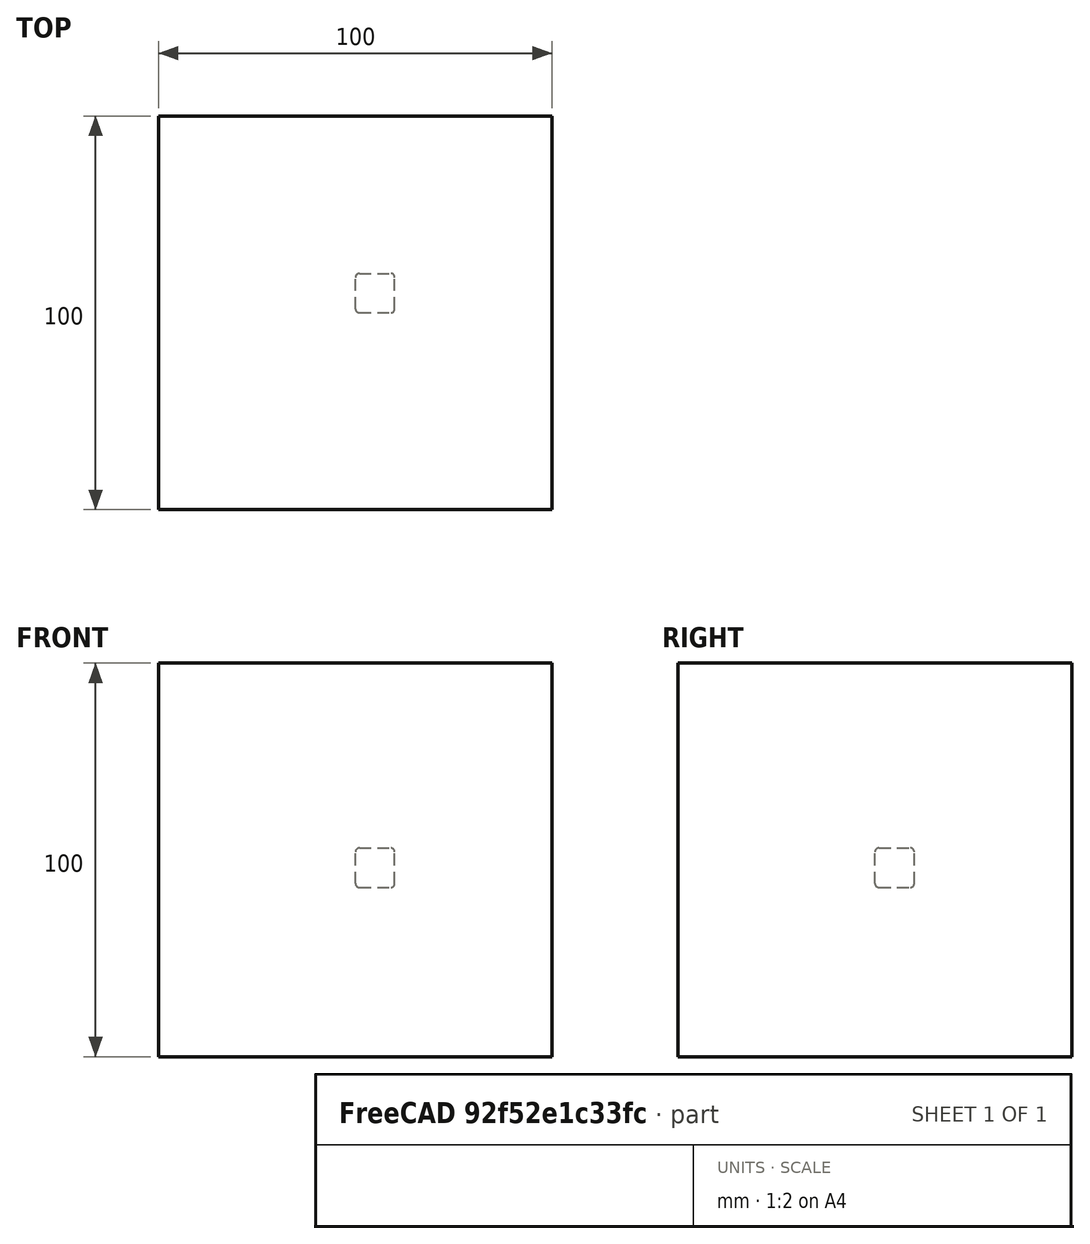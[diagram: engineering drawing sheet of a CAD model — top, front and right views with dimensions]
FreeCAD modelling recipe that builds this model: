
FCSTD DOCUMENT  (FreeCAD 1.0R39109 (Git))
Label: fillet
License: All rights reserved
objects: App::DocumentObjectGroupPython×1251, App::Part×2, Part::FeaturePython×1, Part::Box×1, Part::Fillet×1
note: 3 computed .brp shape members not serialized (recipe doc carries the construction recipe); baked Part::Feature solids carry a one-line shape summary decoded from their .brp

FEATURE [App::DocumentObjectGroupPython] HALFPI  # scripted group (container) (typed FeaturePython)
  name = HALFPI
  value = pi/2.
FEATURE [App::DocumentObjectGroupPython] PI  # scripted group (container) (typed FeaturePython)
  name = PI
  value = 1.*pi
FEATURE [App::DocumentObjectGroupPython] TWOPI  # scripted group (container) (typed FeaturePython)
  name = TWOPI
  value = 2.*pi
FEATURE [App::DocumentObjectGroupPython] Constants  # scripted group (container) (typed FeaturePython)
  Group = -> [HALFPI,PI,TWOPI]
FEATURE [App::DocumentObjectGroupPython] Variables  # scripted group (container) (typed FeaturePython)
FEATURE [App::DocumentObjectGroupPython] Quantities  # scripted group (container) (typed FeaturePython)
FEATURE [App::DocumentObjectGroupPython] Isotopes  # scripted group (container) (typed FeaturePython)
FEATURE [App::DocumentObjectGroupPython] Elements  # scripted group (container) (typed FeaturePython)
FEATURE [App::DocumentObjectGroupPython] Matrix  # scripted group (container) (typed FeaturePython)
FEATURE [App::DocumentObjectGroupPython] Surfaces  # scripted group (container) (typed FeaturePython)
FEATURE [App::DocumentObjectGroupPython] Opticals  # scripted group (container) (typed FeaturePython)
  Group = -> [Matrix,Surfaces]
FEATURE [App::DocumentObjectGroupPython] G4Isotopes  # scripted group (container) (typed FeaturePython)
FEATURE [App::DocumentObjectGroupPython] H_element  # scripted group (container) (typed FeaturePython)
  Z = 1
  atom_value = 1.008
  formula = H
  name = H_element
FEATURE [App::DocumentObjectGroupPython] He_element  # scripted group (container) (typed FeaturePython)
  Z = 2
  atom_value = 4.0026
  formula = He
  name = He_element
FEATURE [App::DocumentObjectGroupPython] Li_element  # scripted group (container) (typed FeaturePython)
  Z = 3
  atom_value = 6.94
  formula = Li
  name = Li_element
FEATURE [App::DocumentObjectGroupPython] Be_element  # scripted group (container) (typed FeaturePython)
  Z = 4
  atom_value = 9.01218
  formula = Be
  name = Be_element
FEATURE [App::DocumentObjectGroupPython] B_element  # scripted group (container) (typed FeaturePython)
  Z = 5
  atom_value = 10.81
  formula = B
  name = B_element
FEATURE [App::DocumentObjectGroupPython] C_element  # scripted group (container) (typed FeaturePython)
  Z = 6
  atom_value = 12.011
  formula = C
  name = C_element
FEATURE [App::DocumentObjectGroupPython] N_element  # scripted group (container) (typed FeaturePython)
  Z = 7
  atom_value = 14.007
  formula = N
  name = N_element
FEATURE [App::DocumentObjectGroupPython] O_element  # scripted group (container) (typed FeaturePython)
  Z = 8
  atom_value = 15.999
  formula = O
  name = O_element
FEATURE [App::DocumentObjectGroupPython] F_element  # scripted group (container) (typed FeaturePython)
  Z = 9
  atom_value = 18.9984
  formula = F
  name = F_element
FEATURE [App::DocumentObjectGroupPython] Ne_element  # scripted group (container) (typed FeaturePython)
  Z = 10
  atom_value = 20.1797
  formula = Ne
  name = Ne_element
FEATURE [App::DocumentObjectGroupPython] Na_element  # scripted group (container) (typed FeaturePython)
  Z = 11
  atom_value = 22.9898
  formula = Na
  name = Na_element
FEATURE [App::DocumentObjectGroupPython] Mg_element  # scripted group (container) (typed FeaturePython)
  Z = 12
  atom_value = 24.305
  formula = Mg
  name = Mg_element
FEATURE [App::DocumentObjectGroupPython] Al_element  # scripted group (container) (typed FeaturePython)
  Z = 13
  atom_value = 26.9815
  formula = Al
  name = Al_element
FEATURE [App::DocumentObjectGroupPython] Si_element  # scripted group (container) (typed FeaturePython)
  Z = 14
  atom_value = 28.085
  formula = Si
  name = Si_element
FEATURE [App::DocumentObjectGroupPython] P_element  # scripted group (container) (typed FeaturePython)
  Z = 15
  atom_value = 30.9738
  formula = P
  name = P_element
FEATURE [App::DocumentObjectGroupPython] S_element  # scripted group (container) (typed FeaturePython)
  Z = 16
  atom_value = 32.06
  formula = S
  name = S_element
FEATURE [App::DocumentObjectGroupPython] Cl_element  # scripted group (container) (typed FeaturePython)
  Z = 17
  atom_value = 35.45
  formula = Cl
  name = Cl_element
FEATURE [App::DocumentObjectGroupPython] Ar_element  # scripted group (container) (typed FeaturePython)
  Z = 18
  atom_value = 39.95
  formula = Ar
  name = Ar_element
FEATURE [App::DocumentObjectGroupPython] K_element  # scripted group (container) (typed FeaturePython)
  Z = 19
  atom_value = 39.0983
  formula = K
  name = K_element
FEATURE [App::DocumentObjectGroupPython] Ca_element  # scripted group (container) (typed FeaturePython)
  Z = 20
  atom_value = 40.078
  formula = Ca
  name = Ca_element
FEATURE [App::DocumentObjectGroupPython] Sc_element  # scripted group (container) (typed FeaturePython)
  Z = 21
  atom_value = 44.9559
  formula = Sc
  name = Sc_element
FEATURE [App::DocumentObjectGroupPython] Ti_element  # scripted group (container) (typed FeaturePython)
  Z = 22
  atom_value = 47.867
  formula = Ti
  name = Ti_element
FEATURE [App::DocumentObjectGroupPython] V_element  # scripted group (container) (typed FeaturePython)
  Z = 23
  atom_value = 50.9415
  formula = V
  name = V_element
FEATURE [App::DocumentObjectGroupPython] Cr_element  # scripted group (container) (typed FeaturePython)
  Z = 24
  atom_value = 51.9961
  formula = Cr
  name = Cr_element
FEATURE [App::DocumentObjectGroupPython] Mn_element  # scripted group (container) (typed FeaturePython)
  Z = 25
  atom_value = 54.938
  formula = Mn
  name = Mn_element
FEATURE [App::DocumentObjectGroupPython] Fe_element  # scripted group (container) (typed FeaturePython)
  Z = 26
  atom_value = 55.845
  formula = Fe
  name = Fe_element
FEATURE [App::DocumentObjectGroupPython] Co_element  # scripted group (container) (typed FeaturePython)
  Z = 27
  atom_value = 58.9332
  formula = Co
  name = Co_element
FEATURE [App::DocumentObjectGroupPython] Ni_element  # scripted group (container) (typed FeaturePython)
  Z = 28
  atom_value = 58.6934
  formula = Ni
  name = Ni_element
FEATURE [App::DocumentObjectGroupPython] Cu_element  # scripted group (container) (typed FeaturePython)
  Z = 29
  atom_value = 63.546
  formula = Cu
  name = Cu_element
FEATURE [App::DocumentObjectGroupPython] Zn_element  # scripted group (container) (typed FeaturePython)
  Z = 30
  atom_value = 65.38
  formula = Zn
  name = Zn_element
FEATURE [App::DocumentObjectGroupPython] Ga_element  # scripted group (container) (typed FeaturePython)
  Z = 31
  atom_value = 69.723
  formula = Ga
  name = Ga_element
FEATURE [App::DocumentObjectGroupPython] Ge_element  # scripted group (container) (typed FeaturePython)
  Z = 32
  atom_value = 72.63
  formula = Ge
  name = Ge_element
FEATURE [App::DocumentObjectGroupPython] As_element  # scripted group (container) (typed FeaturePython)
  Z = 33
  atom_value = 74.9216
  formula = As
  name = As_element
FEATURE [App::DocumentObjectGroupPython] Se_element  # scripted group (container) (typed FeaturePython)
  Z = 34
  atom_value = 78.971
  formula = Se
  name = Se_element
FEATURE [App::DocumentObjectGroupPython] Br_element  # scripted group (container) (typed FeaturePython)
  Z = 35
  atom_value = 79.904
  formula = Br
  name = Br_element
FEATURE [App::DocumentObjectGroupPython] Kr_element  # scripted group (container) (typed FeaturePython)
  Z = 36
  atom_value = 83.798
  formula = Kr
  name = Kr_element
FEATURE [App::DocumentObjectGroupPython] Rb_element  # scripted group (container) (typed FeaturePython)
  Z = 37
  atom_value = 85.4678
  formula = Rb
  name = Rb_element
FEATURE [App::DocumentObjectGroupPython] Sr_element  # scripted group (container) (typed FeaturePython)
  Z = 38
  atom_value = 87.62
  formula = Sr
  name = Sr_element
FEATURE [App::DocumentObjectGroupPython] Y_element  # scripted group (container) (typed FeaturePython)
  Z = 39
  atom_value = 88.9058
  formula = Y
  name = Y_element
FEATURE [App::DocumentObjectGroupPython] Zr_element  # scripted group (container) (typed FeaturePython)
  Z = 40
  atom_value = 91.224
  formula = Zr
  name = Zr_element
FEATURE [App::DocumentObjectGroupPython] Nb_element  # scripted group (container) (typed FeaturePython)
  Z = 41
  atom_value = 92.9064
  formula = Nb
  name = Nb_element
FEATURE [App::DocumentObjectGroupPython] Mo_element  # scripted group (container) (typed FeaturePython)
  Z = 42
  atom_value = 95.95
  formula = Mo
  name = Mo_element
FEATURE [App::DocumentObjectGroupPython] Tc_element  # scripted group (container) (typed FeaturePython)
  Z = 43
  atom_value = 97
  formula = Tc
  name = Tc_element
FEATURE [App::DocumentObjectGroupPython] Ru_element  # scripted group (container) (typed FeaturePython)
  Z = 44
  atom_value = 101.07
  formula = Ru
  name = Ru_element
FEATURE [App::DocumentObjectGroupPython] Rh_element  # scripted group (container) (typed FeaturePython)
  Z = 45
  atom_value = 102.905
  formula = Rh
  name = Rh_element
FEATURE [App::DocumentObjectGroupPython] Pd_element  # scripted group (container) (typed FeaturePython)
  Z = 46
  atom_value = 106.42
  formula = Pd
  name = Pd_element
FEATURE [App::DocumentObjectGroupPython] Ag_element  # scripted group (container) (typed FeaturePython)
  Z = 47
  atom_value = 107.868
  formula = Ag
  name = Ag_element
FEATURE [App::DocumentObjectGroupPython] Cd_element  # scripted group (container) (typed FeaturePython)
  Z = 48
  atom_value = 112.414
  formula = Cd
  name = Cd_element
FEATURE [App::DocumentObjectGroupPython] In_element  # scripted group (container) (typed FeaturePython)
  Z = 49
  atom_value = 114.818
  formula = In
  name = In_element
FEATURE [App::DocumentObjectGroupPython] Sn_element  # scripted group (container) (typed FeaturePython)
  Z = 50
  atom_value = 118.71
  formula = Sn
  name = Sn_element
FEATURE [App::DocumentObjectGroupPython] Sb_element  # scripted group (container) (typed FeaturePython)
  Z = 51
  atom_value = 121.76
  formula = Sb
  name = Sb_element
FEATURE [App::DocumentObjectGroupPython] Te_element  # scripted group (container) (typed FeaturePython)
  Z = 52
  atom_value = 127.6
  formula = Te
  name = Te_element
FEATURE [App::DocumentObjectGroupPython] I_element  # scripted group (container) (typed FeaturePython)
  Z = 53
  atom_value = 126.904
  formula = I
  name = I_element
FEATURE [App::DocumentObjectGroupPython] Xe_element  # scripted group (container) (typed FeaturePython)
  Z = 54
  atom_value = 131.293
  formula = Xe
  name = Xe_element
FEATURE [App::DocumentObjectGroupPython] Cs_element  # scripted group (container) (typed FeaturePython)
  Z = 55
  atom_value = 132.905
  formula = Cs
  name = Cs_element
FEATURE [App::DocumentObjectGroupPython] Ba_element  # scripted group (container) (typed FeaturePython)
  Z = 56
  atom_value = 137.327
  formula = Ba
  name = Ba_element
FEATURE [App::DocumentObjectGroupPython] La_element  # scripted group (container) (typed FeaturePython)
  Z = 57
  atom_value = 138.905
  formula = La
  name = La_element
FEATURE [App::DocumentObjectGroupPython] Ce_element  # scripted group (container) (typed FeaturePython)
  Z = 58
  atom_value = 140.116
  formula = Ce
  name = Ce_element
FEATURE [App::DocumentObjectGroupPython] Pr_element  # scripted group (container) (typed FeaturePython)
  Z = 59
  atom_value = 140.908
  formula = Pr
  name = Pr_element
FEATURE [App::DocumentObjectGroupPython] Nd_element  # scripted group (container) (typed FeaturePython)
  Z = 60
  atom_value = 144.242
  formula = Nd
  name = Nd_element
FEATURE [App::DocumentObjectGroupPython] Pm_element  # scripted group (container) (typed FeaturePython)
  Z = 61
  atom_value = 145
  formula = Pm
  name = Pm_element
FEATURE [App::DocumentObjectGroupPython] Sm_element  # scripted group (container) (typed FeaturePython)
  Z = 62
  atom_value = 150.36
  formula = Sm
  name = Sm_element
FEATURE [App::DocumentObjectGroupPython] Eu_element  # scripted group (container) (typed FeaturePython)
  Z = 63
  atom_value = 151.964
  formula = Eu
  name = Eu_element
FEATURE [App::DocumentObjectGroupPython] Gd_element  # scripted group (container) (typed FeaturePython)
  Z = 64
  atom_value = 157.25
  formula = Gd
  name = Gd_element
FEATURE [App::DocumentObjectGroupPython] Tb_element  # scripted group (container) (typed FeaturePython)
  Z = 65
  atom_value = 158.925
  formula = Tb
  name = Tb_element
FEATURE [App::DocumentObjectGroupPython] Dy_element  # scripted group (container) (typed FeaturePython)
  Z = 66
  atom_value = 162.5
  formula = Dy
  name = Dy_element
FEATURE [App::DocumentObjectGroupPython] Ho_element  # scripted group (container) (typed FeaturePython)
  Z = 67
  atom_value = 164.93
  formula = Ho
  name = Ho_element
FEATURE [App::DocumentObjectGroupPython] Er_element  # scripted group (container) (typed FeaturePython)
  Z = 68
  atom_value = 167.259
  formula = Er
  name = Er_element
FEATURE [App::DocumentObjectGroupPython] Tm_element  # scripted group (container) (typed FeaturePython)
  Z = 69
  atom_value = 168.934
  formula = Tm
  name = Tm_element
FEATURE [App::DocumentObjectGroupPython] Yb_element  # scripted group (container) (typed FeaturePython)
  Z = 70
  atom_value = 173.045
  formula = Yb
  name = Yb_element
FEATURE [App::DocumentObjectGroupPython] Lu_element  # scripted group (container) (typed FeaturePython)
  Z = 71
  atom_value = 174.967
  formula = Lu
  name = Lu_element
FEATURE [App::DocumentObjectGroupPython] Hf_element  # scripted group (container) (typed FeaturePython)
  Z = 72
  atom_value = 178.49
  formula = Hf
  name = Hf_element
FEATURE [App::DocumentObjectGroupPython] Ta_element  # scripted group (container) (typed FeaturePython)
  Z = 73
  atom_value = 180.948
  formula = Ta
  name = Ta_element
FEATURE [App::DocumentObjectGroupPython] W_element  # scripted group (container) (typed FeaturePython)
  Z = 74
  atom_value = 183.84
  formula = W
  name = W_element
FEATURE [App::DocumentObjectGroupPython] Re_element  # scripted group (container) (typed FeaturePython)
  Z = 75
  atom_value = 186.207
  formula = Re
  name = Re_element
FEATURE [App::DocumentObjectGroupPython] Os_element  # scripted group (container) (typed FeaturePython)
  Z = 76
  atom_value = 190.23
  formula = Os
  name = Os_element
FEATURE [App::DocumentObjectGroupPython] Ir_element  # scripted group (container) (typed FeaturePython)
  Z = 77
  atom_value = 192.217
  formula = Ir
  name = Ir_element
FEATURE [App::DocumentObjectGroupPython] Pt_element  # scripted group (container) (typed FeaturePython)
  Z = 78
  atom_value = 195.084
  formula = Pt
  name = Pt_element
FEATURE [App::DocumentObjectGroupPython] Au_element  # scripted group (container) (typed FeaturePython)
  Z = 79
  atom_value = 196.967
  formula = Au
  name = Au_element
FEATURE [App::DocumentObjectGroupPython] Hg_element  # scripted group (container) (typed FeaturePython)
  Z = 80
  atom_value = 200.592
  formula = Hg
  name = Hg_element
FEATURE [App::DocumentObjectGroupPython] Tl_element  # scripted group (container) (typed FeaturePython)
  Z = 81
  atom_value = 204.38
  formula = Tl
  name = Tl_element
FEATURE [App::DocumentObjectGroupPython] Pb_element  # scripted group (container) (typed FeaturePython)
  Z = 82
  atom_value = 207.2
  formula = Pb
  name = Pb_element
FEATURE [App::DocumentObjectGroupPython] Bi_element  # scripted group (container) (typed FeaturePython)
  Z = 83
  atom_value = 208.98
  formula = Bi
  name = Bi_element
FEATURE [App::DocumentObjectGroupPython] Po_element  # scripted group (container) (typed FeaturePython)
  Z = 84
  atom_value = 209
  formula = Po
  name = Po_element
FEATURE [App::DocumentObjectGroupPython] At_element  # scripted group (container) (typed FeaturePython)
  Z = 85
  atom_value = 210
  formula = At
  name = At_element
FEATURE [App::DocumentObjectGroupPython] Rn_element  # scripted group (container) (typed FeaturePython)
  Z = 86
  atom_value = 222
  formula = Rn
  name = Rn_element
FEATURE [App::DocumentObjectGroupPython] Fr_element  # scripted group (container) (typed FeaturePython)
  Z = 87
  atom_value = 223
  formula = Fr
  name = Fr_element
FEATURE [App::DocumentObjectGroupPython] Ra_element  # scripted group (container) (typed FeaturePython)
  Z = 88
  atom_value = 226
  formula = Ra
  name = Ra_element
FEATURE [App::DocumentObjectGroupPython] Ac_element  # scripted group (container) (typed FeaturePython)
  Z = 89
  atom_value = 227
  formula = Ac
  name = Ac_element
FEATURE [App::DocumentObjectGroupPython] Th_element  # scripted group (container) (typed FeaturePython)
  Z = 90
  atom_value = 232.038
  formula = Th
  name = Th_element
FEATURE [App::DocumentObjectGroupPython] Pa_element  # scripted group (container) (typed FeaturePython)
  Z = 91
  atom_value = 231.036
  formula = Pa
  name = Pa_element
FEATURE [App::DocumentObjectGroupPython] U_element  # scripted group (container) (typed FeaturePython)
  Z = 92
  atom_value = 238.029
  formula = U
  name = U_element
FEATURE [App::DocumentObjectGroupPython] Np_element  # scripted group (container) (typed FeaturePython)
  Z = 93
  atom_value = 237
  formula = Np
  name = Np_element
FEATURE [App::DocumentObjectGroupPython] Pu_element  # scripted group (container) (typed FeaturePython)
  Z = 94
  atom_value = 244
  formula = Pu
  name = Pu_element
FEATURE [App::DocumentObjectGroupPython] Am_element  # scripted group (container) (typed FeaturePython)
  Z = 95
  atom_value = 243
  formula = Am
  name = Am_element
FEATURE [App::DocumentObjectGroupPython] Cm_element  # scripted group (container) (typed FeaturePython)
  Z = 96
  atom_value = 247
  formula = Cm
  name = Cm_element
FEATURE [App::DocumentObjectGroupPython] Bk_element  # scripted group (container) (typed FeaturePython)
  Z = 97
  atom_value = 247
  formula = Bk
  name = Bk_element
FEATURE [App::DocumentObjectGroupPython] Cf_element  # scripted group (container) (typed FeaturePython)
  Z = 98
  atom_value = 251
  formula = Cf
  name = Cf_element
FEATURE [App::DocumentObjectGroupPython] G4Elements  # scripted group (container) (typed FeaturePython)
  Group = -> [H_element,He_element,Li_element,Be_element,B_element,C_element,N_element,O_element,F_element,Ne_element,Na_element,Mg_element,Al_element,Si_element,P_element,S_element,Cl_element,Ar_element,K_element,Ca_element,Sc_element,Ti_element,V_element,Cr_element,Mn_element,Fe_element,Co_element,Ni_element,Cu_element,Zn_element,Ga_element,Ge_element,As_element,Se_element,Br_element,Kr_element,Rb_element,+61 more]
FEATURE [App::DocumentObjectGroupPython] H_element001  label="H_element : 0.101"  # scripted group (container) (typed FeaturePython)
  n = 0.101327
FEATURE [App::DocumentObjectGroupPython] C_element001  label="C_element : 0.775"  # scripted group (container) (typed FeaturePython)
  n = 0.7755
FEATURE [App::DocumentObjectGroupPython] N_element001  label="N_element : 0.035"  # scripted group (container) (typed FeaturePython)
  n = 0.035057
FEATURE [App::DocumentObjectGroupPython] O_element001  label="O_element : 0.052"  # scripted group (container) (typed FeaturePython)
  n = 0.0523159
FEATURE [App::DocumentObjectGroupPython] F_element001  label="F_element : 0.017"  # scripted group (container) (typed FeaturePython)
  n = 0.017422
FEATURE [App::DocumentObjectGroupPython] Ca_element001  label="Ca_element : 0.018"  # scripted group (container) (typed FeaturePython)
  n = 0.018378
FEATURE [App::DocumentObjectGroupPython] G4_A_150_TISSUE  label="G4_A-150_TISSUE"  # scripted group (container) (typed FeaturePython)
  Dunit = g/cm3
  Dvalue = 1.127
  Group = -> [H_element001,C_element001,N_element001,O_element001,F_element001,Ca_element001]
  conduct = 2
  density = 1
  expand = 3
  formula = G4_A-150_TISSUE
  name = G4_A-150_TISSUE
  specific = 4
FEATURE [App::DocumentObjectGroupPython] C_element002  label="C_element : 3"  # scripted group (container) (typed FeaturePython)
  n = 3
  ref = C_element
FEATURE [App::DocumentObjectGroupPython] H_element002  label="H_element : 6"  # scripted group (container) (typed FeaturePython)
  n = 6
  ref = H_element
FEATURE [App::DocumentObjectGroupPython] O_element002  label="O_element : 1"  # scripted group (container) (typed FeaturePython)
  n = 1
  ref = O_element
FEATURE [App::DocumentObjectGroupPython] G4_ACETONE  # scripted group (container) (typed FeaturePython)
  Dunit = g/cm3
  Dvalue = 0.7899
  Group = -> [C_element002,H_element002,O_element002]
  conduct = 2
  density = 1
  expand = 3
  formula = G4_ACETONE
  name = G4_ACETONE
  specific = 4
FEATURE [App::DocumentObjectGroupPython] C_element003  label="C_element : 2"  # scripted group (container) (typed FeaturePython)
  n = 2
  ref = C_element
FEATURE [App::DocumentObjectGroupPython] H_element003  label="H_element : 2"  # scripted group (container) (typed FeaturePython)
  n = 2
  ref = H_element
FEATURE [App::DocumentObjectGroupPython] G4_ACETYLENE  # scripted group (container) (typed FeaturePython)
  Dunit = g/cm3
  Dvalue = 0.0010967
  Group = -> [C_element003,H_element003]
  conduct = 2
  density = 1
  expand = 3
  formula = G4_ACETYLENE
  name = G4_ACETYLENE
  specific = 4
FEATURE [App::DocumentObjectGroupPython] C_element004  label="C_element : 5"  # scripted group (container) (typed FeaturePython)
  n = 5
  ref = C_element
FEATURE [App::DocumentObjectGroupPython] H_element004  label="H_element : 5"  # scripted group (container) (typed FeaturePython)
  n = 5
  ref = H_element
FEATURE [App::DocumentObjectGroupPython] N_element002  label="N_element : 5"  # scripted group (container) (typed FeaturePython)
  n = 5
  ref = N_element
FEATURE [App::DocumentObjectGroupPython] G4_ADENINE  # scripted group (container) (typed FeaturePython)
  Dunit = g/cm3
  Dvalue = 1.6
  Group = -> [C_element004,H_element004,N_element002]
  conduct = 2
  density = 1
  expand = 3
  formula = G4_ADENINE
  name = G4_ADENINE
  specific = 4
FEATURE [App::DocumentObjectGroupPython] H_element005  label="H_element : 0.114"  # scripted group (container) (typed FeaturePython)
  n = 0.114
FEATURE [App::DocumentObjectGroupPython] C_element005  label="C_element : 0.598"  # scripted group (container) (typed FeaturePython)
  n = 0.598
FEATURE [App::DocumentObjectGroupPython] N_element003  label="N_element : 0.007"  # scripted group (container) (typed FeaturePython)
  n = 0.007
FEATURE [App::DocumentObjectGroupPython] O_element003  label="O_element : 0.278"  # scripted group (container) (typed FeaturePython)
  n = 0.278
FEATURE [App::DocumentObjectGroupPython] Na_element001  label="Na_element : 0.001"  # scripted group (container) (typed FeaturePython)
  n = 0.001
FEATURE [App::DocumentObjectGroupPython] S_element001  label="S_element : 0.001"  # scripted group (container) (typed FeaturePython)
  n = 0.001
FEATURE [App::DocumentObjectGroupPython] Cl_element001  label="Cl_element : 0.001"  # scripted group (container) (typed FeaturePython)
  n = 0.001
FEATURE [App::DocumentObjectGroupPython] G4_ADIPOSE_TISSUE_ICRP  # scripted group (container) (typed FeaturePython)
  Dunit = g/cm3
  Dvalue = 0.95
  Group = -> [H_element005,C_element005,N_element003,O_element003,Na_element001,S_element001,Cl_element001]
  conduct = 2
  density = 1
  expand = 3
  formula = G4_ADIPOSE_TISSUE_ICRP
  name = G4_ADIPOSE_TISSUE_ICRP
  specific = 4
FEATURE [App::DocumentObjectGroupPython] C_element006  label="C_element : 0.000"  # scripted group (container) (typed FeaturePython)
  n = 0.000124
FEATURE [App::DocumentObjectGroupPython] N_element004  label="N_element : 0.755"  # scripted group (container) (typed FeaturePython)
  n = 0.755268
FEATURE [App::DocumentObjectGroupPython] O_element004  label="O_element : 0.232"  # scripted group (container) (typed FeaturePython)
  n = 0.231781
FEATURE [App::DocumentObjectGroupPython] Ar_element001  label="Ar_element : 0.013"  # scripted group (container) (typed FeaturePython)
  n = 0.012827
FEATURE [App::DocumentObjectGroupPython] G4_AIR  # scripted group (container) (typed FeaturePython)
  Dunit = g/cm3
  Dvalue = 0.00120479
  Group = -> [C_element006,N_element004,O_element004,Ar_element001]
  conduct = 2
  density = 1
  expand = 3
  formula = G4_AIR
  name = G4_AIR
  specific = 4
FEATURE [App::DocumentObjectGroupPython] C_element007  label="C_element : 006"  # scripted group (container) (typed FeaturePython)
  n = 3
  ref = C_element
FEATURE [App::DocumentObjectGroupPython] H_element006  label="H_element : 7"  # scripted group (container) (typed FeaturePython)
  n = 7
  ref = H_element
FEATURE [App::DocumentObjectGroupPython] N_element005  label="N_element : 1"  # scripted group (container) (typed FeaturePython)
  n = 1
  ref = N_element
FEATURE [App::DocumentObjectGroupPython] O_element005  label="O_element : 2"  # scripted group (container) (typed FeaturePython)
  n = 2
  ref = O_element
FEATURE [App::DocumentObjectGroupPython] G4_ALANINE  # scripted group (container) (typed FeaturePython)
  Dunit = g/cm3
  Dvalue = 1.42
  Group = -> [C_element007,H_element006,N_element005,O_element005]
  conduct = 2
  density = 1
  expand = 3
  formula = G4_ALANINE
  name = G4_ALANINE
  specific = 4
FEATURE [App::DocumentObjectGroupPython] Al_element001  label="Al_element : 2"  # scripted group (container) (typed FeaturePython)
  n = 2
  ref = Al_element
FEATURE [App::DocumentObjectGroupPython] O_element006  label="O_element : 3"  # scripted group (container) (typed FeaturePython)
  n = 3
  ref = O_element
FEATURE [App::DocumentObjectGroupPython] G4_ALUMINUM_OXIDE  # scripted group (container) (typed FeaturePython)
  Dunit = g/cm3
  Dvalue = 3.97
  Group = -> [Al_element001,O_element006]
  conduct = 2
  density = 1
  expand = 3
  formula = G4_ALUMINUM_OXIDE
  name = G4_ALUMINUM_OXIDE
  specific = 4
FEATURE [App::DocumentObjectGroupPython] H_element007  label="H_element : 0.106"  # scripted group (container) (typed FeaturePython)
  n = 0.10593
FEATURE [App::DocumentObjectGroupPython] C_element008  label="C_element : 0.789"  # scripted group (container) (typed FeaturePython)
  n = 0.788974
FEATURE [App::DocumentObjectGroupPython] O_element007  label="O_element : 0.105"  # scripted group (container) (typed FeaturePython)
  n = 0.105096
FEATURE [App::DocumentObjectGroupPython] G4_AMBER  # scripted group (container) (typed FeaturePython)
  Dunit = g/cm3
  Dvalue = 1.1
  Group = -> [H_element007,C_element008,O_element007]
  conduct = 2
  density = 1
  expand = 3
  formula = G4_AMBER
  name = G4_AMBER
  specific = 4
FEATURE [App::DocumentObjectGroupPython] N_element006  label="N_element : 006"  # scripted group (container) (typed FeaturePython)
  n = 1
  ref = N_element
FEATURE [App::DocumentObjectGroupPython] H_element008  label="H_element : 3"  # scripted group (container) (typed FeaturePython)
  n = 3
  ref = H_element
FEATURE [App::DocumentObjectGroupPython] G4_AMMONIA  # scripted group (container) (typed FeaturePython)
  Dunit = g/cm3
  Dvalue = 0.000826019
  Group = -> [N_element006,H_element008]
  conduct = 2
  density = 1
  expand = 3
  formula = G4_AMMONIA
  name = G4_AMMONIA
  specific = 4
FEATURE [App::DocumentObjectGroupPython] C_element009  label="C_element : 6"  # scripted group (container) (typed FeaturePython)
  n = 6
  ref = C_element
FEATURE [App::DocumentObjectGroupPython] H_element009  label="H_element : 008"  # scripted group (container) (typed FeaturePython)
  n = 7
  ref = H_element
FEATURE [App::DocumentObjectGroupPython] N_element007  label="N_element : 007"  # scripted group (container) (typed FeaturePython)
  n = 1
  ref = N_element
FEATURE [App::DocumentObjectGroupPython] G4_ANILINE  # scripted group (container) (typed FeaturePython)
  Dunit = g/cm3
  Dvalue = 1.0235
  Group = -> [C_element009,H_element009,N_element007]
  conduct = 2
  density = 1
  expand = 3
  formula = G4_ANILINE
  name = G4_ANILINE
  specific = 4
FEATURE [App::DocumentObjectGroupPython] C_element010  label="C_element : 14"  # scripted group (container) (typed FeaturePython)
  n = 14
  ref = C_element
FEATURE [App::DocumentObjectGroupPython] H_element010  label="H_element : 10"  # scripted group (container) (typed FeaturePython)
  n = 10
  ref = H_element
FEATURE [App::DocumentObjectGroupPython] G4_ANTHRACENE  # scripted group (container) (typed FeaturePython)
  Dunit = g/cm3
  Dvalue = 1.283
  Group = -> [C_element010,H_element010]
  conduct = 2
  density = 1
  expand = 3
  formula = G4_ANTHRACENE
  name = G4_ANTHRACENE
  specific = 4
FEATURE [App::DocumentObjectGroupPython] H_element011  label="H_element : 0.065"  # scripted group (container) (typed FeaturePython)
  n = 0.0654709
FEATURE [App::DocumentObjectGroupPython] C_element011  label="C_element : 0.537"  # scripted group (container) (typed FeaturePython)
  n = 0.536944
FEATURE [App::DocumentObjectGroupPython] N_element008  label="N_element : 0.021"  # scripted group (container) (typed FeaturePython)
  n = 0.0215
FEATURE [App::DocumentObjectGroupPython] O_element008  label="O_element : 0.032"  # scripted group (container) (typed FeaturePython)
  n = 0.032085
FEATURE [App::DocumentObjectGroupPython] F_element002  label="F_element : 0.167"  # scripted group (container) (typed FeaturePython)
  n = 0.167411
FEATURE [App::DocumentObjectGroupPython] Ca_element002  label="Ca_element : 0.177"  # scripted group (container) (typed FeaturePython)
  n = 0.176589
FEATURE [App::DocumentObjectGroupPython] G4_B_100_BONE  label="G4_B-100_BONE"  # scripted group (container) (typed FeaturePython)
  Dunit = g/cm3
  Dvalue = 1.45
  Group = -> [H_element011,C_element011,N_element008,O_element008,F_element002,Ca_element002]
  conduct = 2
  density = 1
  expand = 3
  formula = G4_B-100_BONE
  name = G4_B-100_BONE
  specific = 4
FEATURE [App::DocumentObjectGroupPython] H_element012  label="H_element : 0.057"  # scripted group (container) (typed FeaturePython)
  n = 0.057441
FEATURE [App::DocumentObjectGroupPython] C_element012  label="C_element : 0.790"  # scripted group (container) (typed FeaturePython)
  n = 0.774591
FEATURE [App::DocumentObjectGroupPython] O_element009  label="O_element : 0.168"  # scripted group (container) (typed FeaturePython)
  n = 0.167968
FEATURE [App::DocumentObjectGroupPython] G4_BAKELITE  # scripted group (container) (typed FeaturePython)
  Dunit = g/cm3
  Dvalue = 1.25
  Group = -> [H_element012,C_element012,O_element009]
  conduct = 2
  density = 1
  expand = 3
  formula = G4_BAKELITE
  name = G4_BAKELITE
  specific = 4
FEATURE [App::DocumentObjectGroupPython] Ba_element001  label="Ba_element : 1"  # scripted group (container) (typed FeaturePython)
  n = 1
  ref = Ba_element
FEATURE [App::DocumentObjectGroupPython] F_element003  label="F_element : 2"  # scripted group (container) (typed FeaturePython)
  n = 2
  ref = F_element
FEATURE [App::DocumentObjectGroupPython] G4_BARIUM_FLUORIDE  # scripted group (container) (typed FeaturePython)
  Dunit = g/cm3
  Dvalue = 4.89
  Group = -> [Ba_element001,F_element003]
  conduct = 2
  density = 1
  expand = 3
  formula = G4_BARIUM_FLUORIDE
  name = G4_BARIUM_FLUORIDE
  specific = 4
FEATURE [App::DocumentObjectGroupPython] Ba_element002  label="Ba_element : 002"  # scripted group (container) (typed FeaturePython)
  n = 1
  ref = Ba_element
FEATURE [App::DocumentObjectGroupPython] S_element002  label="S_element : 1"  # scripted group (container) (typed FeaturePython)
  n = 1
  ref = S_element
FEATURE [App::DocumentObjectGroupPython] O_element010  label="O_element : 4"  # scripted group (container) (typed FeaturePython)
  n = 4
  ref = O_element
FEATURE [App::DocumentObjectGroupPython] G4_BARIUM_SULFATE  # scripted group (container) (typed FeaturePython)
  Dunit = g/cm3
  Dvalue = 4.5
  Group = -> [Ba_element002,S_element002,O_element010]
  conduct = 2
  density = 1
  expand = 3
  formula = G4_BARIUM_SULFATE
  name = G4_BARIUM_SULFATE
  specific = 4
FEATURE [App::DocumentObjectGroupPython] C_element013  label="C_element : 007"  # scripted group (container) (typed FeaturePython)
  n = 6
  ref = C_element
FEATURE [App::DocumentObjectGroupPython] H_element013  label="H_element : 009"  # scripted group (container) (typed FeaturePython)
  n = 6
  ref = H_element
FEATURE [App::DocumentObjectGroupPython] G4_BENZENE  # scripted group (container) (typed FeaturePython)
  Dunit = g/cm3
  Dvalue = 0.87865
  Group = -> [C_element013,H_element013]
  conduct = 2
  density = 1
  expand = 3
  formula = G4_BENZENE
  name = G4_BENZENE
  specific = 4
FEATURE [App::DocumentObjectGroupPython] Be_element001  label="Be_element : 1"  # scripted group (container) (typed FeaturePython)
  n = 1
  ref = Be_element
FEATURE [App::DocumentObjectGroupPython] O_element011  label="O_element : 005"  # scripted group (container) (typed FeaturePython)
  n = 1
  ref = O_element
FEATURE [App::DocumentObjectGroupPython] G4_BERYLLIUM_OXIDE  # scripted group (container) (typed FeaturePython)
  Dunit = g/cm3
  Dvalue = 3.01
  Group = -> [Be_element001,O_element011]
  conduct = 2
  density = 1
  expand = 3
  formula = G4_BERYLLIUM_OXIDE
  name = G4_BERYLLIUM_OXIDE
  specific = 4
FEATURE [App::DocumentObjectGroupPython] Bi_element001  label="Bi_element : 4"  # scripted group (container) (typed FeaturePython)
  n = 4
  ref = Bi_element
FEATURE [App::DocumentObjectGroupPython] Ge_element001  label="Ge_element : 3"  # scripted group (container) (typed FeaturePython)
  n = 3
  ref = Ge_element
FEATURE [App::DocumentObjectGroupPython] O_element012  label="O_element : 12"  # scripted group (container) (typed FeaturePython)
  n = 12
  ref = O_element
FEATURE [App::DocumentObjectGroupPython] G4_BGO  # scripted group (container) (typed FeaturePython)
  Dunit = g/cm3
  Dvalue = 7.13
  Group = -> [Bi_element001,Ge_element001,O_element012]
  conduct = 2
  density = 1
  expand = 3
  formula = G4_BGO
  name = G4_BGO
  specific = 4
FEATURE [App::DocumentObjectGroupPython] H_element014  label="H_element : 0.102"  # scripted group (container) (typed FeaturePython)
  n = 0.102
FEATURE [App::DocumentObjectGroupPython] C_element014  label="C_element : 0.110"  # scripted group (container) (typed FeaturePython)
  n = 0.11
FEATURE [App::DocumentObjectGroupPython] N_element009  label="N_element : 0.033"  # scripted group (container) (typed FeaturePython)
  n = 0.033
FEATURE [App::DocumentObjectGroupPython] O_element013  label="O_element : 0.745"  # scripted group (container) (typed FeaturePython)
  n = 0.745
FEATURE [App::DocumentObjectGroupPython] Na_element002  label="Na_element : 0.002"  # scripted group (container) (typed FeaturePython)
  n = 0.001
FEATURE [App::DocumentObjectGroupPython] P_element001  label="P_element : 0.001"  # scripted group (container) (typed FeaturePython)
  n = 0.001
FEATURE [App::DocumentObjectGroupPython] S_element003  label="S_element : 0.002"  # scripted group (container) (typed FeaturePython)
  n = 0.002
FEATURE [App::DocumentObjectGroupPython] Cl_element002  label="Cl_element : 0.003"  # scripted group (container) (typed FeaturePython)
  n = 0.003
FEATURE [App::DocumentObjectGroupPython] K_element001  label="K_element : 0.002"  # scripted group (container) (typed FeaturePython)
  n = 0.002
FEATURE [App::DocumentObjectGroupPython] Fe_element001  label="Fe_element : 0.001"  # scripted group (container) (typed FeaturePython)
  n = 0.001
FEATURE [App::DocumentObjectGroupPython] G4_BLOOD_ICRP  # scripted group (container) (typed FeaturePython)
  Dunit = g/cm3
  Dvalue = 1.06
  Group = -> [H_element014,C_element014,N_element009,O_element013,Na_element002,P_element001,S_element003,Cl_element002,K_element001,Fe_element001]
  conduct = 2
  density = 1
  expand = 3
  formula = G4_BLOOD_ICRP
  name = G4_BLOOD_ICRP
  specific = 4
FEATURE [App::DocumentObjectGroupPython] H_element015  label="H_element : 0.064"  # scripted group (container) (typed FeaturePython)
  n = 0.064
FEATURE [App::DocumentObjectGroupPython] C_element015  label="C_element : 0.278"  # scripted group (container) (typed FeaturePython)
  n = 0.278
FEATURE [App::DocumentObjectGroupPython] N_element010  label="N_element : 0.027"  # scripted group (container) (typed FeaturePython)
  n = 0.027
FEATURE [App::DocumentObjectGroupPython] O_element014  label="O_element : 0.410"  # scripted group (container) (typed FeaturePython)
  n = 0.41
FEATURE [App::DocumentObjectGroupPython] Mg_element001  label="Mg_element : 0.002"  # scripted group (container) (typed FeaturePython)
  n = 0.002
FEATURE [App::DocumentObjectGroupPython] P_element002  label="P_element : 0.070"  # scripted group (container) (typed FeaturePython)
  n = 0.07
FEATURE [App::DocumentObjectGroupPython] S_element004  label="S_element : 0.003"  # scripted group (container) (typed FeaturePython)
  n = 0.002
FEATURE [App::DocumentObjectGroupPython] Ca_element003  label="Ca_element : 0.147"  # scripted group (container) (typed FeaturePython)
  n = 0.147
FEATURE [App::DocumentObjectGroupPython] G4_BONE_COMPACT_ICRU  # scripted group (container) (typed FeaturePython)
  Dunit = g/cm3
  Dvalue = 1.85
  Group = -> [H_element015,C_element015,N_element010,O_element014,Mg_element001,P_element002,S_element004,Ca_element003]
  conduct = 2
  density = 1
  expand = 3
  formula = G4_BONE_COMPACT_ICRU
  name = G4_BONE_COMPACT_ICRU
  specific = 4
FEATURE [App::DocumentObjectGroupPython] H_element016  label="H_element : 0.034"  # scripted group (container) (typed FeaturePython)
  n = 0.034
FEATURE [App::DocumentObjectGroupPython] C_element016  label="C_element : 0.155"  # scripted group (container) (typed FeaturePython)
  n = 0.155
FEATURE [App::DocumentObjectGroupPython] N_element011  label="N_element : 0.042"  # scripted group (container) (typed FeaturePython)
  n = 0.042
FEATURE [App::DocumentObjectGroupPython] O_element015  label="O_element : 0.435"  # scripted group (container) (typed FeaturePython)
  n = 0.435
FEATURE [App::DocumentObjectGroupPython] Na_element003  label="Na_element : 0.003"  # scripted group (container) (typed FeaturePython)
  n = 0.001
FEATURE [App::DocumentObjectGroupPython] Mg_element002  label="Mg_element : 0.003"  # scripted group (container) (typed FeaturePython)
  n = 0.002
FEATURE [App::DocumentObjectGroupPython] P_element003  label="P_element : 0.103"  # scripted group (container) (typed FeaturePython)
  n = 0.103
FEATURE [App::DocumentObjectGroupPython] S_element005  label="S_element : 0.004"  # scripted group (container) (typed FeaturePython)
  n = 0.003
FEATURE [App::DocumentObjectGroupPython] Ca_element004  label="Ca_element : 0.225"  # scripted group (container) (typed FeaturePython)
  n = 0.225
FEATURE [App::DocumentObjectGroupPython] G4_BONE_CORTICAL_ICRP  # scripted group (container) (typed FeaturePython)
  Dunit = g/cm3
  Dvalue = 1.92
  Group = -> [H_element016,C_element016,N_element011,O_element015,Na_element003,Mg_element002,P_element003,S_element005,Ca_element004]
  conduct = 2
  density = 1
  expand = 3
  formula = G4_BONE_CORTICAL_ICRP
  name = G4_BONE_CORTICAL_ICRP
  specific = 4
FEATURE [App::DocumentObjectGroupPython] B_element001  label="B_element : 4"  # scripted group (container) (typed FeaturePython)
  n = 4
  ref = B_element
FEATURE [App::DocumentObjectGroupPython] C_element017  label="C_element : 1"  # scripted group (container) (typed FeaturePython)
  n = 1
  ref = C_element
FEATURE [App::DocumentObjectGroupPython] G4_BORON_CARBIDE  # scripted group (container) (typed FeaturePython)
  Dunit = g/cm3
  Dvalue = 2.52
  Group = -> [B_element001,C_element017]
  conduct = 2
  density = 1
  expand = 3
  formula = G4_BORON_CARBIDE
  name = G4_BORON_CARBIDE
  specific = 4
FEATURE [App::DocumentObjectGroupPython] B_element002  label="B_element : 2"  # scripted group (container) (typed FeaturePython)
  n = 2
  ref = B_element
FEATURE [App::DocumentObjectGroupPython] O_element016  label="O_element : 006"  # scripted group (container) (typed FeaturePython)
  n = 3
  ref = O_element
FEATURE [App::DocumentObjectGroupPython] G4_BORON_OXIDE  # scripted group (container) (typed FeaturePython)
  Dunit = g/cm3
  Dvalue = 1.812
  Group = -> [B_element002,O_element016]
  conduct = 2
  density = 1
  expand = 3
  formula = G4_BORON_OXIDE
  name = G4_BORON_OXIDE
  specific = 4
FEATURE [App::DocumentObjectGroupPython] H_element017  label="H_element : 0.107"  # scripted group (container) (typed FeaturePython)
  n = 0.107
FEATURE [App::DocumentObjectGroupPython] C_element018  label="C_element : 0.145"  # scripted group (container) (typed FeaturePython)
  n = 0.145
FEATURE [App::DocumentObjectGroupPython] N_element012  label="N_element : 0.022"  # scripted group (container) (typed FeaturePython)
  n = 0.022
FEATURE [App::DocumentObjectGroupPython] O_element017  label="O_element : 0.712"  # scripted group (container) (typed FeaturePython)
  n = 0.712
FEATURE [App::DocumentObjectGroupPython] Na_element004  label="Na_element : 0.004"  # scripted group (container) (typed FeaturePython)
  n = 0.002
FEATURE [App::DocumentObjectGroupPython] P_element004  label="P_element : 0.004"  # scripted group (container) (typed FeaturePython)
  n = 0.004
FEATURE [App::DocumentObjectGroupPython] S_element006  label="S_element : 0.005"  # scripted group (container) (typed FeaturePython)
  n = 0.002
FEATURE [App::DocumentObjectGroupPython] Cl_element003  label="Cl_element : 0.004"  # scripted group (container) (typed FeaturePython)
  n = 0.003
FEATURE [App::DocumentObjectGroupPython] K_element002  label="K_element : 0.003"  # scripted group (container) (typed FeaturePython)
  n = 0.003
FEATURE [App::DocumentObjectGroupPython] G4_BRAIN_ICRP  # scripted group (container) (typed FeaturePython)
  Dunit = g/cm3
  Dvalue = 1.04
  Group = -> [H_element017,C_element018,N_element012,O_element017,Na_element004,P_element004,S_element006,Cl_element003,K_element002]
  conduct = 2
  density = 1
  expand = 3
  formula = G4_BRAIN_ICRP
  name = G4_BRAIN_ICRP
  specific = 4
FEATURE [App::DocumentObjectGroupPython] C_element019  label="C_element : 4"  # scripted group (container) (typed FeaturePython)
  n = 4
  ref = C_element
FEATURE [App::DocumentObjectGroupPython] H_element018  label="H_element : 010"  # scripted group (container) (typed FeaturePython)
  n = 10
  ref = H_element
FEATURE [App::DocumentObjectGroupPython] G4_BUTANE  # scripted group (container) (typed FeaturePython)
  Dunit = g/cm3
  Dvalue = 0.00249343
  Group = -> [C_element019,H_element018]
  conduct = 2
  density = 1
  expand = 3
  formula = G4_BUTANE
  name = G4_BUTANE
  specific = 4
FEATURE [App::DocumentObjectGroupPython] C_element020  label="C_element : 008"  # scripted group (container) (typed FeaturePython)
  n = 4
  ref = C_element
FEATURE [App::DocumentObjectGroupPython] H_element019  label="H_element : 011"  # scripted group (container) (typed FeaturePython)
  n = 10
  ref = H_element
FEATURE [App::DocumentObjectGroupPython] O_element018  label="O_element : 007"  # scripted group (container) (typed FeaturePython)
  n = 1
  ref = O_element
FEATURE [App::DocumentObjectGroupPython] G4_N_BUTYL_ALCOHOL  label="G4_N-BUTYL_ALCOHOL"  # scripted group (container) (typed FeaturePython)
  Dunit = g/cm3
  Dvalue = 0.8098
  Group = -> [C_element020,H_element019,O_element018]
  conduct = 2
  density = 1
  expand = 3
  formula = G4_N-BUTYL_ALCOHOL
  name = G4_N-BUTYL_ALCOHOL
  specific = 4
FEATURE [App::DocumentObjectGroupPython] H_element020  label="H_element : 0.025"  # scripted group (container) (typed FeaturePython)
  n = 0.02468
FEATURE [App::DocumentObjectGroupPython] C_element021  label="C_element : 0.502"  # scripted group (container) (typed FeaturePython)
  n = 0.501611
FEATURE [App::DocumentObjectGroupPython] O_element019  label="O_element : 0.005"  # scripted group (container) (typed FeaturePython)
  n = 0.004527
FEATURE [App::DocumentObjectGroupPython] F_element004  label="F_element : 0.465"  # scripted group (container) (typed FeaturePython)
  n = 0.465209
FEATURE [App::DocumentObjectGroupPython] Si_element001  label="Si_element : 0.004"  # scripted group (container) (typed FeaturePython)
  n = 0.003973
FEATURE [App::DocumentObjectGroupPython] G4_C_552  label="G4_C-552"  # scripted group (container) (typed FeaturePython)
  Dunit = g/cm3
  Dvalue = 1.76
  Group = -> [H_element020,C_element021,O_element019,F_element004,Si_element001]
  conduct = 2
  density = 1
  expand = 3
  formula = G4_C-552
  name = G4_C-552
  specific = 4
FEATURE [App::DocumentObjectGroupPython] Cd_element001  label="Cd_element : 1"  # scripted group (container) (typed FeaturePython)
  n = 1
  ref = Cd_element
FEATURE [App::DocumentObjectGroupPython] Te_element001  label="Te_element : 1"  # scripted group (container) (typed FeaturePython)
  n = 1
  ref = Te_element
FEATURE [App::DocumentObjectGroupPython] G4_CADMIUM_TELLURIDE  # scripted group (container) (typed FeaturePython)
  Dunit = g/cm3
  Dvalue = 6.2
  Group = -> [Cd_element001,Te_element001]
  conduct = 2
  density = 1
  expand = 3
  formula = G4_CADMIUM_TELLURIDE
  name = G4_CADMIUM_TELLURIDE
  specific = 4
FEATURE [App::DocumentObjectGroupPython] Cd_element002  label="Cd_element : 002"  # scripted group (container) (typed FeaturePython)
  n = 1
  ref = Cd_element
FEATURE [App::DocumentObjectGroupPython] W_element001  label="W_element : 1"  # scripted group (container) (typed FeaturePython)
  n = 1
  ref = W_element
FEATURE [App::DocumentObjectGroupPython] O_element020  label="O_element : 008"  # scripted group (container) (typed FeaturePython)
  n = 4
  ref = O_element
FEATURE [App::DocumentObjectGroupPython] G4_CADMIUM_TUNGSTATE  # scripted group (container) (typed FeaturePython)
  Dunit = g/cm3
  Dvalue = 7.9
  Group = -> [Cd_element002,W_element001,O_element020]
  conduct = 2
  density = 1
  expand = 3
  formula = G4_CADMIUM_TUNGSTATE
  name = G4_CADMIUM_TUNGSTATE
  specific = 4
FEATURE [App::DocumentObjectGroupPython] Ca_element005  label="Ca_element : 1"  # scripted group (container) (typed FeaturePython)
  n = 1
  ref = Ca_element
FEATURE [App::DocumentObjectGroupPython] C_element022  label="C_element : 009"  # scripted group (container) (typed FeaturePython)
  n = 1
  ref = C_element
FEATURE [App::DocumentObjectGroupPython] O_element021  label="O_element : 009"  # scripted group (container) (typed FeaturePython)
  n = 3
  ref = O_element
FEATURE [App::DocumentObjectGroupPython] G4_CALCIUM_CARBONATE  # scripted group (container) (typed FeaturePython)
  Dunit = g/cm3
  Dvalue = 2.8
  Group = -> [Ca_element005,C_element022,O_element021]
  conduct = 2
  density = 1
  expand = 3
  formula = G4_CALCIUM_CARBONATE
  name = G4_CALCIUM_CARBONATE
  specific = 4
FEATURE [App::DocumentObjectGroupPython] Ca_element006  label="Ca_element : 002"  # scripted group (container) (typed FeaturePython)
  n = 1
  ref = Ca_element
FEATURE [App::DocumentObjectGroupPython] F_element005  label="F_element : 003"  # scripted group (container) (typed FeaturePython)
  n = 2
  ref = F_element
FEATURE [App::DocumentObjectGroupPython] G4_CALCIUM_FLUORIDE  # scripted group (container) (typed FeaturePython)
  Dunit = g/cm3
  Dvalue = 3.18
  Group = -> [Ca_element006,F_element005]
  conduct = 2
  density = 1
  expand = 3
  formula = G4_CALCIUM_FLUORIDE
  name = G4_CALCIUM_FLUORIDE
  specific = 4
FEATURE [App::DocumentObjectGroupPython] Ca_element007  label="Ca_element : 003"  # scripted group (container) (typed FeaturePython)
  n = 1
  ref = Ca_element
FEATURE [App::DocumentObjectGroupPython] O_element022  label="O_element : 010"  # scripted group (container) (typed FeaturePython)
  n = 1
  ref = O_element
FEATURE [App::DocumentObjectGroupPython] G4_CALCIUM_OXIDE  # scripted group (container) (typed FeaturePython)
  Dunit = g/cm3
  Dvalue = 3.3
  Group = -> [Ca_element007,O_element022]
  conduct = 2
  density = 1
  expand = 3
  formula = G4_CALCIUM_OXIDE
  name = G4_CALCIUM_OXIDE
  specific = 4
FEATURE [App::DocumentObjectGroupPython] Ca_element008  label="Ca_element : 004"  # scripted group (container) (typed FeaturePython)
  n = 1
  ref = Ca_element
FEATURE [App::DocumentObjectGroupPython] S_element007  label="S_element : 002"  # scripted group (container) (typed FeaturePython)
  n = 1
  ref = S_element
FEATURE [App::DocumentObjectGroupPython] O_element023  label="O_element : 011"  # scripted group (container) (typed FeaturePython)
  n = 4
  ref = O_element
FEATURE [App::DocumentObjectGroupPython] G4_CALCIUM_SULFATE  # scripted group (container) (typed FeaturePython)
  Dunit = g/cm3
  Dvalue = 2.96
  Group = -> [Ca_element008,S_element007,O_element023]
  conduct = 2
  density = 1
  expand = 3
  formula = G4_CALCIUM_SULFATE
  name = G4_CALCIUM_SULFATE
  specific = 4
FEATURE [App::DocumentObjectGroupPython] Ca_element009  label="Ca_element : 005"  # scripted group (container) (typed FeaturePython)
  n = 1
  ref = Ca_element
FEATURE [App::DocumentObjectGroupPython] W_element002  label="W_element : 002"  # scripted group (container) (typed FeaturePython)
  n = 1
  ref = W_element
FEATURE [App::DocumentObjectGroupPython] O_element024  label="O_element : 012"  # scripted group (container) (typed FeaturePython)
  n = 4
  ref = O_element
FEATURE [App::DocumentObjectGroupPython] G4_CALCIUM_TUNGSTATE  # scripted group (container) (typed FeaturePython)
  Dunit = g/cm3
  Dvalue = 6.062
  Group = -> [Ca_element009,W_element002,O_element024]
  conduct = 2
  density = 1
  expand = 3
  formula = G4_CALCIUM_TUNGSTATE
  name = G4_CALCIUM_TUNGSTATE
  specific = 4
FEATURE [App::DocumentObjectGroupPython] C_element023  label="C_element : 010"  # scripted group (container) (typed FeaturePython)
  n = 1
  ref = C_element
FEATURE [App::DocumentObjectGroupPython] O_element025  label="O_element : 013"  # scripted group (container) (typed FeaturePython)
  n = 2
  ref = O_element
FEATURE [App::DocumentObjectGroupPython] G4_CARBON_DIOXIDE  # scripted group (container) (typed FeaturePython)
  Dunit = g/cm3
  Dvalue = 0.00184212
  Group = -> [C_element023,O_element025]
  conduct = 2
  density = 1
  expand = 3
  formula = G4_CARBON_DIOXIDE
  name = G4_CARBON_DIOXIDE
  specific = 4
FEATURE [App::DocumentObjectGroupPython] C_element024  label="C_element : 011"  # scripted group (container) (typed FeaturePython)
  n = 1
  ref = C_element
FEATURE [App::DocumentObjectGroupPython] Cl_element004  label="Cl_element : 4"  # scripted group (container) (typed FeaturePython)
  n = 4
  ref = Cl_element
FEATURE [App::DocumentObjectGroupPython] G4_CARBON_TETRACHLORIDE  # scripted group (container) (typed FeaturePython)
  Dunit = g/cm3
  Dvalue = 1.594
  Group = -> [C_element024,Cl_element004]
  conduct = 2
  density = 1
  expand = 3
  formula = G4_CARBON_TETRACHLORIDE
  name = G4_CARBON_TETRACHLORIDE
  specific = 4
FEATURE [App::DocumentObjectGroupPython] C_element025  label="C_element : 012"  # scripted group (container) (typed FeaturePython)
  n = 6
  ref = C_element
FEATURE [App::DocumentObjectGroupPython] H_element021  label="H_element : 012"  # scripted group (container) (typed FeaturePython)
  n = 10
  ref = H_element
FEATURE [App::DocumentObjectGroupPython] O_element026  label="O_element : 5"  # scripted group (container) (typed FeaturePython)
  n = 5
  ref = O_element
FEATURE [App::DocumentObjectGroupPython] G4_CELLULOSE_CELLOPHANE  # scripted group (container) (typed FeaturePython)
  Dunit = g/cm3
  Dvalue = 1.42
  Group = -> [C_element025,H_element021,O_element026]
  conduct = 2
  density = 1
  expand = 3
  formula = G4_CELLULOSE_CELLOPHANE
  name = G4_CELLULOSE_CELLOPHANE
  specific = 4
FEATURE [App::DocumentObjectGroupPython] H_element022  label="H_element : 0.067"  # scripted group (container) (typed FeaturePython)
  n = 0.067125
FEATURE [App::DocumentObjectGroupPython] C_element026  label="C_element : 0.545"  # scripted group (container) (typed FeaturePython)
  n = 0.545403
FEATURE [App::DocumentObjectGroupPython] O_element027  label="O_element : 0.387"  # scripted group (container) (typed FeaturePython)
  n = 0.387472
FEATURE [App::DocumentObjectGroupPython] G4_CELLULOSE_BUTYRATE  # scripted group (container) (typed FeaturePython)
  Dunit = g/cm3
  Dvalue = 1.2
  Group = -> [H_element022,C_element026,O_element027]
  conduct = 2
  density = 1
  expand = 3
  formula = G4_CELLULOSE_BUTYRATE
  name = G4_CELLULOSE_BUTYRATE
  specific = 4
FEATURE [App::DocumentObjectGroupPython] H_element023  label="H_element : 0.029"  # scripted group (container) (typed FeaturePython)
  n = 0.029216
FEATURE [App::DocumentObjectGroupPython] C_element027  label="C_element : 0.271"  # scripted group (container) (typed FeaturePython)
  n = 0.271296
FEATURE [App::DocumentObjectGroupPython] N_element013  label="N_element : 0.121"  # scripted group (container) (typed FeaturePython)
  n = 0.121276
FEATURE [App::DocumentObjectGroupPython] O_element028  label="O_element : 0.578"  # scripted group (container) (typed FeaturePython)
  n = 0.578212
FEATURE [App::DocumentObjectGroupPython] G4_CELLULOSE_NITRATE  # scripted group (container) (typed FeaturePython)
  Dunit = g/cm3
  Dvalue = 1.49
  Group = -> [H_element023,C_element027,N_element013,O_element028]
  conduct = 2
  density = 1
  expand = 3
  formula = G4_CELLULOSE_NITRATE
  name = G4_CELLULOSE_NITRATE
  specific = 4
FEATURE [App::DocumentObjectGroupPython] H_element024  label="H_element : 0.108"  # scripted group (container) (typed FeaturePython)
  n = 0.107596
FEATURE [App::DocumentObjectGroupPython] N_element014  label="N_element : 0.001"  # scripted group (container) (typed FeaturePython)
  n = 0.0008
FEATURE [App::DocumentObjectGroupPython] O_element029  label="O_element : 0.875"  # scripted group (container) (typed FeaturePython)
  n = 0.874976
FEATURE [App::DocumentObjectGroupPython] S_element008  label="S_element : 0.015"  # scripted group (container) (typed FeaturePython)
  n = 0.014627
FEATURE [App::DocumentObjectGroupPython] Ce_element001  label="Ce_element : 0.002"  # scripted group (container) (typed FeaturePython)
  n = 0.002001
FEATURE [App::DocumentObjectGroupPython] G4_CERIC_SULFATE  # scripted group (container) (typed FeaturePython)
  Dunit = g/cm3
  Dvalue = 1.03
  Group = -> [H_element024,N_element014,O_element029,S_element008,Ce_element001]
  conduct = 2
  density = 1
  expand = 3
  formula = G4_CERIC_SULFATE
  name = G4_CERIC_SULFATE
  specific = 4
FEATURE [App::DocumentObjectGroupPython] Cs_element001  label="Cs_element : 1"  # scripted group (container) (typed FeaturePython)
  n = 1
  ref = Cs_element
FEATURE [App::DocumentObjectGroupPython] F_element006  label="F_element : 1"  # scripted group (container) (typed FeaturePython)
  n = 1
  ref = F_element
FEATURE [App::DocumentObjectGroupPython] G4_CESIUM_FLUORIDE  # scripted group (container) (typed FeaturePython)
  Dunit = g/cm3
  Dvalue = 4.115
  Group = -> [Cs_element001,F_element006]
  conduct = 2
  density = 1
  expand = 3
  formula = G4_CESIUM_FLUORIDE
  name = G4_CESIUM_FLUORIDE
  specific = 4
FEATURE [App::DocumentObjectGroupPython] Cs_element002  label="Cs_element : 002"  # scripted group (container) (typed FeaturePython)
  n = 1
  ref = Cs_element
FEATURE [App::DocumentObjectGroupPython] I_element001  label="I_element : 1"  # scripted group (container) (typed FeaturePython)
  n = 1
  ref = I_element
FEATURE [App::DocumentObjectGroupPython] G4_CESIUM_IODIDE  # scripted group (container) (typed FeaturePython)
  Dunit = g/cm3
  Dvalue = 4.51
  Group = -> [Cs_element002,I_element001]
  conduct = 2
  density = 1
  expand = 3
  formula = G4_CESIUM_IODIDE
  name = G4_CESIUM_IODIDE
  specific = 4
FEATURE [App::DocumentObjectGroupPython] C_element028  label="C_element : 013"  # scripted group (container) (typed FeaturePython)
  n = 6
  ref = C_element
FEATURE [App::DocumentObjectGroupPython] H_element025  label="H_element : 013"  # scripted group (container) (typed FeaturePython)
  n = 5
  ref = H_element
FEATURE [App::DocumentObjectGroupPython] Cl_element005  label="Cl_element : 1"  # scripted group (container) (typed FeaturePython)
  n = 1
  ref = Cl_element
FEATURE [App::DocumentObjectGroupPython] G4_CHLOROBENZENE  # scripted group (container) (typed FeaturePython)
  Dunit = g/cm3
  Dvalue = 1.1058
  Group = -> [C_element028,H_element025,Cl_element005]
  conduct = 2
  density = 1
  expand = 3
  formula = G4_CHLOROBENZENE
  name = G4_CHLOROBENZENE
  specific = 4
FEATURE [App::DocumentObjectGroupPython] C_element029  label="C_element : 014"  # scripted group (container) (typed FeaturePython)
  n = 1
  ref = C_element
FEATURE [App::DocumentObjectGroupPython] H_element026  label="H_element : 1"  # scripted group (container) (typed FeaturePython)
  n = 1
  ref = H_element
FEATURE [App::DocumentObjectGroupPython] Cl_element006  label="Cl_element : 3"  # scripted group (container) (typed FeaturePython)
  n = 3
  ref = Cl_element
FEATURE [App::DocumentObjectGroupPython] G4_CHLOROFORM  # scripted group (container) (typed FeaturePython)
  Dunit = g/cm3
  Dvalue = 1.4832
  Group = -> [C_element029,H_element026,Cl_element006]
  conduct = 2
  density = 1
  expand = 3
  formula = G4_CHLOROFORM
  name = G4_CHLOROFORM
  specific = 4
FEATURE [App::DocumentObjectGroupPython] H_element027  label="H_element : 0.010"  # scripted group (container) (typed FeaturePython)
  n = 0.01
FEATURE [App::DocumentObjectGroupPython] C_element030  label="C_element : 0.001"  # scripted group (container) (typed FeaturePython)
  n = 0.001
FEATURE [App::DocumentObjectGroupPython] O_element030  label="O_element : 0.529"  # scripted group (container) (typed FeaturePython)
  n = 0.529107
FEATURE [App::DocumentObjectGroupPython] Na_element005  label="Na_element : 0.016"  # scripted group (container) (typed FeaturePython)
  n = 0.016
FEATURE [App::DocumentObjectGroupPython] Mg_element003  label="Mg_element : 0.004"  # scripted group (container) (typed FeaturePython)
  n = 0.002
FEATURE [App::DocumentObjectGroupPython] Al_element002  label="Al_element : 0.034"  # scripted group (container) (typed FeaturePython)
  n = 0.033872
FEATURE [App::DocumentObjectGroupPython] Si_element002  label="Si_element : 0.337"  # scripted group (container) (typed FeaturePython)
  n = 0.337021
FEATURE [App::DocumentObjectGroupPython] K_element003  label="K_element : 0.013"  # scripted group (container) (typed FeaturePython)
  n = 0.013
FEATURE [App::DocumentObjectGroupPython] Ca_element010  label="Ca_element : 0.044"  # scripted group (container) (typed FeaturePython)
  n = 0.044
FEATURE [App::DocumentObjectGroupPython] Fe_element002  label="Fe_element : 0.014"  # scripted group (container) (typed FeaturePython)
  n = 0.014
FEATURE [App::DocumentObjectGroupPython] G4_CONCRETE  # scripted group (container) (typed FeaturePython)
  Dunit = g/cm3
  Dvalue = 2.3
  Group = -> [H_element027,C_element030,O_element030,Na_element005,Mg_element003,Al_element002,Si_element002,K_element003,Ca_element010,Fe_element002]
  conduct = 2
  density = 1
  expand = 3
  formula = G4_CONCRETE
  name = G4_CONCRETE
  specific = 4
FEATURE [App::DocumentObjectGroupPython] C_element031  label="C_element : 015"  # scripted group (container) (typed FeaturePython)
  n = 6
  ref = C_element
FEATURE [App::DocumentObjectGroupPython] H_element028  label="H_element : 12"  # scripted group (container) (typed FeaturePython)
  n = 12
  ref = H_element
FEATURE [App::DocumentObjectGroupPython] G4_CYCLOHEXANE  # scripted group (container) (typed FeaturePython)
  Dunit = g/cm3
  Dvalue = 0.779
  Group = -> [C_element031,H_element028]
  conduct = 2
  density = 1
  expand = 3
  formula = G4_CYCLOHEXANE
  name = G4_CYCLOHEXANE
  specific = 4
FEATURE [App::DocumentObjectGroupPython] C_element032  label="C_element : 016"  # scripted group (container) (typed FeaturePython)
  n = 6
  ref = C_element
FEATURE [App::DocumentObjectGroupPython] H_element029  label="H_element : 4"  # scripted group (container) (typed FeaturePython)
  n = 4
  ref = H_element
FEATURE [App::DocumentObjectGroupPython] Cl_element007  label="Cl_element : 2"  # scripted group (container) (typed FeaturePython)
  n = 2
  ref = Cl_element
FEATURE [App::DocumentObjectGroupPython] G4_1_2_DICHLOROBENZENE  label="G4_1.2-DICHLOROBENZENE"  # scripted group (container) (typed FeaturePython)
  Dunit = g/cm3
  Dvalue = 1.3048
  Group = -> [C_element032,H_element029,Cl_element007]
  conduct = 2
  density = 1
  expand = 3
  formula = G4_1.2-DICHLOROBENZENE
  name = G4_1.2-DICHLOROBENZENE
  specific = 4
FEATURE [App::DocumentObjectGroupPython] C_element033  label="C_element : 017"  # scripted group (container) (typed FeaturePython)
  n = 4
  ref = C_element
FEATURE [App::DocumentObjectGroupPython] H_element030  label="H_element : 8"  # scripted group (container) (typed FeaturePython)
  n = 8
  ref = H_element
FEATURE [App::DocumentObjectGroupPython] O_element031  label="O_element : 014"  # scripted group (container) (typed FeaturePython)
  n = 1
  ref = O_element
FEATURE [App::DocumentObjectGroupPython] Cl_element008  label="Cl_element : 005"  # scripted group (container) (typed FeaturePython)
  n = 2
  ref = Cl_element
FEATURE [App::DocumentObjectGroupPython] G4_DICHLORODIETHYL_ETHER  # scripted group (container) (typed FeaturePython)
  Dunit = g/cm3
  Dvalue = 1.2199
  Group = -> [C_element033,H_element030,O_element031,Cl_element008]
  conduct = 2
  density = 1
  expand = 3
  formula = G4_DICHLORODIETHYL_ETHER
  name = G4_DICHLORODIETHYL_ETHER
  specific = 4
FEATURE [App::DocumentObjectGroupPython] C_element034  label="C_element : 018"  # scripted group (container) (typed FeaturePython)
  n = 2
  ref = C_element
FEATURE [App::DocumentObjectGroupPython] H_element031  label="H_element : 014"  # scripted group (container) (typed FeaturePython)
  n = 4
  ref = H_element
FEATURE [App::DocumentObjectGroupPython] Cl_element009  label="Cl_element : 006"  # scripted group (container) (typed FeaturePython)
  n = 2
  ref = Cl_element
FEATURE [App::DocumentObjectGroupPython] G4_1_2_DICHLOROETHANE  label="G4_1.2-DICHLOROETHANE"  # scripted group (container) (typed FeaturePython)
  Dunit = g/cm3
  Dvalue = 1.2351
  Group = -> [C_element034,H_element031,Cl_element009]
  conduct = 2
  density = 1
  expand = 3
  formula = G4_1.2-DICHLOROETHANE
  name = G4_1.2-DICHLOROETHANE
  specific = 4
FEATURE [App::DocumentObjectGroupPython] C_element035  label="C_element : 019"  # scripted group (container) (typed FeaturePython)
  n = 4
  ref = C_element
FEATURE [App::DocumentObjectGroupPython] H_element032  label="H_element : 015"  # scripted group (container) (typed FeaturePython)
  n = 10
  ref = H_element
FEATURE [App::DocumentObjectGroupPython] O_element032  label="O_element : 015"  # scripted group (container) (typed FeaturePython)
  n = 1
  ref = O_element
FEATURE [App::DocumentObjectGroupPython] G4_DIETHYL_ETHER  # scripted group (container) (typed FeaturePython)
  Dunit = g/cm3
  Dvalue = 0.71378
  Group = -> [C_element035,H_element032,O_element032]
  conduct = 2
  density = 1
  expand = 3
  formula = G4_DIETHYL_ETHER
  name = G4_DIETHYL_ETHER
  specific = 4
FEATURE [App::DocumentObjectGroupPython] C_element036  label="C_element : 020"  # scripted group (container) (typed FeaturePython)
  n = 3
  ref = C_element
FEATURE [App::DocumentObjectGroupPython] H_element033  label="H_element : 016"  # scripted group (container) (typed FeaturePython)
  n = 7
  ref = H_element
FEATURE [App::DocumentObjectGroupPython] N_element015  label="N_element : 008"  # scripted group (container) (typed FeaturePython)
  n = 1
  ref = N_element
FEATURE [App::DocumentObjectGroupPython] O_element033  label="O_element : 016"  # scripted group (container) (typed FeaturePython)
  n = 1
  ref = O_element
FEATURE [App::DocumentObjectGroupPython] G4_N_N_DIMETHYL_FORMAMIDE  label="G4_N.N-DIMETHYL_FORMAMIDE"  # scripted group (container) (typed FeaturePython)
  Dunit = g/cm3
  Dvalue = 0.9487
  Group = -> [C_element036,H_element033,N_element015,O_element033]
  conduct = 2
  density = 1
  expand = 3
  formula = G4_N.N-DIMETHYL_FORMAMIDE
  name = G4_N.N-DIMETHYL_FORMAMIDE
  specific = 4
FEATURE [App::DocumentObjectGroupPython] C_element037  label="C_element : 021"  # scripted group (container) (typed FeaturePython)
  n = 2
  ref = C_element
FEATURE [App::DocumentObjectGroupPython] H_element034  label="H_element : 017"  # scripted group (container) (typed FeaturePython)
  n = 6
  ref = H_element
FEATURE [App::DocumentObjectGroupPython] O_element034  label="O_element : 017"  # scripted group (container) (typed FeaturePython)
  n = 1
  ref = O_element
FEATURE [App::DocumentObjectGroupPython] S_element009  label="S_element : 003"  # scripted group (container) (typed FeaturePython)
  n = 1
  ref = S_element
FEATURE [App::DocumentObjectGroupPython] G4_DIMETHYL_SULFOXIDE  # scripted group (container) (typed FeaturePython)
  Dunit = g/cm3
  Dvalue = 1.1014
  Group = -> [C_element037,H_element034,O_element034,S_element009]
  conduct = 2
  density = 1
  expand = 3
  formula = G4_DIMETHYL_SULFOXIDE
  name = G4_DIMETHYL_SULFOXIDE
  specific = 4
FEATURE [App::DocumentObjectGroupPython] C_element038  label="C_element : 022"  # scripted group (container) (typed FeaturePython)
  n = 2
  ref = C_element
FEATURE [App::DocumentObjectGroupPython] H_element035  label="H_element : 018"  # scripted group (container) (typed FeaturePython)
  n = 6
  ref = H_element
FEATURE [App::DocumentObjectGroupPython] G4_ETHANE  # scripted group (container) (typed FeaturePython)
  Dunit = g/cm3
  Dvalue = 0.00125324
  Group = -> [C_element038,H_element035]
  conduct = 2
  density = 1
  expand = 3
  formula = G4_ETHANE
  name = G4_ETHANE
  specific = 4
FEATURE [App::DocumentObjectGroupPython] C_element039  label="C_element : 023"  # scripted group (container) (typed FeaturePython)
  n = 2
  ref = C_element
FEATURE [App::DocumentObjectGroupPython] H_element036  label="H_element : 019"  # scripted group (container) (typed FeaturePython)
  n = 6
  ref = H_element
FEATURE [App::DocumentObjectGroupPython] O_element035  label="O_element : 018"  # scripted group (container) (typed FeaturePython)
  n = 1
  ref = O_element
FEATURE [App::DocumentObjectGroupPython] G4_ETHYL_ALCOHOL  # scripted group (container) (typed FeaturePython)
  Dunit = g/cm3
  Dvalue = 0.7893
  Group = -> [C_element039,H_element036,O_element035]
  conduct = 2
  density = 1
  expand = 3
  formula = G4_ETHYL_ALCOHOL
  name = G4_ETHYL_ALCOHOL
  specific = 4
FEATURE [App::DocumentObjectGroupPython] H_element037  label="H_element : 0.090"  # scripted group (container) (typed FeaturePython)
  n = 0.090027
FEATURE [App::DocumentObjectGroupPython] C_element040  label="C_element : 0.585"  # scripted group (container) (typed FeaturePython)
  n = 0.585182
FEATURE [App::DocumentObjectGroupPython] O_element036  label="O_element : 0.325"  # scripted group (container) (typed FeaturePython)
  n = 0.324791
FEATURE [App::DocumentObjectGroupPython] G4_ETHYL_CELLULOSE  # scripted group (container) (typed FeaturePython)
  Dunit = g/cm3
  Dvalue = 1.13
  Group = -> [H_element037,C_element040,O_element036]
  conduct = 2
  density = 1
  expand = 3
  formula = G4_ETHYL_CELLULOSE
  name = G4_ETHYL_CELLULOSE
  specific = 4
FEATURE [App::DocumentObjectGroupPython] C_element041  label="C_element : 024"  # scripted group (container) (typed FeaturePython)
  n = 2
  ref = C_element
FEATURE [App::DocumentObjectGroupPython] H_element038  label="H_element : 020"  # scripted group (container) (typed FeaturePython)
  n = 4
  ref = H_element
FEATURE [App::DocumentObjectGroupPython] G4_ETHYLENE  # scripted group (container) (typed FeaturePython)
  Dunit = g/cm3
  Dvalue = 0.00117497
  Group = -> [C_element041,H_element038]
  conduct = 2
  density = 1
  expand = 3
  formula = G4_ETHYLENE
  name = G4_ETHYLENE
  specific = 4
FEATURE [App::DocumentObjectGroupPython] H_element039  label="H_element : 0.096"  # scripted group (container) (typed FeaturePython)
  n = 0.096
FEATURE [App::DocumentObjectGroupPython] C_element042  label="C_element : 0.195"  # scripted group (container) (typed FeaturePython)
  n = 0.195
FEATURE [App::DocumentObjectGroupPython] N_element016  label="N_element : 0.057"  # scripted group (container) (typed FeaturePython)
  n = 0.057
FEATURE [App::DocumentObjectGroupPython] O_element037  label="O_element : 0.646"  # scripted group (container) (typed FeaturePython)
  n = 0.646
FEATURE [App::DocumentObjectGroupPython] Na_element006  label="Na_element : 0.017"  # scripted group (container) (typed FeaturePython)
  n = 0.001
FEATURE [App::DocumentObjectGroupPython] P_element005  label="P_element : 0.104"  # scripted group (container) (typed FeaturePython)
  n = 0.001
FEATURE [App::DocumentObjectGroupPython] S_element010  label="S_element : 0.016"  # scripted group (container) (typed FeaturePython)
  n = 0.003
FEATURE [App::DocumentObjectGroupPython] Cl_element010  label="Cl_element : 0.005"  # scripted group (container) (typed FeaturePython)
  n = 0.001
FEATURE [App::DocumentObjectGroupPython] G4_EYE_LENS_ICRP  # scripted group (container) (typed FeaturePython)
  Dunit = g/cm3
  Dvalue = 1.07
  Group = -> [H_element039,C_element042,N_element016,O_element037,Na_element006,P_element005,S_element010,Cl_element010]
  conduct = 2
  density = 1
  expand = 3
  formula = G4_EYE_LENS_ICRP
  name = G4_EYE_LENS_ICRP
  specific = 4
FEATURE [App::DocumentObjectGroupPython] Fe_element003  label="Fe_element : 2"  # scripted group (container) (typed FeaturePython)
  n = 2
  ref = Fe_element
FEATURE [App::DocumentObjectGroupPython] O_element038  label="O_element : 019"  # scripted group (container) (typed FeaturePython)
  n = 3
  ref = O_element
FEATURE [App::DocumentObjectGroupPython] G4_FERRIC_OXIDE  # scripted group (container) (typed FeaturePython)
  Dunit = g/cm3
  Dvalue = 5.2
  Group = -> [Fe_element003,O_element038]
  conduct = 2
  density = 1
  expand = 3
  formula = G4_FERRIC_OXIDE
  name = G4_FERRIC_OXIDE
  specific = 4
FEATURE [App::DocumentObjectGroupPython] Fe_element004  label="Fe_element : 1"  # scripted group (container) (typed FeaturePython)
  n = 1
  ref = Fe_element
FEATURE [App::DocumentObjectGroupPython] B_element003  label="B_element : 1"  # scripted group (container) (typed FeaturePython)
  n = 1
  ref = B_element
FEATURE [App::DocumentObjectGroupPython] G4_FERROBORIDE  # scripted group (container) (typed FeaturePython)
  Dunit = g/cm3
  Dvalue = 7.15
  Group = -> [Fe_element004,B_element003]
  conduct = 2
  density = 1
  expand = 3
  formula = G4_FERROBORIDE
  name = G4_FERROBORIDE
  specific = 4
FEATURE [App::DocumentObjectGroupPython] Fe_element005  label="Fe_element : 003"  # scripted group (container) (typed FeaturePython)
  n = 1
  ref = Fe_element
FEATURE [App::DocumentObjectGroupPython] O_element039  label="O_element : 020"  # scripted group (container) (typed FeaturePython)
  n = 1
  ref = O_element
FEATURE [App::DocumentObjectGroupPython] G4_FERROUS_OXIDE  # scripted group (container) (typed FeaturePython)
  Dunit = g/cm3
  Dvalue = 5.7
  Group = -> [Fe_element005,O_element039]
  conduct = 2
  density = 1
  expand = 3
  formula = G4_FERROUS_OXIDE
  name = G4_FERROUS_OXIDE
  specific = 4
FEATURE [App::DocumentObjectGroupPython] H_element040  label="H_element : 0.115"  # scripted group (container) (typed FeaturePython)
  n = 0.108259
FEATURE [App::DocumentObjectGroupPython] N_element017  label="N_element : 0.000"  # scripted group (container) (typed FeaturePython)
  n = 2.7e-05
FEATURE [App::DocumentObjectGroupPython] O_element040  label="O_element : 0.879"  # scripted group (container) (typed FeaturePython)
  n = 0.878636
FEATURE [App::DocumentObjectGroupPython] Na_element007  label="Na_element : 0.000"  # scripted group (container) (typed FeaturePython)
  n = 2.2e-05
FEATURE [App::DocumentObjectGroupPython] S_element011  label="S_element : 0.013"  # scripted group (container) (typed FeaturePython)
  n = 0.012968
FEATURE [App::DocumentObjectGroupPython] Cl_element011  label="Cl_element : 0.000"  # scripted group (container) (typed FeaturePython)
  n = 3.4e-05
FEATURE [App::DocumentObjectGroupPython] Fe_element006  label="Fe_element : 0.000"  # scripted group (container) (typed FeaturePython)
  n = 5.4e-05
FEATURE [App::DocumentObjectGroupPython] G4_FERROUS_SULFATE  # scripted group (container) (typed FeaturePython)
  Dunit = g/cm3
  Dvalue = 1.024
  Group = -> [H_element040,N_element017,O_element040,Na_element007,S_element011,Cl_element011,Fe_element006]
  conduct = 2
  density = 1
  expand = 3
  formula = G4_FERROUS_SULFATE
  name = G4_FERROUS_SULFATE
  specific = 4
FEATURE [App::DocumentObjectGroupPython] C_element043  label="C_element : 0.099"  # scripted group (container) (typed FeaturePython)
  n = 0.099335
FEATURE [App::DocumentObjectGroupPython] F_element007  label="F_element : 0.314"  # scripted group (container) (typed FeaturePython)
  n = 0.314247
FEATURE [App::DocumentObjectGroupPython] Cl_element012  label="Cl_element : 0.586"  # scripted group (container) (typed FeaturePython)
  n = 0.586418
FEATURE [App::DocumentObjectGroupPython] G4_FREON_12  label="G4_FREON-12"  # scripted group (container) (typed FeaturePython)
  Dunit = g/cm3
  Dvalue = 1.12
  Group = -> [C_element043,F_element007,Cl_element012]
  conduct = 2
  density = 1
  expand = 3
  formula = G4_FREON-12
  name = G4_FREON-12
  specific = 4
FEATURE [App::DocumentObjectGroupPython] C_element044  label="C_element : 0.057"  # scripted group (container) (typed FeaturePython)
  n = 0.057245
FEATURE [App::DocumentObjectGroupPython] F_element008  label="F_element : 0.181"  # scripted group (container) (typed FeaturePython)
  n = 0.181096
FEATURE [App::DocumentObjectGroupPython] Br_element001  label="Br_element : 0.762"  # scripted group (container) (typed FeaturePython)
  n = 0.761659
FEATURE [App::DocumentObjectGroupPython] G4_FREON_12B2  label="G4_FREON-12B2"  # scripted group (container) (typed FeaturePython)
  Dunit = g/cm3
  Dvalue = 1.8
  Group = -> [C_element044,F_element008,Br_element001]
  conduct = 2
  density = 1
  expand = 3
  formula = G4_FREON-12B2
  name = G4_FREON-12B2
  specific = 4
FEATURE [App::DocumentObjectGroupPython] C_element045  label="C_element : 0.115"  # scripted group (container) (typed FeaturePython)
  n = 0.114983
FEATURE [App::DocumentObjectGroupPython] F_element009  label="F_element : 0.546"  # scripted group (container) (typed FeaturePython)
  n = 0.545621
FEATURE [App::DocumentObjectGroupPython] Cl_element013  label="Cl_element : 0.339"  # scripted group (container) (typed FeaturePython)
  n = 0.339396
FEATURE [App::DocumentObjectGroupPython] G4_FREON_13  label="G4_FREON-13"  # scripted group (container) (typed FeaturePython)
  Dunit = g/cm3
  Dvalue = 0.95
  Group = -> [C_element045,F_element009,Cl_element013]
  conduct = 2
  density = 1
  expand = 3
  formula = G4_FREON-13
  name = G4_FREON-13
  specific = 4
FEATURE [App::DocumentObjectGroupPython] C_element046  label="C_element : 025"  # scripted group (container) (typed FeaturePython)
  n = 1
  ref = C_element
FEATURE [App::DocumentObjectGroupPython] F_element010  label="F_element : 3"  # scripted group (container) (typed FeaturePython)
  n = 3
  ref = F_element
FEATURE [App::DocumentObjectGroupPython] Br_element002  label="Br_element : 1"  # scripted group (container) (typed FeaturePython)
  n = 1
  ref = Br_element
FEATURE [App::DocumentObjectGroupPython] G4_FREON_13B1  label="G4_FREON-13B1"  # scripted group (container) (typed FeaturePython)
  Dunit = g/cm3
  Dvalue = 1.5
  Group = -> [C_element046,F_element010,Br_element002]
  conduct = 2
  density = 1
  expand = 3
  formula = G4_FREON-13B1
  name = G4_FREON-13B1
  specific = 4
FEATURE [App::DocumentObjectGroupPython] C_element047  label="C_element : 0.061"  # scripted group (container) (typed FeaturePython)
  n = 0.061309
FEATURE [App::DocumentObjectGroupPython] F_element011  label="F_element : 0.291"  # scripted group (container) (typed FeaturePython)
  n = 0.290924
FEATURE [App::DocumentObjectGroupPython] I_element002  label="I_element : 0.648"  # scripted group (container) (typed FeaturePython)
  n = 0.647767
FEATURE [App::DocumentObjectGroupPython] G4_FREON_13I1  label="G4_FREON-13I1"  # scripted group (container) (typed FeaturePython)
  Dunit = g/cm3
  Dvalue = 1.8
  Group = -> [C_element047,F_element011,I_element002]
  conduct = 2
  density = 1
  expand = 3
  formula = G4_FREON-13I1
  name = G4_FREON-13I1
  specific = 4
FEATURE [App::DocumentObjectGroupPython] Gd_element001  label="Gd_element : 2"  # scripted group (container) (typed FeaturePython)
  n = 2
  ref = Gd_element
FEATURE [App::DocumentObjectGroupPython] O_element041  label="O_element : 021"  # scripted group (container) (typed FeaturePython)
  n = 2
  ref = O_element
FEATURE [App::DocumentObjectGroupPython] S_element012  label="S_element : 004"  # scripted group (container) (typed FeaturePython)
  n = 1
  ref = S_element
FEATURE [App::DocumentObjectGroupPython] G4_GADOLINIUM_OXYSULFIDE  # scripted group (container) (typed FeaturePython)
  Dunit = g/cm3
  Dvalue = 7.44
  Group = -> [Gd_element001,O_element041,S_element012]
  conduct = 2
  density = 1
  expand = 3
  formula = G4_GADOLINIUM_OXYSULFIDE
  name = G4_GADOLINIUM_OXYSULFIDE
  specific = 4
FEATURE [App::DocumentObjectGroupPython] Ga_element001  label="Ga_element : 1"  # scripted group (container) (typed FeaturePython)
  n = 1
  ref = Ga_element
FEATURE [App::DocumentObjectGroupPython] As_element001  label="As_element : 1"  # scripted group (container) (typed FeaturePython)
  n = 1
  ref = As_element
FEATURE [App::DocumentObjectGroupPython] G4_GALLIUM_ARSENIDE  # scripted group (container) (typed FeaturePython)
  Dunit = g/cm3
  Dvalue = 5.31
  Group = -> [Ga_element001,As_element001]
  conduct = 2
  density = 1
  expand = 3
  formula = G4_GALLIUM_ARSENIDE
  name = G4_GALLIUM_ARSENIDE
  specific = 4
FEATURE [App::DocumentObjectGroupPython] H_element041  label="H_element : 0.081"  # scripted group (container) (typed FeaturePython)
  n = 0.08118
FEATURE [App::DocumentObjectGroupPython] C_element048  label="C_element : 0.416"  # scripted group (container) (typed FeaturePython)
  n = 0.41606
FEATURE [App::DocumentObjectGroupPython] N_element018  label="N_element : 0.111"  # scripted group (container) (typed FeaturePython)
  n = 0.11124
FEATURE [App::DocumentObjectGroupPython] O_element042  label="O_element : 0.381"  # scripted group (container) (typed FeaturePython)
  n = 0.38064
FEATURE [App::DocumentObjectGroupPython] S_element013  label="S_element : 0.011"  # scripted group (container) (typed FeaturePython)
  n = 0.01088
FEATURE [App::DocumentObjectGroupPython] G4_GEL_PHOTO_EMULSION  # scripted group (container) (typed FeaturePython)
  Dunit = g/cm3
  Dvalue = 1.2914
  Group = -> [H_element041,C_element048,N_element018,O_element042,S_element013]
  conduct = 2
  density = 1
  expand = 3
  formula = G4_GEL_PHOTO_EMULSION
  name = G4_GEL_PHOTO_EMULSION
  specific = 4
FEATURE [App::DocumentObjectGroupPython] B_element004  label="B_element : 0.040"  # scripted group (container) (typed FeaturePython)
  n = 0.0400639
FEATURE [App::DocumentObjectGroupPython] O_element043  label="O_element : 0.540"  # scripted group (container) (typed FeaturePython)
  n = 0.539561
FEATURE [App::DocumentObjectGroupPython] Na_element008  label="Na_element : 0.028"  # scripted group (container) (typed FeaturePython)
  n = 0.0281909
FEATURE [App::DocumentObjectGroupPython] Al_element003  label="Al_element : 0.012"  # scripted group (container) (typed FeaturePython)
  n = 0.011644
FEATURE [App::DocumentObjectGroupPython] Si_element003  label="Si_element : 0.377"  # scripted group (container) (typed FeaturePython)
  n = 0.377219
FEATURE [App::DocumentObjectGroupPython] K_element004  label="K_element : 0.014"  # scripted group (container) (typed FeaturePython)
  n = 0.00332099
FEATURE [App::DocumentObjectGroupPython] G4_Pyrex_Glass  # scripted group (container) (typed FeaturePython)
  Dunit = g/cm3
  Dvalue = 2.23
  Group = -> [B_element004,O_element043,Na_element008,Al_element003,Si_element003,K_element004]
  conduct = 2
  density = 1
  expand = 3
  formula = G4_Pyrex_Glass
  name = G4_Pyrex_Glass
  specific = 4
FEATURE [App::DocumentObjectGroupPython] O_element044  label="O_element : 0.156"  # scripted group (container) (typed FeaturePython)
  n = 0.156453
FEATURE [App::DocumentObjectGroupPython] Si_element004  label="Si_element : 0.081"  # scripted group (container) (typed FeaturePython)
  n = 0.080866
FEATURE [App::DocumentObjectGroupPython] Ti_element001  label="Ti_element : 0.008"  # scripted group (container) (typed FeaturePython)
  n = 0.008092
FEATURE [App::DocumentObjectGroupPython] As_element002  label="As_element : 0.003"  # scripted group (container) (typed FeaturePython)
  n = 0.002651
FEATURE [App::DocumentObjectGroupPython] Pb_element001  label="Pb_element : 0.752"  # scripted group (container) (typed FeaturePython)
  n = 0.751938
FEATURE [App::DocumentObjectGroupPython] G4_GLASS_LEAD  # scripted group (container) (typed FeaturePython)
  Dunit = g/cm3
  Dvalue = 6.22
  Group = -> [O_element044,Si_element004,Ti_element001,As_element002,Pb_element001]
  conduct = 2
  density = 1
  expand = 3
  formula = G4_GLASS_LEAD
  name = G4_GLASS_LEAD
  specific = 4
FEATURE [App::DocumentObjectGroupPython] O_element045  label="O_element : 0.460"  # scripted group (container) (typed FeaturePython)
  n = 0.4598
FEATURE [App::DocumentObjectGroupPython] Na_element009  label="Na_element : 0.096"  # scripted group (container) (typed FeaturePython)
  n = 0.0964411
FEATURE [App::DocumentObjectGroupPython] Si_element005  label="Si_element : 0.378"  # scripted group (container) (typed FeaturePython)
  n = 0.336553
FEATURE [App::DocumentObjectGroupPython] Ca_element011  label="Ca_element : 0.107"  # scripted group (container) (typed FeaturePython)
  n = 0.107205
FEATURE [App::DocumentObjectGroupPython] G4_GLASS_PLATE  # scripted group (container) (typed FeaturePython)
  Dunit = g/cm3
  Dvalue = 2.4
  Group = -> [O_element045,Na_element009,Si_element005,Ca_element011]
  conduct = 2
  density = 1
  expand = 3
  formula = G4_GLASS_PLATE
  name = G4_GLASS_PLATE
  specific = 4
FEATURE [App::DocumentObjectGroupPython] C_element049  label="C_element : 026"  # scripted group (container) (typed FeaturePython)
  n = 5
  ref = C_element
FEATURE [App::DocumentObjectGroupPython] H_element042  label="H_element : 021"  # scripted group (container) (typed FeaturePython)
  n = 10
  ref = H_element
FEATURE [App::DocumentObjectGroupPython] N_element019  label="N_element : 2"  # scripted group (container) (typed FeaturePython)
  n = 2
  ref = N_element
FEATURE [App::DocumentObjectGroupPython] O_element046  label="O_element : 022"  # scripted group (container) (typed FeaturePython)
  n = 3
  ref = O_element
FEATURE [App::DocumentObjectGroupPython] G4_GLUTAMINE  # scripted group (container) (typed FeaturePython)
  Dunit = g/cm3
  Dvalue = 1.46
  Group = -> [C_element049,H_element042,N_element019,O_element046]
  conduct = 2
  density = 1
  expand = 3
  formula = G4_GLUTAMINE
  name = G4_GLUTAMINE
  specific = 4
FEATURE [App::DocumentObjectGroupPython] C_element050  label="C_element : 027"  # scripted group (container) (typed FeaturePython)
  n = 3
  ref = C_element
FEATURE [App::DocumentObjectGroupPython] H_element043  label="H_element : 022"  # scripted group (container) (typed FeaturePython)
  n = 8
  ref = H_element
FEATURE [App::DocumentObjectGroupPython] O_element047  label="O_element : 023"  # scripted group (container) (typed FeaturePython)
  n = 3
  ref = O_element
FEATURE [App::DocumentObjectGroupPython] G4_GLYCEROL  # scripted group (container) (typed FeaturePython)
  Dunit = g/cm3
  Dvalue = 1.2613
  Group = -> [C_element050,H_element043,O_element047]
  conduct = 2
  density = 1
  expand = 3
  formula = G4_GLYCEROL
  name = G4_GLYCEROL
  specific = 4
FEATURE [App::DocumentObjectGroupPython] C_element051  label="C_element : 028"  # scripted group (container) (typed FeaturePython)
  n = 5
  ref = C_element
FEATURE [App::DocumentObjectGroupPython] H_element044  label="H_element : 023"  # scripted group (container) (typed FeaturePython)
  n = 5
  ref = H_element
FEATURE [App::DocumentObjectGroupPython] N_element020  label="N_element : 009"  # scripted group (container) (typed FeaturePython)
  n = 5
  ref = N_element
FEATURE [App::DocumentObjectGroupPython] O_element048  label="O_element : 024"  # scripted group (container) (typed FeaturePython)
  n = 1
  ref = O_element
FEATURE [App::DocumentObjectGroupPython] G4_GUANINE  # scripted group (container) (typed FeaturePython)
  Dunit = g/cm3
  Dvalue = 2.2
  Group = -> [C_element051,H_element044,N_element020,O_element048]
  conduct = 2
  density = 1
  expand = 3
  formula = G4_GUANINE
  name = G4_GUANINE
  specific = 4
FEATURE [App::DocumentObjectGroupPython] Ca_element012  label="Ca_element : 006"  # scripted group (container) (typed FeaturePython)
  n = 1
  ref = Ca_element
FEATURE [App::DocumentObjectGroupPython] S_element014  label="S_element : 005"  # scripted group (container) (typed FeaturePython)
  n = 1
  ref = S_element
FEATURE [App::DocumentObjectGroupPython] O_element049  label="O_element : 6"  # scripted group (container) (typed FeaturePython)
  n = 6
  ref = O_element
FEATURE [App::DocumentObjectGroupPython] H_element045  label="H_element : 024"  # scripted group (container) (typed FeaturePython)
  n = 4
  ref = H_element
FEATURE [App::DocumentObjectGroupPython] G4_GYPSUM  # scripted group (container) (typed FeaturePython)
  Dunit = g/cm3
  Dvalue = 2.32
  Group = -> [Ca_element012,S_element014,O_element049,H_element045]
  conduct = 2
  density = 1
  expand = 3
  formula = G4_GYPSUM
  name = G4_GYPSUM
  specific = 4
FEATURE [App::DocumentObjectGroupPython] C_element052  label="C_element : 7"  # scripted group (container) (typed FeaturePython)
  n = 7
  ref = C_element
FEATURE [App::DocumentObjectGroupPython] H_element046  label="H_element : 16"  # scripted group (container) (typed FeaturePython)
  n = 16
  ref = H_element
FEATURE [App::DocumentObjectGroupPython] G4_N_HEPTANE  label="G4_N-HEPTANE"  # scripted group (container) (typed FeaturePython)
  Dunit = g/cm3
  Dvalue = 0.68376
  Group = -> [C_element052,H_element046]
  conduct = 2
  density = 1
  expand = 3
  formula = G4_N-HEPTANE
  name = G4_N-HEPTANE
  specific = 4
FEATURE [App::DocumentObjectGroupPython] C_element053  label="C_element : 029"  # scripted group (container) (typed FeaturePython)
  n = 6
  ref = C_element
FEATURE [App::DocumentObjectGroupPython] H_element047  label="H_element : 14"  # scripted group (container) (typed FeaturePython)
  n = 14
  ref = H_element
FEATURE [App::DocumentObjectGroupPython] G4_N_HEXANE  label="G4_N-HEXANE"  # scripted group (container) (typed FeaturePython)
  Dunit = g/cm3
  Dvalue = 0.6603
  Group = -> [C_element053,H_element047]
  conduct = 2
  density = 1
  expand = 3
  formula = G4_N-HEXANE
  name = G4_N-HEXANE
  specific = 4
FEATURE [App::DocumentObjectGroupPython] C_element054  label="C_element : 22"  # scripted group (container) (typed FeaturePython)
  n = 22
  ref = C_element
FEATURE [App::DocumentObjectGroupPython] H_element048  label="H_element : 025"  # scripted group (container) (typed FeaturePython)
  n = 10
  ref = H_element
FEATURE [App::DocumentObjectGroupPython] N_element021  label="N_element : 010"  # scripted group (container) (typed FeaturePython)
  n = 2
  ref = N_element
FEATURE [App::DocumentObjectGroupPython] O_element050  label="O_element : 025"  # scripted group (container) (typed FeaturePython)
  n = 5
  ref = O_element
FEATURE [App::DocumentObjectGroupPython] G4_KAPTON  # scripted group (container) (typed FeaturePython)
  Dunit = g/cm3
  Dvalue = 1.42
  Group = -> [C_element054,H_element048,N_element021,O_element050]
  conduct = 2
  density = 1
  expand = 3
  formula = G4_KAPTON
  name = G4_KAPTON
  specific = 4
FEATURE [App::DocumentObjectGroupPython] La_element001  label="La_element : 1"  # scripted group (container) (typed FeaturePython)
  n = 1
  ref = La_element
FEATURE [App::DocumentObjectGroupPython] Br_element003  label="Br_element : 002"  # scripted group (container) (typed FeaturePython)
  n = 1
  ref = Br_element
FEATURE [App::DocumentObjectGroupPython] O_element051  label="O_element : 026"  # scripted group (container) (typed FeaturePython)
  n = 1
  ref = O_element
FEATURE [App::DocumentObjectGroupPython] G4_LANTHANUM_OXYBROMIDE  # scripted group (container) (typed FeaturePython)
  Dunit = g/cm3
  Dvalue = 6.28
  Group = -> [La_element001,Br_element003,O_element051]
  conduct = 2
  density = 1
  expand = 3
  formula = G4_LANTHANUM_OXYBROMIDE
  name = G4_LANTHANUM_OXYBROMIDE
  specific = 4
FEATURE [App::DocumentObjectGroupPython] La_element002  label="La_element : 2"  # scripted group (container) (typed FeaturePython)
  n = 2
  ref = La_element
FEATURE [App::DocumentObjectGroupPython] O_element052  label="O_element : 027"  # scripted group (container) (typed FeaturePython)
  n = 2
  ref = O_element
FEATURE [App::DocumentObjectGroupPython] S_element015  label="S_element : 006"  # scripted group (container) (typed FeaturePython)
  n = 1
  ref = S_element
FEATURE [App::DocumentObjectGroupPython] G4_LANTHANUM_OXYSULFIDE  # scripted group (container) (typed FeaturePython)
  Dunit = g/cm3
  Dvalue = 5.86
  Group = -> [La_element002,O_element052,S_element015]
  conduct = 2
  density = 1
  expand = 3
  formula = G4_LANTHANUM_OXYSULFIDE
  name = G4_LANTHANUM_OXYSULFIDE
  specific = 4
FEATURE [App::DocumentObjectGroupPython] O_element053  label="O_element : 0.072"  # scripted group (container) (typed FeaturePython)
  n = 0.071682
FEATURE [App::DocumentObjectGroupPython] Pb_element002  label="Pb_element : 0.928"  # scripted group (container) (typed FeaturePython)
  n = 0.928318
FEATURE [App::DocumentObjectGroupPython] G4_LEAD_OXIDE  # scripted group (container) (typed FeaturePython)
  Dunit = g/cm3
  Dvalue = 9.53
  Group = -> [O_element053,Pb_element002]
  conduct = 2
  density = 1
  expand = 3
  formula = G4_LEAD_OXIDE
  name = G4_LEAD_OXIDE
  specific = 4
FEATURE [App::DocumentObjectGroupPython] Li_element001  label="Li_element : 1"  # scripted group (container) (typed FeaturePython)
  n = 1
  ref = Li_element
FEATURE [App::DocumentObjectGroupPython] N_element022  label="N_element : 011"  # scripted group (container) (typed FeaturePython)
  n = 1
  ref = N_element
FEATURE [App::DocumentObjectGroupPython] H_element049  label="H_element : 026"  # scripted group (container) (typed FeaturePython)
  n = 2
  ref = H_element
FEATURE [App::DocumentObjectGroupPython] G4_LITHIUM_AMIDE  # scripted group (container) (typed FeaturePython)
  Dunit = g/cm3
  Dvalue = 1.178
  Group = -> [Li_element001,N_element022,H_element049]
  conduct = 2
  density = 1
  expand = 3
  formula = G4_LITHIUM_AMIDE
  name = G4_LITHIUM_AMIDE
  specific = 4
FEATURE [App::DocumentObjectGroupPython] Li_element002  label="Li_element : 2"  # scripted group (container) (typed FeaturePython)
  n = 2
  ref = Li_element
FEATURE [App::DocumentObjectGroupPython] C_element055  label="C_element : 030"  # scripted group (container) (typed FeaturePython)
  n = 1
  ref = C_element
FEATURE [App::DocumentObjectGroupPython] O_element054  label="O_element : 028"  # scripted group (container) (typed FeaturePython)
  n = 3
  ref = O_element
FEATURE [App::DocumentObjectGroupPython] G4_LITHIUM_CARBONATE  # scripted group (container) (typed FeaturePython)
  Dunit = g/cm3
  Dvalue = 2.11
  Group = -> [Li_element002,C_element055,O_element054]
  conduct = 2
  density = 1
  expand = 3
  formula = G4_LITHIUM_CARBONATE
  name = G4_LITHIUM_CARBONATE
  specific = 4
FEATURE [App::DocumentObjectGroupPython] Li_element003  label="Li_element : 003"  # scripted group (container) (typed FeaturePython)
  n = 1
  ref = Li_element
FEATURE [App::DocumentObjectGroupPython] F_element012  label="F_element : 004"  # scripted group (container) (typed FeaturePython)
  n = 1
  ref = F_element
FEATURE [App::DocumentObjectGroupPython] G4_LITHIUM_FLUORIDE  # scripted group (container) (typed FeaturePython)
  Dunit = g/cm3
  Dvalue = 2.635
  Group = -> [Li_element003,F_element012]
  conduct = 2
  density = 1
  expand = 3
  formula = G4_LITHIUM_FLUORIDE
  name = G4_LITHIUM_FLUORIDE
  specific = 4
FEATURE [App::DocumentObjectGroupPython] Li_element004  label="Li_element : 004"  # scripted group (container) (typed FeaturePython)
  n = 1
  ref = Li_element
FEATURE [App::DocumentObjectGroupPython] H_element050  label="H_element : 027"  # scripted group (container) (typed FeaturePython)
  n = 1
  ref = H_element
FEATURE [App::DocumentObjectGroupPython] G4_LITHIUM_HYDRIDE  # scripted group (container) (typed FeaturePython)
  Dunit = g/cm3
  Dvalue = 0.82
  Group = -> [Li_element004,H_element050]
  conduct = 2
  density = 1
  expand = 3
  formula = G4_LITHIUM_HYDRIDE
  name = G4_LITHIUM_HYDRIDE
  specific = 4
FEATURE [App::DocumentObjectGroupPython] Li_element005  label="Li_element : 005"  # scripted group (container) (typed FeaturePython)
  n = 1
  ref = Li_element
FEATURE [App::DocumentObjectGroupPython] I_element003  label="I_element : 002"  # scripted group (container) (typed FeaturePython)
  n = 1
  ref = I_element
FEATURE [App::DocumentObjectGroupPython] G4_LITHIUM_IODIDE  # scripted group (container) (typed FeaturePython)
  Dunit = g/cm3
  Dvalue = 3.494
  Group = -> [Li_element005,I_element003]
  conduct = 2
  density = 1
  expand = 3
  formula = G4_LITHIUM_IODIDE
  name = G4_LITHIUM_IODIDE
  specific = 4
FEATURE [App::DocumentObjectGroupPython] Li_element006  label="Li_element : 006"  # scripted group (container) (typed FeaturePython)
  n = 2
  ref = Li_element
FEATURE [App::DocumentObjectGroupPython] O_element055  label="O_element : 029"  # scripted group (container) (typed FeaturePython)
  n = 1
  ref = O_element
FEATURE [App::DocumentObjectGroupPython] G4_LITHIUM_OXIDE  # scripted group (container) (typed FeaturePython)
  Dunit = g/cm3
  Dvalue = 2.013
  Group = -> [Li_element006,O_element055]
  conduct = 2
  density = 1
  expand = 3
  formula = G4_LITHIUM_OXIDE
  name = G4_LITHIUM_OXIDE
  specific = 4
FEATURE [App::DocumentObjectGroupPython] Li_element007  label="Li_element : 007"  # scripted group (container) (typed FeaturePython)
  n = 2
  ref = Li_element
FEATURE [App::DocumentObjectGroupPython] B_element005  label="B_element : 005"  # scripted group (container) (typed FeaturePython)
  n = 4
  ref = B_element
FEATURE [App::DocumentObjectGroupPython] O_element056  label="O_element : 7"  # scripted group (container) (typed FeaturePython)
  n = 7
  ref = O_element
FEATURE [App::DocumentObjectGroupPython] G4_LITHIUM_TETRABORATE  # scripted group (container) (typed FeaturePython)
  Dunit = g/cm3
  Dvalue = 2.44
  Group = -> [Li_element007,B_element005,O_element056]
  conduct = 2
  density = 1
  expand = 3
  formula = G4_LITHIUM_TETRABORATE
  name = G4_LITHIUM_TETRABORATE
  specific = 4
FEATURE [App::DocumentObjectGroupPython] H_element051  label="H_element : 0.105"  # scripted group (container) (typed FeaturePython)
  n = 0.105
FEATURE [App::DocumentObjectGroupPython] C_element056  label="C_element : 0.083"  # scripted group (container) (typed FeaturePython)
  n = 0.083
FEATURE [App::DocumentObjectGroupPython] N_element023  label="N_element : 0.023"  # scripted group (container) (typed FeaturePython)
  n = 0.023
FEATURE [App::DocumentObjectGroupPython] O_element057  label="O_element : 0.779"  # scripted group (container) (typed FeaturePython)
  n = 0.779
FEATURE [App::DocumentObjectGroupPython] Na_element010  label="Na_element : 0.097"  # scripted group (container) (typed FeaturePython)
  n = 0.002
FEATURE [App::DocumentObjectGroupPython] P_element006  label="P_element : 0.105"  # scripted group (container) (typed FeaturePython)
  n = 0.001
FEATURE [App::DocumentObjectGroupPython] S_element016  label="S_element : 0.017"  # scripted group (container) (typed FeaturePython)
  n = 0.002
FEATURE [App::DocumentObjectGroupPython] Cl_element014  label="Cl_element : 0.587"  # scripted group (container) (typed FeaturePython)
  n = 0.003
FEATURE [App::DocumentObjectGroupPython] K_element005  label="K_element : 0.015"  # scripted group (container) (typed FeaturePython)
  n = 0.002
FEATURE [App::DocumentObjectGroupPython] G4_LUNG_ICRP  # scripted group (container) (typed FeaturePython)
  Dunit = g/cm3
  Dvalue = 1.04
  Group = -> [H_element051,C_element056,N_element023,O_element057,Na_element010,P_element006,S_element016,Cl_element014,K_element005]
  conduct = 2
  density = 1
  expand = 3
  formula = G4_LUNG_ICRP
  name = G4_LUNG_ICRP
  specific = 4
FEATURE [App::DocumentObjectGroupPython] H_element052  label="H_element : 0.116"  # scripted group (container) (typed FeaturePython)
  n = 0.114318
FEATURE [App::DocumentObjectGroupPython] C_element057  label="C_element : 0.656"  # scripted group (container) (typed FeaturePython)
  n = 0.655824
FEATURE [App::DocumentObjectGroupPython] O_element058  label="O_element : 0.092"  # scripted group (container) (typed FeaturePython)
  n = 0.0921831
FEATURE [App::DocumentObjectGroupPython] Mg_element004  label="Mg_element : 0.135"  # scripted group (container) (typed FeaturePython)
  n = 0.134792
FEATURE [App::DocumentObjectGroupPython] Ca_element013  label="Ca_element : 0.003"  # scripted group (container) (typed FeaturePython)
  n = 0.002883
FEATURE [App::DocumentObjectGroupPython] G4_M3_WAX  # scripted group (container) (typed FeaturePython)
  Dunit = g/cm3
  Dvalue = 1.05
  Group = -> [H_element052,C_element057,O_element058,Mg_element004,Ca_element013]
  conduct = 2
  density = 1
  expand = 3
  formula = G4_M3_WAX
  name = G4_M3_WAX
  specific = 4
FEATURE [App::DocumentObjectGroupPython] Mg_element005  label="Mg_element : 1"  # scripted group (container) (typed FeaturePython)
  n = 1
  ref = Mg_element
FEATURE [App::DocumentObjectGroupPython] C_element058  label="C_element : 031"  # scripted group (container) (typed FeaturePython)
  n = 1
  ref = C_element
FEATURE [App::DocumentObjectGroupPython] O_element059  label="O_element : 030"  # scripted group (container) (typed FeaturePython)
  n = 3
  ref = O_element
FEATURE [App::DocumentObjectGroupPython] G4_MAGNESIUM_CARBONATE  # scripted group (container) (typed FeaturePython)
  Dunit = g/cm3
  Dvalue = 2.958
  Group = -> [Mg_element005,C_element058,O_element059]
  conduct = 2
  density = 1
  expand = 3
  formula = G4_MAGNESIUM_CARBONATE
  name = G4_MAGNESIUM_CARBONATE
  specific = 4
FEATURE [App::DocumentObjectGroupPython] Mg_element006  label="Mg_element : 002"  # scripted group (container) (typed FeaturePython)
  n = 1
  ref = Mg_element
FEATURE [App::DocumentObjectGroupPython] F_element013  label="F_element : 005"  # scripted group (container) (typed FeaturePython)
  n = 2
  ref = F_element
FEATURE [App::DocumentObjectGroupPython] G4_MAGNESIUM_FLUORIDE  # scripted group (container) (typed FeaturePython)
  Dunit = g/cm3
  Dvalue = 3
  Group = -> [Mg_element006,F_element013]
  conduct = 2
  density = 1
  expand = 3
  formula = G4_MAGNESIUM_FLUORIDE
  name = G4_MAGNESIUM_FLUORIDE
  specific = 4
FEATURE [App::DocumentObjectGroupPython] Mg_element007  label="Mg_element : 003"  # scripted group (container) (typed FeaturePython)
  n = 1
  ref = Mg_element
FEATURE [App::DocumentObjectGroupPython] O_element060  label="O_element : 031"  # scripted group (container) (typed FeaturePython)
  n = 1
  ref = O_element
FEATURE [App::DocumentObjectGroupPython] G4_MAGNESIUM_OXIDE  # scripted group (container) (typed FeaturePython)
  Dunit = g/cm3
  Dvalue = 3.58
  Group = -> [Mg_element007,O_element060]
  conduct = 2
  density = 1
  expand = 3
  formula = G4_MAGNESIUM_OXIDE
  name = G4_MAGNESIUM_OXIDE
  specific = 4
FEATURE [App::DocumentObjectGroupPython] Mg_element008  label="Mg_element : 004"  # scripted group (container) (typed FeaturePython)
  n = 1
  ref = Mg_element
FEATURE [App::DocumentObjectGroupPython] B_element006  label="B_element : 006"  # scripted group (container) (typed FeaturePython)
  n = 4
  ref = B_element
FEATURE [App::DocumentObjectGroupPython] O_element061  label="O_element : 032"  # scripted group (container) (typed FeaturePython)
  n = 7
  ref = O_element
FEATURE [App::DocumentObjectGroupPython] G4_MAGNESIUM_TETRABORATE  # scripted group (container) (typed FeaturePython)
  Dunit = g/cm3
  Dvalue = 2.53
  Group = -> [Mg_element008,B_element006,O_element061]
  conduct = 2
  density = 1
  expand = 3
  formula = G4_MAGNESIUM_TETRABORATE
  name = G4_MAGNESIUM_TETRABORATE
  specific = 4
FEATURE [App::DocumentObjectGroupPython] Hg_element001  label="Hg_element : 1"  # scripted group (container) (typed FeaturePython)
  n = 1
  ref = Hg_element
FEATURE [App::DocumentObjectGroupPython] I_element004  label="I_element : 2"  # scripted group (container) (typed FeaturePython)
  n = 2
  ref = I_element
FEATURE [App::DocumentObjectGroupPython] G4_MERCURIC_IODIDE  # scripted group (container) (typed FeaturePython)
  Dunit = g/cm3
  Dvalue = 6.36
  Group = -> [Hg_element001,I_element004]
  conduct = 2
  density = 1
  expand = 3
  formula = G4_MERCURIC_IODIDE
  name = G4_MERCURIC_IODIDE
  specific = 4
FEATURE [App::DocumentObjectGroupPython] C_element059  label="C_element : 032"  # scripted group (container) (typed FeaturePython)
  n = 1
  ref = C_element
FEATURE [App::DocumentObjectGroupPython] H_element053  label="H_element : 028"  # scripted group (container) (typed FeaturePython)
  n = 4
  ref = H_element
FEATURE [App::DocumentObjectGroupPython] G4_METHANE  # scripted group (container) (typed FeaturePython)
  Dunit = g/cm3
  Dvalue = 0.000667151
  Group = -> [C_element059,H_element053]
  conduct = 2
  density = 1
  expand = 3
  formula = G4_METHANE
  name = G4_METHANE
  specific = 4
FEATURE [App::DocumentObjectGroupPython] C_element060  label="C_element : 033"  # scripted group (container) (typed FeaturePython)
  n = 1
  ref = C_element
FEATURE [App::DocumentObjectGroupPython] H_element054  label="H_element : 029"  # scripted group (container) (typed FeaturePython)
  n = 4
  ref = H_element
FEATURE [App::DocumentObjectGroupPython] O_element062  label="O_element : 033"  # scripted group (container) (typed FeaturePython)
  n = 1
  ref = O_element
FEATURE [App::DocumentObjectGroupPython] G4_METHANOL  # scripted group (container) (typed FeaturePython)
  Dunit = g/cm3
  Dvalue = 0.7914
  Group = -> [C_element060,H_element054,O_element062]
  conduct = 2
  density = 1
  expand = 3
  formula = G4_METHANOL
  name = G4_METHANOL
  specific = 4
FEATURE [App::DocumentObjectGroupPython] H_element055  label="H_element : 0.134"  # scripted group (container) (typed FeaturePython)
  n = 0.13404
FEATURE [App::DocumentObjectGroupPython] C_element061  label="C_element : 0.778"  # scripted group (container) (typed FeaturePython)
  n = 0.77796
FEATURE [App::DocumentObjectGroupPython] O_element063  label="O_element : 0.035"  # scripted group (container) (typed FeaturePython)
  n = 0.03502
FEATURE [App::DocumentObjectGroupPython] Mg_element009  label="Mg_element : 0.039"  # scripted group (container) (typed FeaturePython)
  n = 0.038594
FEATURE [App::DocumentObjectGroupPython] Ti_element002  label="Ti_element : 0.014"  # scripted group (container) (typed FeaturePython)
  n = 0.014386
FEATURE [App::DocumentObjectGroupPython] G4_MIX_D_WAX  # scripted group (container) (typed FeaturePython)
  Dunit = g/cm3
  Dvalue = 0.99
  Group = -> [H_element055,C_element061,O_element063,Mg_element009,Ti_element002]
  conduct = 2
  density = 1
  expand = 3
  formula = G4_MIX_D_WAX
  name = G4_MIX_D_WAX
  specific = 4
FEATURE [App::DocumentObjectGroupPython] H_element056  label="H_element : 0.135"  # scripted group (container) (typed FeaturePython)
  n = 0.081192
FEATURE [App::DocumentObjectGroupPython] C_element062  label="C_element : 0.583"  # scripted group (container) (typed FeaturePython)
  n = 0.583442
FEATURE [App::DocumentObjectGroupPython] N_element024  label="N_element : 0.018"  # scripted group (container) (typed FeaturePython)
  n = 0.017798
FEATURE [App::DocumentObjectGroupPython] O_element064  label="O_element : 0.186"  # scripted group (container) (typed FeaturePython)
  n = 0.186381
FEATURE [App::DocumentObjectGroupPython] Mg_element010  label="Mg_element : 0.130"  # scripted group (container) (typed FeaturePython)
  n = 0.130287
FEATURE [App::DocumentObjectGroupPython] Cl_element015  label="Cl_element : 0.588"  # scripted group (container) (typed FeaturePython)
  n = 0.0009
FEATURE [App::DocumentObjectGroupPython] G4_MS20_TISSUE  # scripted group (container) (typed FeaturePython)
  Dunit = g/cm3
  Dvalue = 1
  Group = -> [H_element056,C_element062,N_element024,O_element064,Mg_element010,Cl_element015]
  conduct = 2
  density = 1
  expand = 3
  formula = G4_MS20_TISSUE
  name = G4_MS20_TISSUE
  specific = 4
FEATURE [App::DocumentObjectGroupPython] H_element057  label="H_element : 0.136"  # scripted group (container) (typed FeaturePython)
  n = 0.102
FEATURE [App::DocumentObjectGroupPython] C_element063  label="C_element : 0.143"  # scripted group (container) (typed FeaturePython)
  n = 0.143
FEATURE [App::DocumentObjectGroupPython] N_element025  label="N_element : 0.034"  # scripted group (container) (typed FeaturePython)
  n = 0.034
FEATURE [App::DocumentObjectGroupPython] O_element065  label="O_element : 0.710"  # scripted group (container) (typed FeaturePython)
  n = 0.71
FEATURE [App::DocumentObjectGroupPython] Na_element011  label="Na_element : 0.098"  # scripted group (container) (typed FeaturePython)
  n = 0.001
FEATURE [App::DocumentObjectGroupPython] P_element007  label="P_element : 0.002"  # scripted group (container) (typed FeaturePython)
  n = 0.002
FEATURE [App::DocumentObjectGroupPython] S_element017  label="S_element : 0.018"  # scripted group (container) (typed FeaturePython)
  n = 0.003
FEATURE [App::DocumentObjectGroupPython] Cl_element016  label="Cl_element : 0.589"  # scripted group (container) (typed FeaturePython)
  n = 0.001
FEATURE [App::DocumentObjectGroupPython] K_element006  label="K_element : 0.004"  # scripted group (container) (typed FeaturePython)
  n = 0.004
FEATURE [App::DocumentObjectGroupPython] G4_MUSCLE_SKELETAL_ICRP  # scripted group (container) (typed FeaturePython)
  Dunit = g/cm3
  Dvalue = 1.05
  Group = -> [H_element057,C_element063,N_element025,O_element065,Na_element011,P_element007,S_element017,Cl_element016,K_element006]
  conduct = 2
  density = 1
  expand = 3
  formula = G4_MUSCLE_SKELETAL_ICRP
  name = G4_MUSCLE_SKELETAL_ICRP
  specific = 4
FEATURE [App::DocumentObjectGroupPython] H_element058  label="H_element : 0.137"  # scripted group (container) (typed FeaturePython)
  n = 0.102102
FEATURE [App::DocumentObjectGroupPython] C_element064  label="C_element : 0.123"  # scripted group (container) (typed FeaturePython)
  n = 0.123123
FEATURE [App::DocumentObjectGroupPython] N_element026  label="N_element : 0.756"  # scripted group (container) (typed FeaturePython)
  n = 0.035035
FEATURE [App::DocumentObjectGroupPython] O_element066  label="O_element : 0.730"  # scripted group (container) (typed FeaturePython)
  n = 0.72973
FEATURE [App::DocumentObjectGroupPython] Na_element012  label="Na_element : 0.099"  # scripted group (container) (typed FeaturePython)
  n = 0.001001
FEATURE [App::DocumentObjectGroupPython] P_element008  label="P_element : 0.106"  # scripted group (container) (typed FeaturePython)
  n = 0.002002
FEATURE [App::DocumentObjectGroupPython] S_element018  label="S_element : 0.019"  # scripted group (container) (typed FeaturePython)
  n = 0.004004
FEATURE [App::DocumentObjectGroupPython] K_element007  label="K_element : 0.016"  # scripted group (container) (typed FeaturePython)
  n = 0.003003
FEATURE [App::DocumentObjectGroupPython] G4_MUSCLE_STRIATED_ICRU  # scripted group (container) (typed FeaturePython)
  Dunit = g/cm3
  Dvalue = 1.04
  Group = -> [H_element058,C_element064,N_element026,O_element066,Na_element012,P_element008,S_element018,K_element007]
  conduct = 2
  density = 1
  expand = 3
  formula = G4_MUSCLE_STRIATED_ICRU
  name = G4_MUSCLE_STRIATED_ICRU
  specific = 4
FEATURE [App::DocumentObjectGroupPython] H_element059  label="H_element : 0.098"  # scripted group (container) (typed FeaturePython)
  n = 0.0982341
FEATURE [App::DocumentObjectGroupPython] C_element065  label="C_element : 0.156"  # scripted group (container) (typed FeaturePython)
  n = 0.156214
FEATURE [App::DocumentObjectGroupPython] N_element027  label="N_element : 0.757"  # scripted group (container) (typed FeaturePython)
  n = 0.035451
FEATURE [App::DocumentObjectGroupPython] O_element067  label="O_element : 0.880"  # scripted group (container) (typed FeaturePython)
  n = 0.710101
FEATURE [App::DocumentObjectGroupPython] G4_MUSCLE_WITH_SUCROSE  # scripted group (container) (typed FeaturePython)
  Dunit = g/cm3
  Dvalue = 1.11
  Group = -> [H_element059,C_element065,N_element027,O_element067]
  conduct = 2
  density = 1
  expand = 3
  formula = G4_MUSCLE_WITH_SUCROSE
  name = G4_MUSCLE_WITH_SUCROSE
  specific = 4
FEATURE [App::DocumentObjectGroupPython] H_element060  label="H_element : 0.138"  # scripted group (container) (typed FeaturePython)
  n = 0.101969
FEATURE [App::DocumentObjectGroupPython] C_element066  label="C_element : 0.120"  # scripted group (container) (typed FeaturePython)
  n = 0.120058
FEATURE [App::DocumentObjectGroupPython] N_element028  label="N_element : 0.758"  # scripted group (container) (typed FeaturePython)
  n = 0.035451
FEATURE [App::DocumentObjectGroupPython] O_element068  label="O_element : 0.743"  # scripted group (container) (typed FeaturePython)
  n = 0.742522
FEATURE [App::DocumentObjectGroupPython] G4_MUSCLE_WITHOUT_SUCROSE  # scripted group (container) (typed FeaturePython)
  Dunit = g/cm3
  Dvalue = 1.07
  Group = -> [H_element060,C_element066,N_element028,O_element068]
  conduct = 2
  density = 1
  expand = 3
  formula = G4_MUSCLE_WITHOUT_SUCROSE
  name = G4_MUSCLE_WITHOUT_SUCROSE
  specific = 4
FEATURE [App::DocumentObjectGroupPython] C_element067  label="C_element : 10"  # scripted group (container) (typed FeaturePython)
  n = 10
  ref = C_element
FEATURE [App::DocumentObjectGroupPython] H_element061  label="H_element : 030"  # scripted group (container) (typed FeaturePython)
  n = 8
  ref = H_element
FEATURE [App::DocumentObjectGroupPython] G4_NAPHTHALENE  # scripted group (container) (typed FeaturePython)
  Dunit = g/cm3
  Dvalue = 1.145
  Group = -> [C_element067,H_element061]
  conduct = 2
  density = 1
  expand = 3
  formula = G4_NAPHTHALENE
  name = G4_NAPHTHALENE
  specific = 4
FEATURE [App::DocumentObjectGroupPython] C_element068  label="C_element : 034"  # scripted group (container) (typed FeaturePython)
  n = 6
  ref = C_element
FEATURE [App::DocumentObjectGroupPython] H_element062  label="H_element : 031"  # scripted group (container) (typed FeaturePython)
  n = 5
  ref = H_element
FEATURE [App::DocumentObjectGroupPython] N_element029  label="N_element : 012"  # scripted group (container) (typed FeaturePython)
  n = 1
  ref = N_element
FEATURE [App::DocumentObjectGroupPython] O_element069  label="O_element : 034"  # scripted group (container) (typed FeaturePython)
  n = 2
  ref = O_element
FEATURE [App::DocumentObjectGroupPython] G4_NITROBENZENE  # scripted group (container) (typed FeaturePython)
  Dunit = g/cm3
  Dvalue = 1.19867
  Group = -> [C_element068,H_element062,N_element029,O_element069]
  conduct = 2
  density = 1
  expand = 3
  formula = G4_NITROBENZENE
  name = G4_NITROBENZENE
  specific = 4
FEATURE [App::DocumentObjectGroupPython] N_element030  label="N_element : 013"  # scripted group (container) (typed FeaturePython)
  n = 2
  ref = N_element
FEATURE [App::DocumentObjectGroupPython] O_element070  label="O_element : 035"  # scripted group (container) (typed FeaturePython)
  n = 1
  ref = O_element
FEATURE [App::DocumentObjectGroupPython] G4_NITROUS_OXIDE  # scripted group (container) (typed FeaturePython)
  Dunit = g/cm3
  Dvalue = 0.00183094
  Group = -> [N_element030,O_element070]
  conduct = 2
  density = 1
  expand = 3
  formula = G4_NITROUS_OXIDE
  name = G4_NITROUS_OXIDE
  specific = 4
FEATURE [App::DocumentObjectGroupPython] H_element063  label="H_element : 0.104"  # scripted group (container) (typed FeaturePython)
  n = 0.103509
FEATURE [App::DocumentObjectGroupPython] C_element069  label="C_element : 0.648"  # scripted group (container) (typed FeaturePython)
  n = 0.648416
FEATURE [App::DocumentObjectGroupPython] N_element031  label="N_element : 0.100"  # scripted group (container) (typed FeaturePython)
  n = 0.0995361
FEATURE [App::DocumentObjectGroupPython] O_element071  label="O_element : 0.149"  # scripted group (container) (typed FeaturePython)
  n = 0.148539
FEATURE [App::DocumentObjectGroupPython] G4_NYLON_8062  label="G4_NYLON-8062"  # scripted group (container) (typed FeaturePython)
  Dunit = g/cm3
  Dvalue = 1.08
  Group = -> [H_element063,C_element069,N_element031,O_element071]
  conduct = 2
  density = 1
  expand = 3
  formula = G4_NYLON-8062
  name = G4_NYLON-8062
  specific = 4
FEATURE [App::DocumentObjectGroupPython] C_element070  label="C_element : 035"  # scripted group (container) (typed FeaturePython)
  n = 6
  ref = C_element
FEATURE [App::DocumentObjectGroupPython] H_element064  label="H_element : 11"  # scripted group (container) (typed FeaturePython)
  n = 11
  ref = H_element
FEATURE [App::DocumentObjectGroupPython] N_element032  label="N_element : 014"  # scripted group (container) (typed FeaturePython)
  n = 1
  ref = N_element
FEATURE [App::DocumentObjectGroupPython] O_element072  label="O_element : 036"  # scripted group (container) (typed FeaturePython)
  n = 1
  ref = O_element
FEATURE [App::DocumentObjectGroupPython] G4_NYLON_6_6  label="G4_NYLON-6-6"  # scripted group (container) (typed FeaturePython)
  Dunit = g/cm3
  Dvalue = 1.14
  Group = -> [C_element070,H_element064,N_element032,O_element072]
  conduct = 2
  density = 1
  expand = 3
  formula = G4_NYLON-6-6
  name = G4_NYLON-6-6
  specific = 4
FEATURE [App::DocumentObjectGroupPython] H_element065  label="H_element : 0.139"  # scripted group (container) (typed FeaturePython)
  n = 0.107062
FEATURE [App::DocumentObjectGroupPython] C_element071  label="C_element : 0.680"  # scripted group (container) (typed FeaturePython)
  n = 0.680449
FEATURE [App::DocumentObjectGroupPython] N_element033  label="N_element : 0.099"  # scripted group (container) (typed FeaturePython)
  n = 0.099189
FEATURE [App::DocumentObjectGroupPython] O_element073  label="O_element : 0.113"  # scripted group (container) (typed FeaturePython)
  n = 0.1133
FEATURE [App::DocumentObjectGroupPython] G4_NYLON_6_10  label="G4_NYLON-6-10"  # scripted group (container) (typed FeaturePython)
  Dunit = g/cm3
  Dvalue = 1.14
  Group = -> [H_element065,C_element071,N_element033,O_element073]
  conduct = 2
  density = 1
  expand = 3
  formula = G4_NYLON-6-10
  name = G4_NYLON-6-10
  specific = 4
FEATURE [App::DocumentObjectGroupPython] H_element066  label="H_element : 0.140"  # scripted group (container) (typed FeaturePython)
  n = 0.115476
FEATURE [App::DocumentObjectGroupPython] C_element072  label="C_element : 0.721"  # scripted group (container) (typed FeaturePython)
  n = 0.720818
FEATURE [App::DocumentObjectGroupPython] N_element034  label="N_element : 0.076"  # scripted group (container) (typed FeaturePython)
  n = 0.0764169
FEATURE [App::DocumentObjectGroupPython] O_element074  label="O_element : 0.087"  # scripted group (container) (typed FeaturePython)
  n = 0.0872889
FEATURE [App::DocumentObjectGroupPython] G4_NYLON_11_RILSAN  label="G4_NYLON-11_RILSAN"  # scripted group (container) (typed FeaturePython)
  Dunit = g/cm3
  Dvalue = 1.425
  Group = -> [H_element066,C_element072,N_element034,O_element074]
  conduct = 2
  density = 1
  expand = 3
  formula = G4_NYLON-11_RILSAN
  name = G4_NYLON-11_RILSAN
  specific = 4
FEATURE [App::DocumentObjectGroupPython] C_element073  label="C_element : 8"  # scripted group (container) (typed FeaturePython)
  n = 8
  ref = C_element
FEATURE [App::DocumentObjectGroupPython] H_element067  label="H_element : 18"  # scripted group (container) (typed FeaturePython)
  n = 18
  ref = H_element
FEATURE [App::DocumentObjectGroupPython] G4_OCTANE  # scripted group (container) (typed FeaturePython)
  Dunit = g/cm3
  Dvalue = 0.7026
  Group = -> [C_element073,H_element067]
  conduct = 2
  density = 1
  expand = 3
  formula = G4_OCTANE
  name = G4_OCTANE
  specific = 4
FEATURE [App::DocumentObjectGroupPython] C_element074  label="C_element : 25"  # scripted group (container) (typed FeaturePython)
  n = 25
  ref = C_element
FEATURE [App::DocumentObjectGroupPython] H_element068  label="H_element : 52"  # scripted group (container) (typed FeaturePython)
  n = 52
  ref = H_element
FEATURE [App::DocumentObjectGroupPython] G4_PARAFFIN  # scripted group (container) (typed FeaturePython)
  Dunit = g/cm3
  Dvalue = 0.93
  Group = -> [C_element074,H_element068]
  conduct = 2
  density = 1
  expand = 3
  formula = G4_PARAFFIN
  name = G4_PARAFFIN
  specific = 4
FEATURE [App::DocumentObjectGroupPython] C_element075  label="C_element : 036"  # scripted group (container) (typed FeaturePython)
  n = 5
  ref = C_element
FEATURE [App::DocumentObjectGroupPython] H_element069  label="H_element : 032"  # scripted group (container) (typed FeaturePython)
  n = 12
  ref = H_element
FEATURE [App::DocumentObjectGroupPython] G4_N_PENTANE  label="G4_N-PENTANE"  # scripted group (container) (typed FeaturePython)
  Dunit = g/cm3
  Dvalue = 0.6262
  Group = -> [C_element075,H_element069]
  conduct = 2
  density = 1
  expand = 3
  formula = G4_N-PENTANE
  name = G4_N-PENTANE
  specific = 4
FEATURE [App::DocumentObjectGroupPython] H_element070  label="H_element : 0.014"  # scripted group (container) (typed FeaturePython)
  n = 0.0141
FEATURE [App::DocumentObjectGroupPython] C_element076  label="C_element : 0.072"  # scripted group (container) (typed FeaturePython)
  n = 0.072261
FEATURE [App::DocumentObjectGroupPython] N_element035  label="N_element : 0.019"  # scripted group (container) (typed FeaturePython)
  n = 0.01932
FEATURE [App::DocumentObjectGroupPython] O_element075  label="O_element : 0.066"  # scripted group (container) (typed FeaturePython)
  n = 0.066101
FEATURE [App::DocumentObjectGroupPython] S_element019  label="S_element : 0.020"  # scripted group (container) (typed FeaturePython)
  n = 0.00189
FEATURE [App::DocumentObjectGroupPython] Br_element004  label="Br_element : 0.349"  # scripted group (container) (typed FeaturePython)
  n = 0.349103
FEATURE [App::DocumentObjectGroupPython] Ag_element001  label="Ag_element : 0.474"  # scripted group (container) (typed FeaturePython)
  n = 0.474105
FEATURE [App::DocumentObjectGroupPython] I_element005  label="I_element : 0.003"  # scripted group (container) (typed FeaturePython)
  n = 0.00312
FEATURE [App::DocumentObjectGroupPython] G4_PHOTO_EMULSION  # scripted group (container) (typed FeaturePython)
  Dunit = g/cm3
  Dvalue = 3.815
  Group = -> [H_element070,C_element076,N_element035,O_element075,S_element019,Br_element004,Ag_element001,I_element005]
  conduct = 2
  density = 1
  expand = 3
  formula = G4_PHOTO_EMULSION
  name = G4_PHOTO_EMULSION
  specific = 4
FEATURE [App::DocumentObjectGroupPython] C_element077  label="C_element : 9"  # scripted group (container) (typed FeaturePython)
  n = 9
  ref = C_element
FEATURE [App::DocumentObjectGroupPython] H_element071  label="H_element : 033"  # scripted group (container) (typed FeaturePython)
  n = 10
  ref = H_element
FEATURE [App::DocumentObjectGroupPython] G4_PLASTIC_SC_VINYLTOLUENE  # scripted group (container) (typed FeaturePython)
  Dunit = g/cm3
  Dvalue = 1.032
  Group = -> [C_element077,H_element071]
  conduct = 2
  density = 1
  expand = 3
  formula = G4_PLASTIC_SC_VINYLTOLUENE
  name = G4_PLASTIC_SC_VINYLTOLUENE
  specific = 4
FEATURE [App::DocumentObjectGroupPython] Pu_element001  label="Pu_element : 1"  # scripted group (container) (typed FeaturePython)
  n = 1
  ref = Pu_element
FEATURE [App::DocumentObjectGroupPython] O_element076  label="O_element : 037"  # scripted group (container) (typed FeaturePython)
  n = 2
  ref = O_element
FEATURE [App::DocumentObjectGroupPython] G4_PLUTONIUM_DIOXIDE  # scripted group (container) (typed FeaturePython)
  Dunit = g/cm3
  Dvalue = 11.46
  Group = -> [Pu_element001,O_element076]
  conduct = 2
  density = 1
  expand = 3
  formula = G4_PLUTONIUM_DIOXIDE
  name = G4_PLUTONIUM_DIOXIDE
  specific = 4
FEATURE [App::DocumentObjectGroupPython] C_element078  label="C_element : 037"  # scripted group (container) (typed FeaturePython)
  n = 3
  ref = C_element
FEATURE [App::DocumentObjectGroupPython] H_element072  label="H_element : 034"  # scripted group (container) (typed FeaturePython)
  n = 3
  ref = H_element
FEATURE [App::DocumentObjectGroupPython] N_element036  label="N_element : 015"  # scripted group (container) (typed FeaturePython)
  n = 1
  ref = N_element
FEATURE [App::DocumentObjectGroupPython] G4_POLYACRYLONITRILE  # scripted group (container) (typed FeaturePython)
  Dunit = g/cm3
  Dvalue = 1.17
  Group = -> [C_element078,H_element072,N_element036]
  conduct = 2
  density = 1
  expand = 3
  formula = G4_POLYACRYLONITRILE
  name = G4_POLYACRYLONITRILE
  specific = 4
FEATURE [App::DocumentObjectGroupPython] C_element079  label="C_element : 16"  # scripted group (container) (typed FeaturePython)
  n = 16
  ref = C_element
FEATURE [App::DocumentObjectGroupPython] H_element073  label="H_element : 035"  # scripted group (container) (typed FeaturePython)
  n = 14
  ref = H_element
FEATURE [App::DocumentObjectGroupPython] O_element077  label="O_element : 038"  # scripted group (container) (typed FeaturePython)
  n = 3
  ref = O_element
FEATURE [App::DocumentObjectGroupPython] G4_POLYCARBONATE  # scripted group (container) (typed FeaturePython)
  Dunit = g/cm3
  Dvalue = 1.2
  Group = -> [C_element079,H_element073,O_element077]
  conduct = 2
  density = 1
  expand = 3
  formula = G4_POLYCARBONATE
  name = G4_POLYCARBONATE
  specific = 4
FEATURE [App::DocumentObjectGroupPython] C_element080  label="C_element : 038"  # scripted group (container) (typed FeaturePython)
  n = 8
  ref = C_element
FEATURE [App::DocumentObjectGroupPython] H_element074  label="H_element : 036"  # scripted group (container) (typed FeaturePython)
  n = 7
  ref = H_element
FEATURE [App::DocumentObjectGroupPython] Cl_element017  label="Cl_element : 007"  # scripted group (container) (typed FeaturePython)
  n = 1
  ref = Cl_element
FEATURE [App::DocumentObjectGroupPython] G4_POLYCHLOROSTYRENE  # scripted group (container) (typed FeaturePython)
  Dunit = g/cm3
  Dvalue = 1.3
  Group = -> [C_element080,H_element074,Cl_element017]
  conduct = 2
  density = 1
  expand = 3
  formula = G4_POLYCHLOROSTYRENE
  name = G4_POLYCHLOROSTYRENE
  specific = 4
FEATURE [App::DocumentObjectGroupPython] C_element081  label="C_element : 039"  # scripted group (container) (typed FeaturePython)
  n = 1
  ref = C_element
FEATURE [App::DocumentObjectGroupPython] H_element075  label="H_element : 037"  # scripted group (container) (typed FeaturePython)
  n = 2
  ref = H_element
FEATURE [App::DocumentObjectGroupPython] G4_POLYETHYLENE  # scripted group (container) (typed FeaturePython)
  Dunit = g/cm3
  Dvalue = 0.94
  Group = -> [C_element081,H_element075]
  conduct = 2
  density = 1
  expand = 3
  formula = G4_POLYETHYLENE
  name = G4_POLYETHYLENE
  specific = 4
FEATURE [App::DocumentObjectGroupPython] C_element082  label="C_element : 040"  # scripted group (container) (typed FeaturePython)
  n = 10
  ref = C_element
FEATURE [App::DocumentObjectGroupPython] H_element076  label="H_element : 038"  # scripted group (container) (typed FeaturePython)
  n = 8
  ref = H_element
FEATURE [App::DocumentObjectGroupPython] O_element078  label="O_element : 039"  # scripted group (container) (typed FeaturePython)
  n = 4
  ref = O_element
FEATURE [App::DocumentObjectGroupPython] G4_MYLAR  # scripted group (container) (typed FeaturePython)
  Dunit = g/cm3
  Dvalue = 1.4
  Group = -> [C_element082,H_element076,O_element078]
  conduct = 2
  density = 1
  expand = 3
  formula = G4_MYLAR
  name = G4_MYLAR
  specific = 4
FEATURE [App::DocumentObjectGroupPython] C_element083  label="C_element : 041"  # scripted group (container) (typed FeaturePython)
  n = 5
  ref = C_element
FEATURE [App::DocumentObjectGroupPython] H_element077  label="H_element : 039"  # scripted group (container) (typed FeaturePython)
  n = 8
  ref = H_element
FEATURE [App::DocumentObjectGroupPython] O_element079  label="O_element : 040"  # scripted group (container) (typed FeaturePython)
  n = 2
  ref = O_element
FEATURE [App::DocumentObjectGroupPython] G4_PLEXIGLASS  # scripted group (container) (typed FeaturePython)
  Dunit = g/cm3
  Dvalue = 1.19
  Group = -> [C_element083,H_element077,O_element079]
  conduct = 2
  density = 1
  expand = 3
  formula = G4_PLEXIGLASS
  name = G4_PLEXIGLASS
  specific = 4
FEATURE [App::DocumentObjectGroupPython] C_element084  label="C_element : 042"  # scripted group (container) (typed FeaturePython)
  n = 1
  ref = C_element
FEATURE [App::DocumentObjectGroupPython] H_element078  label="H_element : 040"  # scripted group (container) (typed FeaturePython)
  n = 2
  ref = H_element
FEATURE [App::DocumentObjectGroupPython] O_element080  label="O_element : 041"  # scripted group (container) (typed FeaturePython)
  n = 1
  ref = O_element
FEATURE [App::DocumentObjectGroupPython] G4_POLYOXYMETHYLENE  # scripted group (container) (typed FeaturePython)
  Dunit = g/cm3
  Dvalue = 1.425
  Group = -> [C_element084,H_element078,O_element080]
  conduct = 2
  density = 1
  expand = 3
  formula = G4_POLYOXYMETHYLENE
  name = G4_POLYOXYMETHYLENE
  specific = 4
FEATURE [App::DocumentObjectGroupPython] C_element085  label="C_element : 043"  # scripted group (container) (typed FeaturePython)
  n = 2
  ref = C_element
FEATURE [App::DocumentObjectGroupPython] H_element079  label="H_element : 041"  # scripted group (container) (typed FeaturePython)
  n = 4
  ref = H_element
FEATURE [App::DocumentObjectGroupPython] G4_POLYPROPYLENE  # scripted group (container) (typed FeaturePython)
  Dunit = g/cm3
  Dvalue = 0.9
  Group = -> [C_element085,H_element079]
  conduct = 2
  density = 1
  expand = 3
  formula = G4_POLYPROPYLENE
  name = G4_POLYPROPYLENE
  specific = 4
FEATURE [App::DocumentObjectGroupPython] C_element086  label="C_element : 044"  # scripted group (container) (typed FeaturePython)
  n = 8
  ref = C_element
FEATURE [App::DocumentObjectGroupPython] H_element080  label="H_element : 042"  # scripted group (container) (typed FeaturePython)
  n = 8
  ref = H_element
FEATURE [App::DocumentObjectGroupPython] G4_POLYSTYRENE  # scripted group (container) (typed FeaturePython)
  Dunit = g/cm3
  Dvalue = 1.06
  Group = -> [C_element086,H_element080]
  conduct = 2
  density = 1
  expand = 3
  formula = G4_POLYSTYRENE
  name = G4_POLYSTYRENE
  specific = 4
FEATURE [App::DocumentObjectGroupPython] C_element087  label="C_element : 045"  # scripted group (container) (typed FeaturePython)
  n = 2
  ref = C_element
FEATURE [App::DocumentObjectGroupPython] F_element014  label="F_element : 4"  # scripted group (container) (typed FeaturePython)
  n = 4
  ref = F_element
FEATURE [App::DocumentObjectGroupPython] G4_TEFLON  # scripted group (container) (typed FeaturePython)
  Dunit = g/cm3
  Dvalue = 2.2
  Group = -> [C_element087,F_element014]
  conduct = 2
  density = 1
  expand = 3
  formula = G4_TEFLON
  name = G4_TEFLON
  specific = 4
FEATURE [App::DocumentObjectGroupPython] C_element088  label="C_element : 046"  # scripted group (container) (typed FeaturePython)
  n = 2
  ref = C_element
FEATURE [App::DocumentObjectGroupPython] F_element015  label="F_element : 006"  # scripted group (container) (typed FeaturePython)
  n = 3
  ref = F_element
FEATURE [App::DocumentObjectGroupPython] Cl_element018  label="Cl_element : 008"  # scripted group (container) (typed FeaturePython)
  n = 1
  ref = Cl_element
FEATURE [App::DocumentObjectGroupPython] G4_POLYTRIFLUOROCHLOROETHYLENE  # scripted group (container) (typed FeaturePython)
  Dunit = g/cm3
  Dvalue = 2.1
  Group = -> [C_element088,F_element015,Cl_element018]
  conduct = 2
  density = 1
  expand = 3
  formula = G4_POLYTRIFLUOROCHLOROETHYLENE
  name = G4_POLYTRIFLUOROCHLOROETHYLENE
  specific = 4
FEATURE [App::DocumentObjectGroupPython] C_element089  label="C_element : 047"  # scripted group (container) (typed FeaturePython)
  n = 4
  ref = C_element
FEATURE [App::DocumentObjectGroupPython] H_element081  label="H_element : 043"  # scripted group (container) (typed FeaturePython)
  n = 6
  ref = H_element
FEATURE [App::DocumentObjectGroupPython] O_element081  label="O_element : 042"  # scripted group (container) (typed FeaturePython)
  n = 2
  ref = O_element
FEATURE [App::DocumentObjectGroupPython] G4_POLYVINYL_ACETATE  # scripted group (container) (typed FeaturePython)
  Dunit = g/cm3
  Dvalue = 1.19
  Group = -> [C_element089,H_element081,O_element081]
  conduct = 2
  density = 1
  expand = 3
  formula = G4_POLYVINYL_ACETATE
  name = G4_POLYVINYL_ACETATE
  specific = 4
FEATURE [App::DocumentObjectGroupPython] C_element090  label="C_element : 048"  # scripted group (container) (typed FeaturePython)
  n = 2
  ref = C_element
FEATURE [App::DocumentObjectGroupPython] H_element082  label="H_element : 044"  # scripted group (container) (typed FeaturePython)
  n = 4
  ref = H_element
FEATURE [App::DocumentObjectGroupPython] O_element082  label="O_element : 043"  # scripted group (container) (typed FeaturePython)
  n = 1
  ref = O_element
FEATURE [App::DocumentObjectGroupPython] G4_POLYVINYL_ALCOHOL  # scripted group (container) (typed FeaturePython)
  Dunit = g/cm3
  Dvalue = 1.3
  Group = -> [C_element090,H_element082,O_element082]
  conduct = 2
  density = 1
  expand = 3
  formula = G4_POLYVINYL_ALCOHOL
  name = G4_POLYVINYL_ALCOHOL
  specific = 4
FEATURE [App::DocumentObjectGroupPython] C_element091  label="C_element : 049"  # scripted group (container) (typed FeaturePython)
  n = 8
  ref = C_element
FEATURE [App::DocumentObjectGroupPython] H_element083  label="H_element : 045"  # scripted group (container) (typed FeaturePython)
  n = 14
  ref = H_element
FEATURE [App::DocumentObjectGroupPython] O_element083  label="O_element : 044"  # scripted group (container) (typed FeaturePython)
  n = 2
  ref = O_element
FEATURE [App::DocumentObjectGroupPython] G4_POLYVINYL_BUTYRAL  # scripted group (container) (typed FeaturePython)
  Dunit = g/cm3
  Dvalue = 1.12
  Group = -> [C_element091,H_element083,O_element083]
  conduct = 2
  density = 1
  expand = 3
  formula = G4_POLYVINYL_BUTYRAL
  name = G4_POLYVINYL_BUTYRAL
  specific = 4
FEATURE [App::DocumentObjectGroupPython] C_element092  label="C_element : 050"  # scripted group (container) (typed FeaturePython)
  n = 2
  ref = C_element
FEATURE [App::DocumentObjectGroupPython] H_element084  label="H_element : 046"  # scripted group (container) (typed FeaturePython)
  n = 3
  ref = H_element
FEATURE [App::DocumentObjectGroupPython] Cl_element019  label="Cl_element : 009"  # scripted group (container) (typed FeaturePython)
  n = 1
  ref = Cl_element
FEATURE [App::DocumentObjectGroupPython] G4_POLYVINYL_CHLORIDE  # scripted group (container) (typed FeaturePython)
  Dunit = g/cm3
  Dvalue = 1.3
  Group = -> [C_element092,H_element084,Cl_element019]
  conduct = 2
  density = 1
  expand = 3
  formula = G4_POLYVINYL_CHLORIDE
  name = G4_POLYVINYL_CHLORIDE
  specific = 4
FEATURE [App::DocumentObjectGroupPython] C_element093  label="C_element : 051"  # scripted group (container) (typed FeaturePython)
  n = 2
  ref = C_element
FEATURE [App::DocumentObjectGroupPython] H_element085  label="H_element : 047"  # scripted group (container) (typed FeaturePython)
  n = 2
  ref = H_element
FEATURE [App::DocumentObjectGroupPython] Cl_element020  label="Cl_element : 010"  # scripted group (container) (typed FeaturePython)
  n = 2
  ref = Cl_element
FEATURE [App::DocumentObjectGroupPython] G4_POLYVINYLIDENE_CHLORIDE  # scripted group (container) (typed FeaturePython)
  Dunit = g/cm3
  Dvalue = 1.7
  Group = -> [C_element093,H_element085,Cl_element020]
  conduct = 2
  density = 1
  expand = 3
  formula = G4_POLYVINYLIDENE_CHLORIDE
  name = G4_POLYVINYLIDENE_CHLORIDE
  specific = 4
FEATURE [App::DocumentObjectGroupPython] C_element094  label="C_element : 052"  # scripted group (container) (typed FeaturePython)
  n = 2
  ref = C_element
FEATURE [App::DocumentObjectGroupPython] H_element086  label="H_element : 048"  # scripted group (container) (typed FeaturePython)
  n = 2
  ref = H_element
FEATURE [App::DocumentObjectGroupPython] F_element016  label="F_element : 007"  # scripted group (container) (typed FeaturePython)
  n = 2
  ref = F_element
FEATURE [App::DocumentObjectGroupPython] G4_POLYVINYLIDENE_FLUORIDE  # scripted group (container) (typed FeaturePython)
  Dunit = g/cm3
  Dvalue = 1.76
  Group = -> [C_element094,H_element086,F_element016]
  conduct = 2
  density = 1
  expand = 3
  formula = G4_POLYVINYLIDENE_FLUORIDE
  name = G4_POLYVINYLIDENE_FLUORIDE
  specific = 4
FEATURE [App::DocumentObjectGroupPython] C_element095  label="C_element : 053"  # scripted group (container) (typed FeaturePython)
  n = 6
  ref = C_element
FEATURE [App::DocumentObjectGroupPython] H_element087  label="H_element : 9"  # scripted group (container) (typed FeaturePython)
  n = 9
  ref = H_element
FEATURE [App::DocumentObjectGroupPython] N_element037  label="N_element : 016"  # scripted group (container) (typed FeaturePython)
  n = 1
  ref = N_element
FEATURE [App::DocumentObjectGroupPython] O_element084  label="O_element : 045"  # scripted group (container) (typed FeaturePython)
  n = 1
  ref = O_element
FEATURE [App::DocumentObjectGroupPython] G4_POLYVINYL_PYRROLIDONE  # scripted group (container) (typed FeaturePython)
  Dunit = g/cm3
  Dvalue = 1.25
  Group = -> [C_element095,H_element087,N_element037,O_element084]
  conduct = 2
  density = 1
  expand = 3
  formula = G4_POLYVINYL_PYRROLIDONE
  name = G4_POLYVINYL_PYRROLIDONE
  specific = 4
FEATURE [App::DocumentObjectGroupPython] K_element008  label="K_element : 1"  # scripted group (container) (typed FeaturePython)
  n = 1
  ref = K_element
FEATURE [App::DocumentObjectGroupPython] I_element006  label="I_element : 003"  # scripted group (container) (typed FeaturePython)
  n = 1
  ref = I_element
FEATURE [App::DocumentObjectGroupPython] G4_POTASSIUM_IODIDE  # scripted group (container) (typed FeaturePython)
  Dunit = g/cm3
  Dvalue = 3.13
  Group = -> [K_element008,I_element006]
  conduct = 2
  density = 1
  expand = 3
  formula = G4_POTASSIUM_IODIDE
  name = G4_POTASSIUM_IODIDE
  specific = 4
FEATURE [App::DocumentObjectGroupPython] K_element009  label="K_element : 2"  # scripted group (container) (typed FeaturePython)
  n = 2
  ref = K_element
FEATURE [App::DocumentObjectGroupPython] O_element085  label="O_element : 046"  # scripted group (container) (typed FeaturePython)
  n = 1
  ref = O_element
FEATURE [App::DocumentObjectGroupPython] G4_POTASSIUM_OXIDE  # scripted group (container) (typed FeaturePython)
  Dunit = g/cm3
  Dvalue = 2.32
  Group = -> [K_element009,O_element085]
  conduct = 2
  density = 1
  expand = 3
  formula = G4_POTASSIUM_OXIDE
  name = G4_POTASSIUM_OXIDE
  specific = 4
FEATURE [App::DocumentObjectGroupPython] C_element096  label="C_element : 054"  # scripted group (container) (typed FeaturePython)
  n = 3
  ref = C_element
FEATURE [App::DocumentObjectGroupPython] H_element088  label="H_element : 049"  # scripted group (container) (typed FeaturePython)
  n = 8
  ref = H_element
FEATURE [App::DocumentObjectGroupPython] G4_PROPANE  # scripted group (container) (typed FeaturePython)
  Dunit = g/cm3
  Dvalue = 0.00187939
  Group = -> [C_element096,H_element088]
  conduct = 2
  density = 1
  expand = 3
  formula = G4_PROPANE
  name = G4_PROPANE
  specific = 4
FEATURE [App::DocumentObjectGroupPython] C_element097  label="C_element : 055"  # scripted group (container) (typed FeaturePython)
  n = 3
  ref = C_element
FEATURE [App::DocumentObjectGroupPython] H_element089  label="H_element : 050"  # scripted group (container) (typed FeaturePython)
  n = 8
  ref = H_element
FEATURE [App::DocumentObjectGroupPython] G4_lPROPANE  # scripted group (container) (typed FeaturePython)
  Dunit = g/cm3
  Dvalue = 0.43
  Group = -> [C_element097,H_element089]
  conduct = 2
  density = 1
  expand = 3
  formula = G4_lPROPANE
  name = G4_lPROPANE
  specific = 4
FEATURE [App::DocumentObjectGroupPython] C_element098  label="C_element : 056"  # scripted group (container) (typed FeaturePython)
  n = 3
  ref = C_element
FEATURE [App::DocumentObjectGroupPython] H_element090  label="H_element : 051"  # scripted group (container) (typed FeaturePython)
  n = 8
  ref = H_element
FEATURE [App::DocumentObjectGroupPython] O_element086  label="O_element : 047"  # scripted group (container) (typed FeaturePython)
  n = 1
  ref = O_element
FEATURE [App::DocumentObjectGroupPython] G4_N_PROPYL_ALCOHOL  label="G4_N-PROPYL_ALCOHOL"  # scripted group (container) (typed FeaturePython)
  Dunit = g/cm3
  Dvalue = 0.8035
  Group = -> [C_element098,H_element090,O_element086]
  conduct = 2
  density = 1
  expand = 3
  formula = G4_N-PROPYL_ALCOHOL
  name = G4_N-PROPYL_ALCOHOL
  specific = 4
FEATURE [App::DocumentObjectGroupPython] C_element099  label="C_element : 057"  # scripted group (container) (typed FeaturePython)
  n = 5
  ref = C_element
FEATURE [App::DocumentObjectGroupPython] H_element091  label="H_element : 052"  # scripted group (container) (typed FeaturePython)
  n = 5
  ref = H_element
FEATURE [App::DocumentObjectGroupPython] N_element038  label="N_element : 017"  # scripted group (container) (typed FeaturePython)
  n = 1
  ref = N_element
FEATURE [App::DocumentObjectGroupPython] G4_PYRIDINE  # scripted group (container) (typed FeaturePython)
  Dunit = g/cm3
  Dvalue = 0.9819
  Group = -> [C_element099,H_element091,N_element038]
  conduct = 2
  density = 1
  expand = 3
  formula = G4_PYRIDINE
  name = G4_PYRIDINE
  specific = 4
FEATURE [App::DocumentObjectGroupPython] H_element092  label="H_element : 0.144"  # scripted group (container) (typed FeaturePython)
  n = 0.143711
FEATURE [App::DocumentObjectGroupPython] C_element100  label="C_element : 0.856"  # scripted group (container) (typed FeaturePython)
  n = 0.856289
FEATURE [App::DocumentObjectGroupPython] G4_RUBBER_BUTYL  # scripted group (container) (typed FeaturePython)
  Dunit = g/cm3
  Dvalue = 0.92
  Group = -> [H_element092,C_element100]
  conduct = 2
  density = 1
  expand = 3
  formula = G4_RUBBER_BUTYL
  name = G4_RUBBER_BUTYL
  specific = 4
FEATURE [App::DocumentObjectGroupPython] H_element093  label="H_element : 0.118"  # scripted group (container) (typed FeaturePython)
  n = 0.118371
FEATURE [App::DocumentObjectGroupPython] C_element101  label="C_element : 0.882"  # scripted group (container) (typed FeaturePython)
  n = 0.881629
FEATURE [App::DocumentObjectGroupPython] G4_RUBBER_NATURAL  # scripted group (container) (typed FeaturePython)
  Dunit = g/cm3
  Dvalue = 0.92
  Group = -> [H_element093,C_element101]
  conduct = 2
  density = 1
  expand = 3
  formula = G4_RUBBER_NATURAL
  name = G4_RUBBER_NATURAL
  specific = 4
FEATURE [App::DocumentObjectGroupPython] H_element094  label="H_element : 0.145"  # scripted group (container) (typed FeaturePython)
  n = 0.05692
FEATURE [App::DocumentObjectGroupPython] C_element102  label="C_element : 0.543"  # scripted group (container) (typed FeaturePython)
  n = 0.542646
FEATURE [App::DocumentObjectGroupPython] Cl_element021  label="Cl_element : 0.400"  # scripted group (container) (typed FeaturePython)
  n = 0.400434
FEATURE [App::DocumentObjectGroupPython] G4_RUBBER_NEOPRENE  # scripted group (container) (typed FeaturePython)
  Dunit = g/cm3
  Dvalue = 1.23
  Group = -> [H_element094,C_element102,Cl_element021]
  conduct = 2
  density = 1
  expand = 3
  formula = G4_RUBBER_NEOPRENE
  name = G4_RUBBER_NEOPRENE
  specific = 4
FEATURE [App::DocumentObjectGroupPython] Si_element006  label="Si_element : 1"  # scripted group (container) (typed FeaturePython)
  n = 1
  ref = Si_element
FEATURE [App::DocumentObjectGroupPython] O_element087  label="O_element : 048"  # scripted group (container) (typed FeaturePython)
  n = 2
  ref = O_element
FEATURE [App::DocumentObjectGroupPython] G4_SILICON_DIOXIDE  # scripted group (container) (typed FeaturePython)
  Dunit = g/cm3
  Dvalue = 2.32
  Group = -> [Si_element006,O_element087]
  conduct = 2
  density = 1
  expand = 3
  formula = G4_SILICON_DIOXIDE
  name = G4_SILICON_DIOXIDE
  specific = 4
FEATURE [App::DocumentObjectGroupPython] Ag_element002  label="Ag_element : 1"  # scripted group (container) (typed FeaturePython)
  n = 1
  ref = Ag_element
FEATURE [App::DocumentObjectGroupPython] Br_element005  label="Br_element : 003"  # scripted group (container) (typed FeaturePython)
  n = 1
  ref = Br_element
FEATURE [App::DocumentObjectGroupPython] G4_SILVER_BROMIDE  # scripted group (container) (typed FeaturePython)
  Dunit = g/cm3
  Dvalue = 6.473
  Group = -> [Ag_element002,Br_element005]
  conduct = 2
  density = 1
  expand = 3
  formula = G4_SILVER_BROMIDE
  name = G4_SILVER_BROMIDE
  specific = 4
FEATURE [App::DocumentObjectGroupPython] Ag_element003  label="Ag_element : 002"  # scripted group (container) (typed FeaturePython)
  n = 1
  ref = Ag_element
FEATURE [App::DocumentObjectGroupPython] Cl_element022  label="Cl_element : 011"  # scripted group (container) (typed FeaturePython)
  n = 1
  ref = Cl_element
FEATURE [App::DocumentObjectGroupPython] G4_SILVER_CHLORIDE  # scripted group (container) (typed FeaturePython)
  Dunit = g/cm3
  Dvalue = 5.56
  Group = -> [Ag_element003,Cl_element022]
  conduct = 2
  density = 1
  expand = 3
  formula = G4_SILVER_CHLORIDE
  name = G4_SILVER_CHLORIDE
  specific = 4
FEATURE [App::DocumentObjectGroupPython] Br_element006  label="Br_element : 0.423"  # scripted group (container) (typed FeaturePython)
  n = 0.422895
FEATURE [App::DocumentObjectGroupPython] Ag_element004  label="Ag_element : 0.574"  # scripted group (container) (typed FeaturePython)
  n = 0.573748
FEATURE [App::DocumentObjectGroupPython] I_element007  label="I_element : 0.649"  # scripted group (container) (typed FeaturePython)
  n = 0.003357
FEATURE [App::DocumentObjectGroupPython] G4_SILVER_HALIDES  # scripted group (container) (typed FeaturePython)
  Dunit = g/cm3
  Dvalue = 6.47
  Group = -> [Br_element006,Ag_element004,I_element007]
  conduct = 2
  density = 1
  expand = 3
  formula = G4_SILVER_HALIDES
  name = G4_SILVER_HALIDES
  specific = 4
FEATURE [App::DocumentObjectGroupPython] Ag_element005  label="Ag_element : 003"  # scripted group (container) (typed FeaturePython)
  n = 1
  ref = Ag_element
FEATURE [App::DocumentObjectGroupPython] I_element008  label="I_element : 004"  # scripted group (container) (typed FeaturePython)
  n = 1
  ref = I_element
FEATURE [App::DocumentObjectGroupPython] G4_SILVER_IODIDE  # scripted group (container) (typed FeaturePython)
  Dunit = g/cm3
  Dvalue = 6.01
  Group = -> [Ag_element005,I_element008]
  conduct = 2
  density = 1
  expand = 3
  formula = G4_SILVER_IODIDE
  name = G4_SILVER_IODIDE
  specific = 4
FEATURE [App::DocumentObjectGroupPython] H_element095  label="H_element : 0.100"  # scripted group (container) (typed FeaturePython)
  n = 0.1
FEATURE [App::DocumentObjectGroupPython] C_element103  label="C_element : 0.204"  # scripted group (container) (typed FeaturePython)
  n = 0.204
FEATURE [App::DocumentObjectGroupPython] N_element039  label="N_element : 0.759"  # scripted group (container) (typed FeaturePython)
  n = 0.042
FEATURE [App::DocumentObjectGroupPython] O_element088  label="O_element : 0.645"  # scripted group (container) (typed FeaturePython)
  n = 0.645
FEATURE [App::DocumentObjectGroupPython] Na_element013  label="Na_element : 0.100"  # scripted group (container) (typed FeaturePython)
  n = 0.002
FEATURE [App::DocumentObjectGroupPython] P_element009  label="P_element : 0.107"  # scripted group (container) (typed FeaturePython)
  n = 0.001
FEATURE [App::DocumentObjectGroupPython] S_element020  label="S_element : 0.021"  # scripted group (container) (typed FeaturePython)
  n = 0.002
FEATURE [App::DocumentObjectGroupPython] Cl_element023  label="Cl_element : 0.590"  # scripted group (container) (typed FeaturePython)
  n = 0.003
FEATURE [App::DocumentObjectGroupPython] K_element010  label="K_element : 0.001"  # scripted group (container) (typed FeaturePython)
  n = 0.001
FEATURE [App::DocumentObjectGroupPython] G4_SKIN_ICRP  # scripted group (container) (typed FeaturePython)
  Dunit = g/cm3
  Dvalue = 1.09
  Group = -> [H_element095,C_element103,N_element039,O_element088,Na_element013,P_element009,S_element020,Cl_element023,K_element010]
  conduct = 2
  density = 1
  expand = 3
  formula = G4_SKIN_ICRP
  name = G4_SKIN_ICRP
  specific = 4
FEATURE [App::DocumentObjectGroupPython] Na_element014  label="Na_element : 2"  # scripted group (container) (typed FeaturePython)
  n = 2
  ref = Na_element
FEATURE [App::DocumentObjectGroupPython] C_element104  label="C_element : 058"  # scripted group (container) (typed FeaturePython)
  n = 1
  ref = C_element
FEATURE [App::DocumentObjectGroupPython] O_element089  label="O_element : 049"  # scripted group (container) (typed FeaturePython)
  n = 3
  ref = O_element
FEATURE [App::DocumentObjectGroupPython] G4_SODIUM_CARBONATE  # scripted group (container) (typed FeaturePython)
  Dunit = g/cm3
  Dvalue = 2.532
  Group = -> [Na_element014,C_element104,O_element089]
  conduct = 2
  density = 1
  expand = 3
  formula = G4_SODIUM_CARBONATE
  name = G4_SODIUM_CARBONATE
  specific = 4
FEATURE [App::DocumentObjectGroupPython] Na_element015  label="Na_element : 1"  # scripted group (container) (typed FeaturePython)
  n = 1
  ref = Na_element
FEATURE [App::DocumentObjectGroupPython] I_element009  label="I_element : 005"  # scripted group (container) (typed FeaturePython)
  n = 1
  ref = I_element
FEATURE [App::DocumentObjectGroupPython] G4_SODIUM_IODIDE  # scripted group (container) (typed FeaturePython)
  Dunit = g/cm3
  Dvalue = 3.667
  Group = -> [Na_element015,I_element009]
  conduct = 2
  density = 1
  expand = 3
  formula = G4_SODIUM_IODIDE
  name = G4_SODIUM_IODIDE
  specific = 4
FEATURE [App::DocumentObjectGroupPython] Na_element016  label="Na_element : 003"  # scripted group (container) (typed FeaturePython)
  n = 2
  ref = Na_element
FEATURE [App::DocumentObjectGroupPython] O_element090  label="O_element : 050"  # scripted group (container) (typed FeaturePython)
  n = 1
  ref = O_element
FEATURE [App::DocumentObjectGroupPython] G4_SODIUM_MONOXIDE  # scripted group (container) (typed FeaturePython)
  Dunit = g/cm3
  Dvalue = 2.27
  Group = -> [Na_element016,O_element090]
  conduct = 2
  density = 1
  expand = 3
  formula = G4_SODIUM_MONOXIDE
  name = G4_SODIUM_MONOXIDE
  specific = 4
FEATURE [App::DocumentObjectGroupPython] Na_element017  label="Na_element : 004"  # scripted group (container) (typed FeaturePython)
  n = 1
  ref = Na_element
FEATURE [App::DocumentObjectGroupPython] N_element040  label="N_element : 018"  # scripted group (container) (typed FeaturePython)
  n = 1
  ref = N_element
FEATURE [App::DocumentObjectGroupPython] O_element091  label="O_element : 051"  # scripted group (container) (typed FeaturePython)
  n = 3
  ref = O_element
FEATURE [App::DocumentObjectGroupPython] G4_SODIUM_NITRATE  # scripted group (container) (typed FeaturePython)
  Dunit = g/cm3
  Dvalue = 2.261
  Group = -> [Na_element017,N_element040,O_element091]
  conduct = 2
  density = 1
  expand = 3
  formula = G4_SODIUM_NITRATE
  name = G4_SODIUM_NITRATE
  specific = 4
FEATURE [App::DocumentObjectGroupPython] C_element105  label="C_element : 059"  # scripted group (container) (typed FeaturePython)
  n = 14
  ref = C_element
FEATURE [App::DocumentObjectGroupPython] H_element096  label="H_element : 053"  # scripted group (container) (typed FeaturePython)
  n = 12
  ref = H_element
FEATURE [App::DocumentObjectGroupPython] G4_STILBENE  # scripted group (container) (typed FeaturePython)
  Dunit = g/cm3
  Dvalue = 0.9707
  Group = -> [C_element105,H_element096]
  conduct = 2
  density = 1
  expand = 3
  formula = G4_STILBENE
  name = G4_STILBENE
  specific = 4
FEATURE [App::DocumentObjectGroupPython] C_element106  label="C_element : 12"  # scripted group (container) (typed FeaturePython)
  n = 12
  ref = C_element
FEATURE [App::DocumentObjectGroupPython] H_element097  label="H_element : 22"  # scripted group (container) (typed FeaturePython)
  n = 22
  ref = H_element
FEATURE [App::DocumentObjectGroupPython] O_element092  label="O_element : 11"  # scripted group (container) (typed FeaturePython)
  n = 11
  ref = O_element
FEATURE [App::DocumentObjectGroupPython] G4_SUCROSE  # scripted group (container) (typed FeaturePython)
  Dunit = g/cm3
  Dvalue = 1.5805
  Group = -> [C_element106,H_element097,O_element092]
  conduct = 2
  density = 1
  expand = 3
  formula = G4_SUCROSE
  name = G4_SUCROSE
  specific = 4
FEATURE [App::DocumentObjectGroupPython] C_element107  label="C_element : 18"  # scripted group (container) (typed FeaturePython)
  n = 18
  ref = C_element
FEATURE [App::DocumentObjectGroupPython] H_element098  label="H_element : 054"  # scripted group (container) (typed FeaturePython)
  n = 14
  ref = H_element
FEATURE [App::DocumentObjectGroupPython] G4_TERPHENYL  # scripted group (container) (typed FeaturePython)
  Dunit = g/cm3
  Dvalue = 1.24
  Group = -> [C_element107,H_element098]
  conduct = 2
  density = 1
  expand = 3
  formula = G4_TERPHENYL
  name = G4_TERPHENYL
  specific = 4
FEATURE [App::DocumentObjectGroupPython] H_element099  label="H_element : 0.146"  # scripted group (container) (typed FeaturePython)
  n = 0.106
FEATURE [App::DocumentObjectGroupPython] C_element108  label="C_element : 0.883"  # scripted group (container) (typed FeaturePython)
  n = 0.099
FEATURE [App::DocumentObjectGroupPython] N_element041  label="N_element : 0.020"  # scripted group (container) (typed FeaturePython)
  n = 0.02
FEATURE [App::DocumentObjectGroupPython] O_element093  label="O_element : 0.766"  # scripted group (container) (typed FeaturePython)
  n = 0.766
FEATURE [App::DocumentObjectGroupPython] Na_element018  label="Na_element : 0.101"  # scripted group (container) (typed FeaturePython)
  n = 0.002
FEATURE [App::DocumentObjectGroupPython] P_element010  label="P_element : 0.108"  # scripted group (container) (typed FeaturePython)
  n = 0.001
FEATURE [App::DocumentObjectGroupPython] S_element021  label="S_element : 0.022"  # scripted group (container) (typed FeaturePython)
  n = 0.002
FEATURE [App::DocumentObjectGroupPython] Cl_element024  label="Cl_element : 0.002"  # scripted group (container) (typed FeaturePython)
  n = 0.002
FEATURE [App::DocumentObjectGroupPython] K_element011  label="K_element : 0.017"  # scripted group (container) (typed FeaturePython)
  n = 0.002
FEATURE [App::DocumentObjectGroupPython] G4_TESTIS_ICRP  # scripted group (container) (typed FeaturePython)
  Dunit = g/cm3
  Dvalue = 1.04
  Group = -> [H_element099,C_element108,N_element041,O_element093,Na_element018,P_element010,S_element021,Cl_element024,K_element011]
  conduct = 2
  density = 1
  expand = 3
  formula = G4_TESTIS_ICRP
  name = G4_TESTIS_ICRP
  specific = 4
FEATURE [App::DocumentObjectGroupPython] C_element109  label="C_element : 060"  # scripted group (container) (typed FeaturePython)
  n = 2
  ref = C_element
FEATURE [App::DocumentObjectGroupPython] Cl_element025  label="Cl_element : 012"  # scripted group (container) (typed FeaturePython)
  n = 4
  ref = Cl_element
FEATURE [App::DocumentObjectGroupPython] G4_TETRACHLOROETHYLENE  # scripted group (container) (typed FeaturePython)
  Dunit = g/cm3
  Dvalue = 1.625
  Group = -> [C_element109,Cl_element025]
  conduct = 2
  density = 1
  expand = 3
  formula = G4_TETRACHLOROETHYLENE
  name = G4_TETRACHLOROETHYLENE
  specific = 4
FEATURE [App::DocumentObjectGroupPython] Tl_element001  label="Tl_element : 1"  # scripted group (container) (typed FeaturePython)
  n = 1
  ref = Tl_element
FEATURE [App::DocumentObjectGroupPython] Cl_element026  label="Cl_element : 013"  # scripted group (container) (typed FeaturePython)
  n = 1
  ref = Cl_element
FEATURE [App::DocumentObjectGroupPython] G4_THALLIUM_CHLORIDE  # scripted group (container) (typed FeaturePython)
  Dunit = g/cm3
  Dvalue = 7.004
  Group = -> [Tl_element001,Cl_element026]
  conduct = 2
  density = 1
  expand = 3
  formula = G4_THALLIUM_CHLORIDE
  name = G4_THALLIUM_CHLORIDE
  specific = 4
FEATURE [App::DocumentObjectGroupPython] H_element100  label="H_element : 0.147"  # scripted group (container) (typed FeaturePython)
  n = 0.105
FEATURE [App::DocumentObjectGroupPython] C_element110  label="C_element : 0.256"  # scripted group (container) (typed FeaturePython)
  n = 0.256
FEATURE [App::DocumentObjectGroupPython] N_element042  label="N_element : 0.760"  # scripted group (container) (typed FeaturePython)
  n = 0.027
FEATURE [App::DocumentObjectGroupPython] O_element094  label="O_element : 0.602"  # scripted group (container) (typed FeaturePython)
  n = 0.602
FEATURE [App::DocumentObjectGroupPython] Na_element019  label="Na_element : 0.102"  # scripted group (container) (typed FeaturePython)
  n = 0.001
FEATURE [App::DocumentObjectGroupPython] P_element011  label="P_element : 0.109"  # scripted group (container) (typed FeaturePython)
  n = 0.002
FEATURE [App::DocumentObjectGroupPython] S_element022  label="S_element : 0.023"  # scripted group (container) (typed FeaturePython)
  n = 0.003
FEATURE [App::DocumentObjectGroupPython] Cl_element027  label="Cl_element : 0.591"  # scripted group (container) (typed FeaturePython)
  n = 0.002
FEATURE [App::DocumentObjectGroupPython] K_element012  label="K_element : 0.018"  # scripted group (container) (typed FeaturePython)
  n = 0.002
FEATURE [App::DocumentObjectGroupPython] G4_TISSUE_SOFT_ICRP  # scripted group (container) (typed FeaturePython)
  Dunit = g/cm3
  Dvalue = 1.03
  Group = -> [H_element100,C_element110,N_element042,O_element094,Na_element019,P_element011,S_element022,Cl_element027,K_element012]
  conduct = 2
  density = 1
  expand = 3
  formula = G4_TISSUE_SOFT_ICRP
  name = G4_TISSUE_SOFT_ICRP
  specific = 4
FEATURE [App::DocumentObjectGroupPython] H_element101  label="H_element : 0.148"  # scripted group (container) (typed FeaturePython)
  n = 0.101
FEATURE [App::DocumentObjectGroupPython] C_element111  label="C_element : 0.111"  # scripted group (container) (typed FeaturePython)
  n = 0.111
FEATURE [App::DocumentObjectGroupPython] N_element043  label="N_element : 0.026"  # scripted group (container) (typed FeaturePython)
  n = 0.026
FEATURE [App::DocumentObjectGroupPython] O_element095  label="O_element : 0.762"  # scripted group (container) (typed FeaturePython)
  n = 0.762
FEATURE [App::DocumentObjectGroupPython] G4_TISSUE_SOFT_ICRU_4  label="G4_TISSUE_SOFT_ICRU-4"  # scripted group (container) (typed FeaturePython)
  Dunit = g/cm3
  Dvalue = 1
  Group = -> [H_element101,C_element111,N_element043,O_element095]
  conduct = 2
  density = 1
  expand = 3
  formula = G4_TISSUE_SOFT_ICRU-4
  name = G4_TISSUE_SOFT_ICRU-4
  specific = 4
FEATURE [App::DocumentObjectGroupPython] H_element102  label="H_element : 0.149"  # scripted group (container) (typed FeaturePython)
  n = 0.101869
FEATURE [App::DocumentObjectGroupPython] C_element112  label="C_element : 0.456"  # scripted group (container) (typed FeaturePython)
  n = 0.456179
FEATURE [App::DocumentObjectGroupPython] N_element044  label="N_element : 0.761"  # scripted group (container) (typed FeaturePython)
  n = 0.035172
FEATURE [App::DocumentObjectGroupPython] O_element096  label="O_element : 0.407"  # scripted group (container) (typed FeaturePython)
  n = 0.40678
FEATURE [App::DocumentObjectGroupPython] G4_TISSUE_METHANE  label="G4_TISSUE-METHANE"  # scripted group (container) (typed FeaturePython)
  Dunit = g/cm3
  Dvalue = 0.00106409
  Group = -> [H_element102,C_element112,N_element044,O_element096]
  conduct = 2
  density = 1
  expand = 3
  formula = G4_TISSUE-METHANE
  name = G4_TISSUE-METHANE
  specific = 4
FEATURE [App::DocumentObjectGroupPython] H_element103  label="H_element : 0.103"  # scripted group (container) (typed FeaturePython)
  n = 0.102672
FEATURE [App::DocumentObjectGroupPython] C_element113  label="C_element : 0.569"  # scripted group (container) (typed FeaturePython)
  n = 0.56894
FEATURE [App::DocumentObjectGroupPython] N_element045  label="N_element : 0.762"  # scripted group (container) (typed FeaturePython)
  n = 0.035022
FEATURE [App::DocumentObjectGroupPython] O_element097  label="O_element : 0.293"  # scripted group (container) (typed FeaturePython)
  n = 0.293366
FEATURE [App::DocumentObjectGroupPython] G4_TISSUE_PROPANE  label="G4_TISSUE-PROPANE"  # scripted group (container) (typed FeaturePython)
  Dunit = g/cm3
  Dvalue = 0.00182628
  Group = -> [H_element103,C_element113,N_element045,O_element097]
  conduct = 2
  density = 1
  expand = 3
  formula = G4_TISSUE-PROPANE
  name = G4_TISSUE-PROPANE
  specific = 4
FEATURE [App::DocumentObjectGroupPython] Ti_element003  label="Ti_element : 1"  # scripted group (container) (typed FeaturePython)
  n = 1
  ref = Ti_element
FEATURE [App::DocumentObjectGroupPython] O_element098  label="O_element : 052"  # scripted group (container) (typed FeaturePython)
  n = 2
  ref = O_element
FEATURE [App::DocumentObjectGroupPython] G4_TITANIUM_DIOXIDE  # scripted group (container) (typed FeaturePython)
  Dunit = g/cm3
  Dvalue = 4.26
  Group = -> [Ti_element003,O_element098]
  conduct = 2
  density = 1
  expand = 3
  formula = G4_TITANIUM_DIOXIDE
  name = G4_TITANIUM_DIOXIDE
  specific = 4
FEATURE [App::DocumentObjectGroupPython] C_element114  label="C_element : 061"  # scripted group (container) (typed FeaturePython)
  n = 7
  ref = C_element
FEATURE [App::DocumentObjectGroupPython] H_element104  label="H_element : 055"  # scripted group (container) (typed FeaturePython)
  n = 8
  ref = H_element
FEATURE [App::DocumentObjectGroupPython] G4_TOLUENE  # scripted group (container) (typed FeaturePython)
  Dunit = g/cm3
  Dvalue = 0.8669
  Group = -> [C_element114,H_element104]
  conduct = 2
  density = 1
  expand = 3
  formula = G4_TOLUENE
  name = G4_TOLUENE
  specific = 4
FEATURE [App::DocumentObjectGroupPython] C_element115  label="C_element : 062"  # scripted group (container) (typed FeaturePython)
  n = 2
  ref = C_element
FEATURE [App::DocumentObjectGroupPython] H_element105  label="H_element : 056"  # scripted group (container) (typed FeaturePython)
  n = 1
  ref = H_element
FEATURE [App::DocumentObjectGroupPython] Cl_element028  label="Cl_element : 014"  # scripted group (container) (typed FeaturePython)
  n = 3
  ref = Cl_element
FEATURE [App::DocumentObjectGroupPython] G4_TRICHLOROETHYLENE  # scripted group (container) (typed FeaturePython)
  Dunit = g/cm3
  Dvalue = 1.46
  Group = -> [C_element115,H_element105,Cl_element028]
  conduct = 2
  density = 1
  expand = 3
  formula = G4_TRICHLOROETHYLENE
  name = G4_TRICHLOROETHYLENE
  specific = 4
FEATURE [App::DocumentObjectGroupPython] C_element116  label="C_element : 063"  # scripted group (container) (typed FeaturePython)
  n = 6
  ref = C_element
FEATURE [App::DocumentObjectGroupPython] H_element106  label="H_element : 15"  # scripted group (container) (typed FeaturePython)
  n = 15
  ref = H_element
FEATURE [App::DocumentObjectGroupPython] O_element099  label="O_element : 053"  # scripted group (container) (typed FeaturePython)
  n = 4
  ref = O_element
FEATURE [App::DocumentObjectGroupPython] P_element012  label="P_element : 1"  # scripted group (container) (typed FeaturePython)
  n = 1
  ref = P_element
FEATURE [App::DocumentObjectGroupPython] G4_TRIETHYL_PHOSPHATE  # scripted group (container) (typed FeaturePython)
  Dunit = g/cm3
  Dvalue = 1.07
  Group = -> [C_element116,H_element106,O_element099,P_element012]
  conduct = 2
  density = 1
  expand = 3
  formula = G4_TRIETHYL_PHOSPHATE
  name = G4_TRIETHYL_PHOSPHATE
  specific = 4
FEATURE [App::DocumentObjectGroupPython] W_element003  label="W_element : 003"  # scripted group (container) (typed FeaturePython)
  n = 1
  ref = W_element
FEATURE [App::DocumentObjectGroupPython] F_element017  label="F_element : 6"  # scripted group (container) (typed FeaturePython)
  n = 6
  ref = F_element
FEATURE [App::DocumentObjectGroupPython] G4_TUNGSTEN_HEXAFLUORIDE  # scripted group (container) (typed FeaturePython)
  Dunit = g/cm3
  Dvalue = 2.4
  Group = -> [W_element003,F_element017]
  conduct = 2
  density = 1
  expand = 3
  formula = G4_TUNGSTEN_HEXAFLUORIDE
  name = G4_TUNGSTEN_HEXAFLUORIDE
  specific = 4
FEATURE [App::DocumentObjectGroupPython] U_element001  label="U_element : 1"  # scripted group (container) (typed FeaturePython)
  n = 1
  ref = U_element
FEATURE [App::DocumentObjectGroupPython] C_element117  label="C_element : 064"  # scripted group (container) (typed FeaturePython)
  n = 2
  ref = C_element
FEATURE [App::DocumentObjectGroupPython] G4_URANIUM_DICARBIDE  # scripted group (container) (typed FeaturePython)
  Dunit = g/cm3
  Dvalue = 11.28
  Group = -> [U_element001,C_element117]
  conduct = 2
  density = 1
  expand = 3
  formula = G4_URANIUM_DICARBIDE
  name = G4_URANIUM_DICARBIDE
  specific = 4
FEATURE [App::DocumentObjectGroupPython] U_element002  label="U_element : 002"  # scripted group (container) (typed FeaturePython)
  n = 1
  ref = U_element
FEATURE [App::DocumentObjectGroupPython] C_element118  label="C_element : 065"  # scripted group (container) (typed FeaturePython)
  n = 1
  ref = C_element
FEATURE [App::DocumentObjectGroupPython] G4_URANIUM_MONOCARBIDE  # scripted group (container) (typed FeaturePython)
  Dunit = g/cm3
  Dvalue = 13.63
  Group = -> [U_element002,C_element118]
  conduct = 2
  density = 1
  expand = 3
  formula = G4_URANIUM_MONOCARBIDE
  name = G4_URANIUM_MONOCARBIDE
  specific = 4
FEATURE [App::DocumentObjectGroupPython] U_element003  label="U_element : 003"  # scripted group (container) (typed FeaturePython)
  n = 1
  ref = U_element
FEATURE [App::DocumentObjectGroupPython] O_element100  label="O_element : 054"  # scripted group (container) (typed FeaturePython)
  n = 2
  ref = O_element
FEATURE [App::DocumentObjectGroupPython] G4_URANIUM_OXIDE  # scripted group (container) (typed FeaturePython)
  Dunit = g/cm3
  Dvalue = 10.96
  Group = -> [U_element003,O_element100]
  conduct = 2
  density = 1
  expand = 3
  formula = G4_URANIUM_OXIDE
  name = G4_URANIUM_OXIDE
  specific = 4
FEATURE [App::DocumentObjectGroupPython] C_element119  label="C_element : 066"  # scripted group (container) (typed FeaturePython)
  n = 1
  ref = C_element
FEATURE [App::DocumentObjectGroupPython] H_element107  label="H_element : 057"  # scripted group (container) (typed FeaturePython)
  n = 4
  ref = H_element
FEATURE [App::DocumentObjectGroupPython] N_element046  label="N_element : 019"  # scripted group (container) (typed FeaturePython)
  n = 2
  ref = N_element
FEATURE [App::DocumentObjectGroupPython] O_element101  label="O_element : 055"  # scripted group (container) (typed FeaturePython)
  n = 1
  ref = O_element
FEATURE [App::DocumentObjectGroupPython] G4_UREA  # scripted group (container) (typed FeaturePython)
  Dunit = g/cm3
  Dvalue = 1.323
  Group = -> [C_element119,H_element107,N_element046,O_element101]
  conduct = 2
  density = 1
  expand = 3
  formula = G4_UREA
  name = G4_UREA
  specific = 4
FEATURE [App::DocumentObjectGroupPython] C_element120  label="C_element : 067"  # scripted group (container) (typed FeaturePython)
  n = 5
  ref = C_element
FEATURE [App::DocumentObjectGroupPython] H_element108  label="H_element : 058"  # scripted group (container) (typed FeaturePython)
  n = 11
  ref = H_element
FEATURE [App::DocumentObjectGroupPython] N_element047  label="N_element : 020"  # scripted group (container) (typed FeaturePython)
  n = 1
  ref = N_element
FEATURE [App::DocumentObjectGroupPython] O_element102  label="O_element : 056"  # scripted group (container) (typed FeaturePython)
  n = 2
  ref = O_element
FEATURE [App::DocumentObjectGroupPython] G4_VALINE  # scripted group (container) (typed FeaturePython)
  Dunit = g/cm3
  Dvalue = 1.23
  Group = -> [C_element120,H_element108,N_element047,O_element102]
  conduct = 2
  density = 1
  expand = 3
  formula = G4_VALINE
  name = G4_VALINE
  specific = 4
FEATURE [App::DocumentObjectGroupPython] H_element109  label="H_element : 0.009"  # scripted group (container) (typed FeaturePython)
  n = 0.009417
FEATURE [App::DocumentObjectGroupPython] C_element121  label="C_element : 0.281"  # scripted group (container) (typed FeaturePython)
  n = 0.280555
FEATURE [App::DocumentObjectGroupPython] F_element018  label="F_element : 0.710"  # scripted group (container) (typed FeaturePython)
  n = 0.710028
FEATURE [App::DocumentObjectGroupPython] G4_VITON  # scripted group (container) (typed FeaturePython)
  Dunit = g/cm3
  Dvalue = 1.8
  Group = -> [H_element109,C_element121,F_element018]
  conduct = 2
  density = 1
  expand = 3
  formula = G4_VITON
  name = G4_VITON
  specific = 4
FEATURE [App::DocumentObjectGroupPython] H_element110  label="H_element : 059"  # scripted group (container) (typed FeaturePython)
  n = 2
  ref = H_element
FEATURE [App::DocumentObjectGroupPython] O_element103  label="O_element : 057"  # scripted group (container) (typed FeaturePython)
  n = 1
  ref = O_element
FEATURE [App::DocumentObjectGroupPython] G4_WATER  # scripted group (container) (typed FeaturePython)
  Dunit = g/cm3
  Dvalue = 1
  Group = -> [H_element110,O_element103]
  conduct = 2
  density = 1
  expand = 3
  formula = G4_WATER
  name = G4_WATER
  specific = 4
FEATURE [App::DocumentObjectGroupPython] H_element111  label="H_element : 060"  # scripted group (container) (typed FeaturePython)
  n = 2
  ref = H_element
FEATURE [App::DocumentObjectGroupPython] O_element104  label="O_element : 058"  # scripted group (container) (typed FeaturePython)
  n = 1
  ref = O_element
FEATURE [App::DocumentObjectGroupPython] G4_WATER_VAPOR  # scripted group (container) (typed FeaturePython)
  Dunit = g/cm3
  Dvalue = 0.000756182
  Group = -> [H_element111,O_element104]
  conduct = 2
  density = 1
  expand = 3
  formula = G4_WATER_VAPOR
  name = G4_WATER_VAPOR
  specific = 4
FEATURE [App::DocumentObjectGroupPython] C_element122  label="C_element : 068"  # scripted group (container) (typed FeaturePython)
  n = 8
  ref = C_element
FEATURE [App::DocumentObjectGroupPython] H_element112  label="H_element : 061"  # scripted group (container) (typed FeaturePython)
  n = 10
  ref = H_element
FEATURE [App::DocumentObjectGroupPython] G4_XYLENE  # scripted group (container) (typed FeaturePython)
  Dunit = g/cm3
  Dvalue = 0.87
  Group = -> [C_element122,H_element112]
  conduct = 2
  density = 1
  expand = 3
  formula = G4_XYLENE
  name = G4_XYLENE
  specific = 4
FEATURE [App::DocumentObjectGroupPython] C_element123  label="C_element : 069"  # scripted group (container) (typed FeaturePython)
  n = 1
  ref = C_element
FEATURE [App::DocumentObjectGroupPython] G4_GRAPHITE  # scripted group (container) (typed FeaturePython)
  Dunit = g/cm3
  Dvalue = 2.21
  Group = -> [C_element123]
  conduct = 2
  density = 1
  expand = 3
  formula = G4_GRAPHITE
  name = G4_GRAPHITE
  specific = 4
FEATURE [App::DocumentObjectGroupPython] NIST  # scripted group (container) (typed FeaturePython)
  Group = -> [G4_A_150_TISSUE,G4_ACETONE,G4_ACETYLENE,G4_ADENINE,G4_ADIPOSE_TISSUE_ICRP,G4_AIR,G4_ALANINE,G4_ALUMINUM_OXIDE,G4_AMBER,G4_AMMONIA,G4_ANILINE,G4_ANTHRACENE,G4_B_100_BONE,G4_BAKELITE,G4_BARIUM_FLUORIDE,G4_BARIUM_SULFATE,G4_BENZENE,G4_BERYLLIUM_OXIDE,G4_BGO,G4_BLOOD_ICRP,G4_BONE_COMPACT_ICRU,G4_BONE_CORTICAL_ICRP,G4_BORON_CARBIDE,G4_BORON_OXIDE,G4_BRAIN_ICRP,G4_BUTANE,G4_N_BUTYL_ALCOHOL,G4_C_552,+152 more]
FEATURE [App::DocumentObjectGroupPython] H_element113  label="H_element : 062"  # scripted group (container) (typed FeaturePython)
  n = 1
  ref = H_element
FEATURE [App::DocumentObjectGroupPython] G4_H  # scripted group (container) (typed FeaturePython)
  Dunit = g/cm3
  Dvalue = 8.3748e-05
  Group = -> [H_element113]
  conduct = 2
  density = 1
  expand = 3
  formula = H
  name = G4_H
  specific = 4
FEATURE [App::DocumentObjectGroupPython] He_element001  label="He_element : 1"  # scripted group (container) (typed FeaturePython)
  n = 1
  ref = He_element
FEATURE [App::DocumentObjectGroupPython] G4_He  # scripted group (container) (typed FeaturePython)
  Dunit = g/cm3
  Dvalue = 0.000166322
  Group = -> [He_element001]
  conduct = 2
  density = 1
  expand = 3
  formula = He
  name = G4_He
  specific = 4
FEATURE [App::DocumentObjectGroupPython] Li_element008  label="Li_element : 008"  # scripted group (container) (typed FeaturePython)
  n = 1
  ref = Li_element
FEATURE [App::DocumentObjectGroupPython] G4_Li  # scripted group (container) (typed FeaturePython)
  Dunit = g/cm3
  Dvalue = 0.534
  Group = -> [Li_element008]
  conduct = 2
  density = 1
  expand = 3
  formula = Li
  name = G4_Li
  specific = 4
FEATURE [App::DocumentObjectGroupPython] Be_element002  label="Be_element : 002"  # scripted group (container) (typed FeaturePython)
  n = 1
  ref = Be_element
FEATURE [App::DocumentObjectGroupPython] G4_Be  # scripted group (container) (typed FeaturePython)
  Dunit = g/cm3
  Dvalue = 1.848
  Group = -> [Be_element002]
  conduct = 2
  density = 1
  expand = 3
  formula = Be
  name = G4_Be
  specific = 4
FEATURE [App::DocumentObjectGroupPython] B_element007  label="B_element : 007"  # scripted group (container) (typed FeaturePython)
  n = 1
  ref = B_element
FEATURE [App::DocumentObjectGroupPython] G4_B  # scripted group (container) (typed FeaturePython)
  Dunit = g/cm3
  Dvalue = 2.37
  Group = -> [B_element007]
  conduct = 2
  density = 1
  expand = 3
  formula = B
  name = G4_B
  specific = 4
FEATURE [App::DocumentObjectGroupPython] C_element124  label="C_element : 070"  # scripted group (container) (typed FeaturePython)
  n = 1
  ref = C_element
FEATURE [App::DocumentObjectGroupPython] G4_C  # scripted group (container) (typed FeaturePython)
  Dunit = g/cm3
  Dvalue = 2
  Group = -> [C_element124]
  conduct = 2
  density = 1
  expand = 3
  formula = C
  name = G4_C
  specific = 4
FEATURE [App::DocumentObjectGroupPython] N_element048  label="N_element : 021"  # scripted group (container) (typed FeaturePython)
  n = 1
  ref = N_element
FEATURE [App::DocumentObjectGroupPython] G4_N  # scripted group (container) (typed FeaturePython)
  Dunit = g/cm3
  Dvalue = 0.0011652
  Group = -> [N_element048]
  conduct = 2
  density = 1
  expand = 3
  formula = N
  name = G4_N
  specific = 4
FEATURE [App::DocumentObjectGroupPython] O_element105  label="O_element : 059"  # scripted group (container) (typed FeaturePython)
  n = 1
  ref = O_element
FEATURE [App::DocumentObjectGroupPython] G4_O  # scripted group (container) (typed FeaturePython)
  Dunit = g/cm3
  Dvalue = 0.00133151
  Group = -> [O_element105]
  conduct = 2
  density = 1
  expand = 3
  formula = O
  name = G4_O
  specific = 4
FEATURE [App::DocumentObjectGroupPython] F_element019  label="F_element : 008"  # scripted group (container) (typed FeaturePython)
  n = 1
  ref = F_element
FEATURE [App::DocumentObjectGroupPython] G4_F  # scripted group (container) (typed FeaturePython)
  Dunit = g/cm3
  Dvalue = 0.00158029
  Group = -> [F_element019]
  conduct = 2
  density = 1
  expand = 3
  formula = F
  name = G4_F
  specific = 4
FEATURE [App::DocumentObjectGroupPython] Ne_element001  label="Ne_element : 1"  # scripted group (container) (typed FeaturePython)
  n = 1
  ref = Ne_element
FEATURE [App::DocumentObjectGroupPython] G4_Ne  # scripted group (container) (typed FeaturePython)
  Dunit = g/cm3
  Dvalue = 0.000838505
  Group = -> [Ne_element001]
  conduct = 2
  density = 1
  expand = 3
  formula = Ne
  name = G4_Ne
  specific = 4
FEATURE [App::DocumentObjectGroupPython] Na_element020  label="Na_element : 005"  # scripted group (container) (typed FeaturePython)
  n = 1
  ref = Na_element
FEATURE [App::DocumentObjectGroupPython] G4_Na  # scripted group (container) (typed FeaturePython)
  Dunit = g/cm3
  Dvalue = 0.971
  Group = -> [Na_element020]
  conduct = 2
  density = 1
  expand = 3
  formula = Na
  name = G4_Na
  specific = 4
FEATURE [App::DocumentObjectGroupPython] Mg_element011  label="Mg_element : 005"  # scripted group (container) (typed FeaturePython)
  n = 1
  ref = Mg_element
FEATURE [App::DocumentObjectGroupPython] G4_Mg  # scripted group (container) (typed FeaturePython)
  Dunit = g/cm3
  Dvalue = 1.74
  Group = -> [Mg_element011]
  conduct = 2
  density = 1
  expand = 3
  formula = Mg
  name = G4_Mg
  specific = 4
FEATURE [App::DocumentObjectGroupPython] Al_element004  label="Al_element : 1"  # scripted group (container) (typed FeaturePython)
  n = 1
  ref = Al_element
FEATURE [App::DocumentObjectGroupPython] G4_Al  # scripted group (container) (typed FeaturePython)
  Dunit = g/cm3
  Dvalue = 2.699
  Group = -> [Al_element004]
  conduct = 2
  density = 1
  expand = 3
  formula = Al
  name = G4_Al
  specific = 4
FEATURE [App::DocumentObjectGroupPython] Si_element007  label="Si_element : 002"  # scripted group (container) (typed FeaturePython)
  n = 1
  ref = Si_element
FEATURE [App::DocumentObjectGroupPython] G4_Si  # scripted group (container) (typed FeaturePython)
  Dunit = g/cm3
  Dvalue = 2.33
  Group = -> [Si_element007]
  conduct = 2
  density = 1
  expand = 3
  formula = Si
  name = G4_Si
  specific = 4
FEATURE [App::DocumentObjectGroupPython] P_element013  label="P_element : 002"  # scripted group (container) (typed FeaturePython)
  n = 1
  ref = P_element
FEATURE [App::DocumentObjectGroupPython] G4_P  # scripted group (container) (typed FeaturePython)
  Dunit = g/cm3
  Dvalue = 2.2
  Group = -> [P_element013]
  conduct = 2
  density = 1
  expand = 3
  formula = P
  name = G4_P
  specific = 4
FEATURE [App::DocumentObjectGroupPython] S_element023  label="S_element : 007"  # scripted group (container) (typed FeaturePython)
  n = 1
  ref = S_element
FEATURE [App::DocumentObjectGroupPython] G4_S  # scripted group (container) (typed FeaturePython)
  Dunit = g/cm3
  Dvalue = 2
  Group = -> [S_element023]
  conduct = 2
  density = 1
  expand = 3
  formula = S
  name = G4_S
  specific = 4
FEATURE [App::DocumentObjectGroupPython] Cl_element029  label="Cl_element : 015"  # scripted group (container) (typed FeaturePython)
  n = 1
  ref = Cl_element
FEATURE [App::DocumentObjectGroupPython] G4_Cl  # scripted group (container) (typed FeaturePython)
  Dunit = g/cm3
  Dvalue = 0.00299473
  Group = -> [Cl_element029]
  conduct = 2
  density = 1
  expand = 3
  formula = Cl
  name = G4_Cl
  specific = 4
FEATURE [App::DocumentObjectGroupPython] Ar_element002  label="Ar_element : 1"  # scripted group (container) (typed FeaturePython)
  n = 1
  ref = Ar_element
FEATURE [App::DocumentObjectGroupPython] G4_Ar  # scripted group (container) (typed FeaturePython)
  Dunit = g/cm3
  Dvalue = 0.00166201
  Group = -> [Ar_element002]
  conduct = 2
  density = 1
  expand = 3
  formula = Ar
  name = G4_Ar
  specific = 4
FEATURE [App::DocumentObjectGroupPython] K_element013  label="K_element : 003"  # scripted group (container) (typed FeaturePython)
  n = 1
  ref = K_element
FEATURE [App::DocumentObjectGroupPython] G4_K  # scripted group (container) (typed FeaturePython)
  Dunit = g/cm3
  Dvalue = 0.862
  Group = -> [K_element013]
  conduct = 2
  density = 1
  expand = 3
  formula = K
  name = G4_K
  specific = 4
FEATURE [App::DocumentObjectGroupPython] Ca_element014  label="Ca_element : 007"  # scripted group (container) (typed FeaturePython)
  n = 1
  ref = Ca_element
FEATURE [App::DocumentObjectGroupPython] G4_Ca  # scripted group (container) (typed FeaturePython)
  Dunit = g/cm3
  Dvalue = 1.55
  Group = -> [Ca_element014]
  conduct = 2
  density = 1
  expand = 3
  formula = Ca
  name = G4_Ca
  specific = 4
FEATURE [App::DocumentObjectGroupPython] Sc_element001  label="Sc_element : 1"  # scripted group (container) (typed FeaturePython)
  n = 1
  ref = Sc_element
FEATURE [App::DocumentObjectGroupPython] G4_Sc  # scripted group (container) (typed FeaturePython)
  Dunit = g/cm3
  Dvalue = 2.989
  Group = -> [Sc_element001]
  conduct = 2
  density = 1
  expand = 3
  formula = Sc
  name = G4_Sc
  specific = 4
FEATURE [App::DocumentObjectGroupPython] Ti_element004  label="Ti_element : 002"  # scripted group (container) (typed FeaturePython)
  n = 1
  ref = Ti_element
FEATURE [App::DocumentObjectGroupPython] G4_Ti  # scripted group (container) (typed FeaturePython)
  Dunit = g/cm3
  Dvalue = 4.54
  Group = -> [Ti_element004]
  conduct = 2
  density = 1
  expand = 3
  formula = Ti
  name = G4_Ti
  specific = 4
FEATURE [App::DocumentObjectGroupPython] V_element001  label="V_element : 1"  # scripted group (container) (typed FeaturePython)
  n = 1
  ref = V_element
FEATURE [App::DocumentObjectGroupPython] G4_V  # scripted group (container) (typed FeaturePython)
  Dunit = g/cm3
  Dvalue = 6.11
  Group = -> [V_element001]
  conduct = 2
  density = 1
  expand = 3
  formula = V
  name = G4_V
  specific = 4
FEATURE [App::DocumentObjectGroupPython] Cr_element001  label="Cr_element : 1"  # scripted group (container) (typed FeaturePython)
  n = 1
  ref = Cr_element
FEATURE [App::DocumentObjectGroupPython] G4_Cr  # scripted group (container) (typed FeaturePython)
  Dunit = g/cm3
  Dvalue = 7.18
  Group = -> [Cr_element001]
  conduct = 2
  density = 1
  expand = 3
  formula = Cr
  name = G4_Cr
  specific = 4
FEATURE [App::DocumentObjectGroupPython] Mn_element001  label="Mn_element : 1"  # scripted group (container) (typed FeaturePython)
  n = 1
  ref = Mn_element
FEATURE [App::DocumentObjectGroupPython] G4_Mn  # scripted group (container) (typed FeaturePython)
  Dunit = g/cm3
  Dvalue = 7.44
  Group = -> [Mn_element001]
  conduct = 2
  density = 1
  expand = 3
  formula = Mn
  name = G4_Mn
  specific = 4
FEATURE [App::DocumentObjectGroupPython] Fe_element007  label="Fe_element : 004"  # scripted group (container) (typed FeaturePython)
  n = 1
  ref = Fe_element
FEATURE [App::DocumentObjectGroupPython] G4_Fe  # scripted group (container) (typed FeaturePython)
  Dunit = g/cm3
  Dvalue = 7.874
  Group = -> [Fe_element007]
  conduct = 2
  density = 1
  expand = 3
  formula = Fe
  name = G4_Fe
  specific = 4
FEATURE [App::DocumentObjectGroupPython] Co_element001  label="Co_element : 1"  # scripted group (container) (typed FeaturePython)
  n = 1
  ref = Co_element
FEATURE [App::DocumentObjectGroupPython] G4_Co  # scripted group (container) (typed FeaturePython)
  Dunit = g/cm3
  Dvalue = 8.9
  Group = -> [Co_element001]
  conduct = 2
  density = 1
  expand = 3
  formula = Co
  name = G4_Co
  specific = 4
FEATURE [App::DocumentObjectGroupPython] Ni_element001  label="Ni_element : 1"  # scripted group (container) (typed FeaturePython)
  n = 1
  ref = Ni_element
FEATURE [App::DocumentObjectGroupPython] G4_Ni  # scripted group (container) (typed FeaturePython)
  Dunit = g/cm3
  Dvalue = 8.902
  Group = -> [Ni_element001]
  conduct = 2
  density = 1
  expand = 3
  formula = Ni
  name = G4_Ni
  specific = 4
FEATURE [App::DocumentObjectGroupPython] Cu_element001  label="Cu_element : 1"  # scripted group (container) (typed FeaturePython)
  n = 1
  ref = Cu_element
FEATURE [App::DocumentObjectGroupPython] G4_Cu  # scripted group (container) (typed FeaturePython)
  Dunit = g/cm3
  Dvalue = 8.96
  Group = -> [Cu_element001]
  conduct = 2
  density = 1
  expand = 3
  formula = Cu
  name = G4_Cu
  specific = 4
FEATURE [App::DocumentObjectGroupPython] Zn_element001  label="Zn_element : 1"  # scripted group (container) (typed FeaturePython)
  n = 1
  ref = Zn_element
FEATURE [App::DocumentObjectGroupPython] G4_Zn  # scripted group (container) (typed FeaturePython)
  Dunit = g/cm3
  Dvalue = 7.133
  Group = -> [Zn_element001]
  conduct = 2
  density = 1
  expand = 3
  formula = Zn
  name = G4_Zn
  specific = 4
FEATURE [App::DocumentObjectGroupPython] Ga_element002  label="Ga_element : 002"  # scripted group (container) (typed FeaturePython)
  n = 1
  ref = Ga_element
FEATURE [App::DocumentObjectGroupPython] G4_Ga  # scripted group (container) (typed FeaturePython)
  Dunit = g/cm3
  Dvalue = 5.904
  Group = -> [Ga_element002]
  conduct = 2
  density = 1
  expand = 3
  formula = Ga
  name = G4_Ga
  specific = 4
FEATURE [App::DocumentObjectGroupPython] Ge_element002  label="Ge_element : 1"  # scripted group (container) (typed FeaturePython)
  n = 1
  ref = Ge_element
FEATURE [App::DocumentObjectGroupPython] G4_Ge  # scripted group (container) (typed FeaturePython)
  Dunit = g/cm3
  Dvalue = 5.323
  Group = -> [Ge_element002]
  conduct = 2
  density = 1
  expand = 3
  formula = Ge
  name = G4_Ge
  specific = 4
FEATURE [App::DocumentObjectGroupPython] As_element003  label="As_element : 002"  # scripted group (container) (typed FeaturePython)
  n = 1
  ref = As_element
FEATURE [App::DocumentObjectGroupPython] G4_As  # scripted group (container) (typed FeaturePython)
  Dunit = g/cm3
  Dvalue = 5.73
  Group = -> [As_element003]
  conduct = 2
  density = 1
  expand = 3
  formula = As
  name = G4_As
  specific = 4
FEATURE [App::DocumentObjectGroupPython] Se_element001  label="Se_element : 1"  # scripted group (container) (typed FeaturePython)
  n = 1
  ref = Se_element
FEATURE [App::DocumentObjectGroupPython] G4_Se  # scripted group (container) (typed FeaturePython)
  Dunit = g/cm3
  Dvalue = 4.5
  Group = -> [Se_element001]
  conduct = 2
  density = 1
  expand = 3
  formula = Se
  name = G4_Se
  specific = 4
FEATURE [App::DocumentObjectGroupPython] Br_element007  label="Br_element : 004"  # scripted group (container) (typed FeaturePython)
  n = 1
  ref = Br_element
FEATURE [App::DocumentObjectGroupPython] G4_Br  # scripted group (container) (typed FeaturePython)
  Dunit = g/cm3
  Dvalue = 0.0070721
  Group = -> [Br_element007]
  conduct = 2
  density = 1
  expand = 3
  formula = Br
  name = G4_Br
  specific = 4
FEATURE [App::DocumentObjectGroupPython] Kr_element001  label="Kr_element : 1"  # scripted group (container) (typed FeaturePython)
  n = 1
  ref = Kr_element
FEATURE [App::DocumentObjectGroupPython] G4_Kr  # scripted group (container) (typed FeaturePython)
  Dunit = g/cm3
  Dvalue = 0.00347832
  Group = -> [Kr_element001]
  conduct = 2
  density = 1
  expand = 3
  formula = Kr
  name = G4_Kr
  specific = 4
FEATURE [App::DocumentObjectGroupPython] Rb_element001  label="Rb_element : 1"  # scripted group (container) (typed FeaturePython)
  n = 1
  ref = Rb_element
FEATURE [App::DocumentObjectGroupPython] G4_Rb  # scripted group (container) (typed FeaturePython)
  Dunit = g/cm3
  Dvalue = 1.532
  Group = -> [Rb_element001]
  conduct = 2
  density = 1
  expand = 3
  formula = Rb
  name = G4_Rb
  specific = 4
FEATURE [App::DocumentObjectGroupPython] Sr_element001  label="Sr_element : 1"  # scripted group (container) (typed FeaturePython)
  n = 1
  ref = Sr_element
FEATURE [App::DocumentObjectGroupPython] G4_Sr  # scripted group (container) (typed FeaturePython)
  Dunit = g/cm3
  Dvalue = 2.54
  Group = -> [Sr_element001]
  conduct = 2
  density = 1
  expand = 3
  formula = Sr
  name = G4_Sr
  specific = 4
FEATURE [App::DocumentObjectGroupPython] Y_element001  label="Y_element : 1"  # scripted group (container) (typed FeaturePython)
  n = 1
  ref = Y_element
FEATURE [App::DocumentObjectGroupPython] G4_Y  # scripted group (container) (typed FeaturePython)
  Dunit = g/cm3
  Dvalue = 4.469
  Group = -> [Y_element001]
  conduct = 2
  density = 1
  expand = 3
  formula = Y
  name = G4_Y
  specific = 4
FEATURE [App::DocumentObjectGroupPython] Zr_element001  label="Zr_element : 1"  # scripted group (container) (typed FeaturePython)
  n = 1
  ref = Zr_element
FEATURE [App::DocumentObjectGroupPython] G4_Zr  # scripted group (container) (typed FeaturePython)
  Dunit = g/cm3
  Dvalue = 6.506
  Group = -> [Zr_element001]
  conduct = 2
  density = 1
  expand = 3
  formula = Zr
  name = G4_Zr
  specific = 4
FEATURE [App::DocumentObjectGroupPython] Nb_element001  label="Nb_element : 1"  # scripted group (container) (typed FeaturePython)
  n = 1
  ref = Nb_element
FEATURE [App::DocumentObjectGroupPython] G4_Nb  # scripted group (container) (typed FeaturePython)
  Dunit = g/cm3
  Dvalue = 8.57
  Group = -> [Nb_element001]
  conduct = 2
  density = 1
  expand = 3
  formula = Nb
  name = G4_Nb
  specific = 4
FEATURE [App::DocumentObjectGroupPython] Mo_element001  label="Mo_element : 1"  # scripted group (container) (typed FeaturePython)
  n = 1
  ref = Mo_element
FEATURE [App::DocumentObjectGroupPython] G4_Mo  # scripted group (container) (typed FeaturePython)
  Dunit = g/cm3
  Dvalue = 10.22
  Group = -> [Mo_element001]
  conduct = 2
  density = 1
  expand = 3
  formula = Mo
  name = G4_Mo
  specific = 4
FEATURE [App::DocumentObjectGroupPython] Tc_element001  label="Tc_element : 1"  # scripted group (container) (typed FeaturePython)
  n = 1
  ref = Tc_element
FEATURE [App::DocumentObjectGroupPython] G4_Tc  # scripted group (container) (typed FeaturePython)
  Dunit = g/cm3
  Dvalue = 11.5
  Group = -> [Tc_element001]
  conduct = 2
  density = 1
  expand = 3
  formula = Tc
  name = G4_Tc
  specific = 4
FEATURE [App::DocumentObjectGroupPython] Ru_element001  label="Ru_element : 1"  # scripted group (container) (typed FeaturePython)
  n = 1
  ref = Ru_element
FEATURE [App::DocumentObjectGroupPython] G4_Ru  # scripted group (container) (typed FeaturePython)
  Dunit = g/cm3
  Dvalue = 12.41
  Group = -> [Ru_element001]
  conduct = 2
  density = 1
  expand = 3
  formula = Ru
  name = G4_Ru
  specific = 4
FEATURE [App::DocumentObjectGroupPython] Rh_element001  label="Rh_element : 1"  # scripted group (container) (typed FeaturePython)
  n = 1
  ref = Rh_element
FEATURE [App::DocumentObjectGroupPython] G4_Rh  # scripted group (container) (typed FeaturePython)
  Dunit = g/cm3
  Dvalue = 12.41
  Group = -> [Rh_element001]
  conduct = 2
  density = 1
  expand = 3
  formula = Rh
  name = G4_Rh
  specific = 4
FEATURE [App::DocumentObjectGroupPython] Pd_element001  label="Pd_element : 1"  # scripted group (container) (typed FeaturePython)
  n = 1
  ref = Pd_element
FEATURE [App::DocumentObjectGroupPython] G4_Pd  # scripted group (container) (typed FeaturePython)
  Dunit = g/cm3
  Dvalue = 12.02
  Group = -> [Pd_element001]
  conduct = 2
  density = 1
  expand = 3
  formula = Pd
  name = G4_Pd
  specific = 4
FEATURE [App::DocumentObjectGroupPython] Ag_element006  label="Ag_element : 004"  # scripted group (container) (typed FeaturePython)
  n = 1
  ref = Ag_element
FEATURE [App::DocumentObjectGroupPython] G4_Ag  # scripted group (container) (typed FeaturePython)
  Dunit = g/cm3
  Dvalue = 10.5
  Group = -> [Ag_element006]
  conduct = 2
  density = 1
  expand = 3
  formula = Ag
  name = G4_Ag
  specific = 4
FEATURE [App::DocumentObjectGroupPython] Cd_element003  label="Cd_element : 003"  # scripted group (container) (typed FeaturePython)
  n = 1
  ref = Cd_element
FEATURE [App::DocumentObjectGroupPython] G4_Cd  # scripted group (container) (typed FeaturePython)
  Dunit = g/cm3
  Dvalue = 8.65
  Group = -> [Cd_element003]
  conduct = 2
  density = 1
  expand = 3
  formula = Cd
  name = G4_Cd
  specific = 4
FEATURE [App::DocumentObjectGroupPython] In_element001  label="In_element : 1"  # scripted group (container) (typed FeaturePython)
  n = 1
  ref = In_element
FEATURE [App::DocumentObjectGroupPython] G4_In  # scripted group (container) (typed FeaturePython)
  Dunit = g/cm3
  Dvalue = 7.31
  Group = -> [In_element001]
  conduct = 2
  density = 1
  expand = 3
  formula = In
  name = G4_In
  specific = 4
FEATURE [App::DocumentObjectGroupPython] Sn_element001  label="Sn_element : 1"  # scripted group (container) (typed FeaturePython)
  n = 1
  ref = Sn_element
FEATURE [App::DocumentObjectGroupPython] G4_Sn  # scripted group (container) (typed FeaturePython)
  Dunit = g/cm3
  Dvalue = 7.31
  Group = -> [Sn_element001]
  conduct = 2
  density = 1
  expand = 3
  formula = Sn
  name = G4_Sn
  specific = 4
FEATURE [App::DocumentObjectGroupPython] Sb_element001  label="Sb_element : 1"  # scripted group (container) (typed FeaturePython)
  n = 1
  ref = Sb_element
FEATURE [App::DocumentObjectGroupPython] G4_Sb  # scripted group (container) (typed FeaturePython)
  Dunit = g/cm3
  Dvalue = 6.691
  Group = -> [Sb_element001]
  conduct = 2
  density = 1
  expand = 3
  formula = Sb
  name = G4_Sb
  specific = 4
FEATURE [App::DocumentObjectGroupPython] Te_element002  label="Te_element : 002"  # scripted group (container) (typed FeaturePython)
  n = 1
  ref = Te_element
FEATURE [App::DocumentObjectGroupPython] G4_Te  # scripted group (container) (typed FeaturePython)
  Dunit = g/cm3
  Dvalue = 6.24
  Group = -> [Te_element002]
  conduct = 2
  density = 1
  expand = 3
  formula = Te
  name = G4_Te
  specific = 4
FEATURE [App::DocumentObjectGroupPython] I_element010  label="I_element : 006"  # scripted group (container) (typed FeaturePython)
  n = 1
  ref = I_element
FEATURE [App::DocumentObjectGroupPython] G4_I  # scripted group (container) (typed FeaturePython)
  Dunit = g/cm3
  Dvalue = 4.93
  Group = -> [I_element010]
  conduct = 2
  density = 1
  expand = 3
  formula = I
  name = G4_I
  specific = 4
FEATURE [App::DocumentObjectGroupPython] Xe_element001  label="Xe_element : 1"  # scripted group (container) (typed FeaturePython)
  n = 1
  ref = Xe_element
FEATURE [App::DocumentObjectGroupPython] G4_Xe  # scripted group (container) (typed FeaturePython)
  Dunit = g/cm3
  Dvalue = 0.00548536
  Group = -> [Xe_element001]
  conduct = 2
  density = 1
  expand = 3
  formula = Xe
  name = G4_Xe
  specific = 4
FEATURE [App::DocumentObjectGroupPython] Cs_element003  label="Cs_element : 003"  # scripted group (container) (typed FeaturePython)
  n = 1
  ref = Cs_element
FEATURE [App::DocumentObjectGroupPython] G4_Cs  # scripted group (container) (typed FeaturePython)
  Dunit = g/cm3
  Dvalue = 1.873
  Group = -> [Cs_element003]
  conduct = 2
  density = 1
  expand = 3
  formula = Cs
  name = G4_Cs
  specific = 4
FEATURE [App::DocumentObjectGroupPython] Ba_element003  label="Ba_element : 003"  # scripted group (container) (typed FeaturePython)
  n = 1
  ref = Ba_element
FEATURE [App::DocumentObjectGroupPython] G4_Ba  # scripted group (container) (typed FeaturePython)
  Dunit = g/cm3
  Dvalue = 3.5
  Group = -> [Ba_element003]
  conduct = 2
  density = 1
  expand = 3
  formula = Ba
  name = G4_Ba
  specific = 4
FEATURE [App::DocumentObjectGroupPython] La_element003  label="La_element : 003"  # scripted group (container) (typed FeaturePython)
  n = 1
  ref = La_element
FEATURE [App::DocumentObjectGroupPython] G4_La  # scripted group (container) (typed FeaturePython)
  Dunit = g/cm3
  Dvalue = 6.154
  Group = -> [La_element003]
  conduct = 2
  density = 1
  expand = 3
  formula = La
  name = G4_La
  specific = 4
FEATURE [App::DocumentObjectGroupPython] Ce_element002  label="Ce_element : 1"  # scripted group (container) (typed FeaturePython)
  n = 1
  ref = Ce_element
FEATURE [App::DocumentObjectGroupPython] G4_Ce  # scripted group (container) (typed FeaturePython)
  Dunit = g/cm3
  Dvalue = 6.657
  Group = -> [Ce_element002]
  conduct = 2
  density = 1
  expand = 3
  formula = Ce
  name = G4_Ce
  specific = 4
FEATURE [App::DocumentObjectGroupPython] Pr_element001  label="Pr_element : 1"  # scripted group (container) (typed FeaturePython)
  n = 1
  ref = Pr_element
FEATURE [App::DocumentObjectGroupPython] G4_Pr  # scripted group (container) (typed FeaturePython)
  Dunit = g/cm3
  Dvalue = 6.71
  Group = -> [Pr_element001]
  conduct = 2
  density = 1
  expand = 3
  formula = Pr
  name = G4_Pr
  specific = 4
FEATURE [App::DocumentObjectGroupPython] Nd_element001  label="Nd_element : 1"  # scripted group (container) (typed FeaturePython)
  n = 1
  ref = Nd_element
FEATURE [App::DocumentObjectGroupPython] G4_Nd  # scripted group (container) (typed FeaturePython)
  Dunit = g/cm3
  Dvalue = 6.9
  Group = -> [Nd_element001]
  conduct = 2
  density = 1
  expand = 3
  formula = Nd
  name = G4_Nd
  specific = 4
FEATURE [App::DocumentObjectGroupPython] Pm_element001  label="Pm_element : 1"  # scripted group (container) (typed FeaturePython)
  n = 1
  ref = Pm_element
FEATURE [App::DocumentObjectGroupPython] G4_Pm  # scripted group (container) (typed FeaturePython)
  Dunit = g/cm3
  Dvalue = 7.22
  Group = -> [Pm_element001]
  conduct = 2
  density = 1
  expand = 3
  formula = Pm
  name = G4_Pm
  specific = 4
FEATURE [App::DocumentObjectGroupPython] Sm_element001  label="Sm_element : 1"  # scripted group (container) (typed FeaturePython)
  n = 1
  ref = Sm_element
FEATURE [App::DocumentObjectGroupPython] G4_Sm  # scripted group (container) (typed FeaturePython)
  Dunit = g/cm3
  Dvalue = 7.46
  Group = -> [Sm_element001]
  conduct = 2
  density = 1
  expand = 3
  formula = Sm
  name = G4_Sm
  specific = 4
FEATURE [App::DocumentObjectGroupPython] Eu_element001  label="Eu_element : 1"  # scripted group (container) (typed FeaturePython)
  n = 1
  ref = Eu_element
FEATURE [App::DocumentObjectGroupPython] G4_Eu  # scripted group (container) (typed FeaturePython)
  Dunit = g/cm3
  Dvalue = 5.243
  Group = -> [Eu_element001]
  conduct = 2
  density = 1
  expand = 3
  formula = Eu
  name = G4_Eu
  specific = 4
FEATURE [App::DocumentObjectGroupPython] Gd_element002  label="Gd_element : 1"  # scripted group (container) (typed FeaturePython)
  n = 1
  ref = Gd_element
FEATURE [App::DocumentObjectGroupPython] G4_Gd  # scripted group (container) (typed FeaturePython)
  Dunit = g/cm3
  Dvalue = 7.9004
  Group = -> [Gd_element002]
  conduct = 2
  density = 1
  expand = 3
  formula = Gd
  name = G4_Gd
  specific = 4
FEATURE [App::DocumentObjectGroupPython] Tb_element001  label="Tb_element : 1"  # scripted group (container) (typed FeaturePython)
  n = 1
  ref = Tb_element
FEATURE [App::DocumentObjectGroupPython] G4_Tb  # scripted group (container) (typed FeaturePython)
  Dunit = g/cm3
  Dvalue = 8.229
  Group = -> [Tb_element001]
  conduct = 2
  density = 1
  expand = 3
  formula = Tb
  name = G4_Tb
  specific = 4
FEATURE [App::DocumentObjectGroupPython] Dy_element001  label="Dy_element : 1"  # scripted group (container) (typed FeaturePython)
  n = 1
  ref = Dy_element
FEATURE [App::DocumentObjectGroupPython] G4_Dy  # scripted group (container) (typed FeaturePython)
  Dunit = g/cm3
  Dvalue = 8.55
  Group = -> [Dy_element001]
  conduct = 2
  density = 1
  expand = 3
  formula = Dy
  name = G4_Dy
  specific = 4
FEATURE [App::DocumentObjectGroupPython] Ho_element001  label="Ho_element : 1"  # scripted group (container) (typed FeaturePython)
  n = 1
  ref = Ho_element
FEATURE [App::DocumentObjectGroupPython] G4_Ho  # scripted group (container) (typed FeaturePython)
  Dunit = g/cm3
  Dvalue = 8.795
  Group = -> [Ho_element001]
  conduct = 2
  density = 1
  expand = 3
  formula = Ho
  name = G4_Ho
  specific = 4
FEATURE [App::DocumentObjectGroupPython] Er_element001  label="Er_element : 1"  # scripted group (container) (typed FeaturePython)
  n = 1
  ref = Er_element
FEATURE [App::DocumentObjectGroupPython] G4_Er  # scripted group (container) (typed FeaturePython)
  Dunit = g/cm3
  Dvalue = 9.066
  Group = -> [Er_element001]
  conduct = 2
  density = 1
  expand = 3
  formula = Er
  name = G4_Er
  specific = 4
FEATURE [App::DocumentObjectGroupPython] Tm_element001  label="Tm_element : 1"  # scripted group (container) (typed FeaturePython)
  n = 1
  ref = Tm_element
FEATURE [App::DocumentObjectGroupPython] G4_Tm  # scripted group (container) (typed FeaturePython)
  Dunit = g/cm3
  Dvalue = 9.321
  Group = -> [Tm_element001]
  conduct = 2
  density = 1
  expand = 3
  formula = Tm
  name = G4_Tm
  specific = 4
FEATURE [App::DocumentObjectGroupPython] Yb_element001  label="Yb_element : 1"  # scripted group (container) (typed FeaturePython)
  n = 1
  ref = Yb_element
FEATURE [App::DocumentObjectGroupPython] G4_Yb  # scripted group (container) (typed FeaturePython)
  Dunit = g/cm3
  Dvalue = 6.73
  Group = -> [Yb_element001]
  conduct = 2
  density = 1
  expand = 3
  formula = Yb
  name = G4_Yb
  specific = 4
FEATURE [App::DocumentObjectGroupPython] Lu_element001  label="Lu_element : 1"  # scripted group (container) (typed FeaturePython)
  n = 1
  ref = Lu_element
FEATURE [App::DocumentObjectGroupPython] G4_Lu  # scripted group (container) (typed FeaturePython)
  Dunit = g/cm3
  Dvalue = 9.84
  Group = -> [Lu_element001]
  conduct = 2
  density = 1
  expand = 3
  formula = Lu
  name = G4_Lu
  specific = 4
FEATURE [App::DocumentObjectGroupPython] Hf_element001  label="Hf_element : 1"  # scripted group (container) (typed FeaturePython)
  n = 1
  ref = Hf_element
FEATURE [App::DocumentObjectGroupPython] G4_Hf  # scripted group (container) (typed FeaturePython)
  Dunit = g/cm3
  Dvalue = 13.31
  Group = -> [Hf_element001]
  conduct = 2
  density = 1
  expand = 3
  formula = Hf
  name = G4_Hf
  specific = 4
FEATURE [App::DocumentObjectGroupPython] Ta_element001  label="Ta_element : 1"  # scripted group (container) (typed FeaturePython)
  n = 1
  ref = Ta_element
FEATURE [App::DocumentObjectGroupPython] G4_Ta  # scripted group (container) (typed FeaturePython)
  Dunit = g/cm3
  Dvalue = 16.654
  Group = -> [Ta_element001]
  conduct = 2
  density = 1
  expand = 3
  formula = Ta
  name = G4_Ta
  specific = 4
FEATURE [App::DocumentObjectGroupPython] W_element004  label="W_element : 004"  # scripted group (container) (typed FeaturePython)
  n = 1
  ref = W_element
FEATURE [App::DocumentObjectGroupPython] G4_W  # scripted group (container) (typed FeaturePython)
  Dunit = g/cm3
  Dvalue = 19.3
  Group = -> [W_element004]
  conduct = 2
  density = 1
  expand = 3
  formula = W
  name = G4_W
  specific = 4
FEATURE [App::DocumentObjectGroupPython] Re_element001  label="Re_element : 1"  # scripted group (container) (typed FeaturePython)
  n = 1
  ref = Re_element
FEATURE [App::DocumentObjectGroupPython] G4_Re  # scripted group (container) (typed FeaturePython)
  Dunit = g/cm3
  Dvalue = 21.02
  Group = -> [Re_element001]
  conduct = 2
  density = 1
  expand = 3
  formula = Re
  name = G4_Re
  specific = 4
FEATURE [App::DocumentObjectGroupPython] Os_element001  label="Os_element : 1"  # scripted group (container) (typed FeaturePython)
  n = 1
  ref = Os_element
FEATURE [App::DocumentObjectGroupPython] G4_Os  # scripted group (container) (typed FeaturePython)
  Dunit = g/cm3
  Dvalue = 22.57
  Group = -> [Os_element001]
  conduct = 2
  density = 1
  expand = 3
  formula = Os
  name = G4_Os
  specific = 4
FEATURE [App::DocumentObjectGroupPython] Ir_element001  label="Ir_element : 1"  # scripted group (container) (typed FeaturePython)
  n = 1
  ref = Ir_element
FEATURE [App::DocumentObjectGroupPython] G4_Ir  # scripted group (container) (typed FeaturePython)
  Dunit = g/cm3
  Dvalue = 22.42
  Group = -> [Ir_element001]
  conduct = 2
  density = 1
  expand = 3
  formula = Ir
  name = G4_Ir
  specific = 4
FEATURE [App::DocumentObjectGroupPython] Pt_element001  label="Pt_element : 1"  # scripted group (container) (typed FeaturePython)
  n = 1
  ref = Pt_element
FEATURE [App::DocumentObjectGroupPython] G4_Pt  # scripted group (container) (typed FeaturePython)
  Dunit = g/cm3
  Dvalue = 21.45
  Group = -> [Pt_element001]
  conduct = 2
  density = 1
  expand = 3
  formula = Pt
  name = G4_Pt
  specific = 4
FEATURE [App::DocumentObjectGroupPython] Au_element001  label="Au_element : 1"  # scripted group (container) (typed FeaturePython)
  n = 1
  ref = Au_element
FEATURE [App::DocumentObjectGroupPython] G4_Au  # scripted group (container) (typed FeaturePython)
  Dunit = g/cm3
  Dvalue = 19.32
  Group = -> [Au_element001]
  conduct = 2
  density = 1
  expand = 3
  formula = Au
  name = G4_Au
  specific = 4
FEATURE [App::DocumentObjectGroupPython] Hg_element002  label="Hg_element : 002"  # scripted group (container) (typed FeaturePython)
  n = 1
  ref = Hg_element
FEATURE [App::DocumentObjectGroupPython] G4_Hg  # scripted group (container) (typed FeaturePython)
  Dunit = g/cm3
  Dvalue = 13.546
  Group = -> [Hg_element002]
  conduct = 2
  density = 1
  expand = 3
  formula = Hg
  name = G4_Hg
  specific = 4
FEATURE [App::DocumentObjectGroupPython] Tl_element002  label="Tl_element : 002"  # scripted group (container) (typed FeaturePython)
  n = 1
  ref = Tl_element
FEATURE [App::DocumentObjectGroupPython] G4_Tl  # scripted group (container) (typed FeaturePython)
  Dunit = g/cm3
  Dvalue = 11.72
  Group = -> [Tl_element002]
  conduct = 2
  density = 1
  expand = 3
  formula = Tl
  name = G4_Tl
  specific = 4
FEATURE [App::DocumentObjectGroupPython] Pb_element003  label="Pb_element : 1"  # scripted group (container) (typed FeaturePython)
  n = 1
  ref = Pb_element
FEATURE [App::DocumentObjectGroupPython] G4_Pb  # scripted group (container) (typed FeaturePython)
  Dunit = g/cm3
  Dvalue = 11.35
  Group = -> [Pb_element003]
  conduct = 2
  density = 1
  expand = 3
  formula = Pb
  name = G4_Pb
  specific = 4
FEATURE [App::DocumentObjectGroupPython] Bi_element002  label="Bi_element : 1"  # scripted group (container) (typed FeaturePython)
  n = 1
  ref = Bi_element
FEATURE [App::DocumentObjectGroupPython] G4_Bi  # scripted group (container) (typed FeaturePython)
  Dunit = g/cm3
  Dvalue = 9.747
  Group = -> [Bi_element002]
  conduct = 2
  density = 1
  expand = 3
  formula = Bi
  name = G4_Bi
  specific = 4
FEATURE [App::DocumentObjectGroupPython] Po_element001  label="Po_element : 1"  # scripted group (container) (typed FeaturePython)
  n = 1
  ref = Po_element
FEATURE [App::DocumentObjectGroupPython] G4_Po  # scripted group (container) (typed FeaturePython)
  Dunit = g/cm3
  Dvalue = 9.32
  Group = -> [Po_element001]
  conduct = 2
  density = 1
  expand = 3
  formula = Po
  name = G4_Po
  specific = 4
FEATURE [App::DocumentObjectGroupPython] At_element001  label="At_element : 1"  # scripted group (container) (typed FeaturePython)
  n = 1
  ref = At_element
FEATURE [App::DocumentObjectGroupPython] G4_At  # scripted group (container) (typed FeaturePython)
  Dunit = g/cm3
  Dvalue = 9.32
  Group = -> [At_element001]
  conduct = 2
  density = 1
  expand = 3
  formula = At
  name = G4_At
  specific = 4
FEATURE [App::DocumentObjectGroupPython] Rn_element001  label="Rn_element : 1"  # scripted group (container) (typed FeaturePython)
  n = 1
  ref = Rn_element
FEATURE [App::DocumentObjectGroupPython] G4_Rn  # scripted group (container) (typed FeaturePython)
  Dunit = g/cm3
  Dvalue = 0.00900662
  Group = -> [Rn_element001]
  conduct = 2
  density = 1
  expand = 3
  formula = Rn
  name = G4_Rn
  specific = 4
FEATURE [App::DocumentObjectGroupPython] Fr_element001  label="Fr_element : 1"  # scripted group (container) (typed FeaturePython)
  n = 1
  ref = Fr_element
FEATURE [App::DocumentObjectGroupPython] G4_Fr  # scripted group (container) (typed FeaturePython)
  Dunit = g/cm3
  Dvalue = 1
  Group = -> [Fr_element001]
  conduct = 2
  density = 1
  expand = 3
  formula = Fr
  name = G4_Fr
  specific = 4
FEATURE [App::DocumentObjectGroupPython] Ra_element001  label="Ra_element : 1"  # scripted group (container) (typed FeaturePython)
  n = 1
  ref = Ra_element
FEATURE [App::DocumentObjectGroupPython] G4_Ra  # scripted group (container) (typed FeaturePython)
  Dunit = g/cm3
  Dvalue = 5
  Group = -> [Ra_element001]
  conduct = 2
  density = 1
  expand = 3
  formula = Ra
  name = G4_Ra
  specific = 4
FEATURE [App::DocumentObjectGroupPython] Ac_element001  label="Ac_element : 1"  # scripted group (container) (typed FeaturePython)
  n = 1
  ref = Ac_element
FEATURE [App::DocumentObjectGroupPython] G4_Ac  # scripted group (container) (typed FeaturePython)
  Dunit = g/cm3
  Dvalue = 10.07
  Group = -> [Ac_element001]
  conduct = 2
  density = 1
  expand = 3
  formula = Ac
  name = G4_Ac
  specific = 4
FEATURE [App::DocumentObjectGroupPython] Th_element001  label="Th_element : 1"  # scripted group (container) (typed FeaturePython)
  n = 1
  ref = Th_element
FEATURE [App::DocumentObjectGroupPython] G4_Th  # scripted group (container) (typed FeaturePython)
  Dunit = g/cm3
  Dvalue = 11.72
  Group = -> [Th_element001]
  conduct = 2
  density = 1
  expand = 3
  formula = Th
  name = G4_Th
  specific = 4
FEATURE [App::DocumentObjectGroupPython] Pa_element001  label="Pa_element : 1"  # scripted group (container) (typed FeaturePython)
  n = 1
  ref = Pa_element
FEATURE [App::DocumentObjectGroupPython] G4_Pa  # scripted group (container) (typed FeaturePython)
  Dunit = g/cm3
  Dvalue = 15.37
  Group = -> [Pa_element001]
  conduct = 2
  density = 1
  expand = 3
  formula = Pa
  name = G4_Pa
  specific = 4
FEATURE [App::DocumentObjectGroupPython] U_element004  label="U_element : 004"  # scripted group (container) (typed FeaturePython)
  n = 1
  ref = U_element
FEATURE [App::DocumentObjectGroupPython] G4_U  # scripted group (container) (typed FeaturePython)
  Dunit = g/cm3
  Dvalue = 18.95
  Group = -> [U_element004]
  conduct = 2
  density = 1
  expand = 3
  formula = U
  name = G4_U
  specific = 4
FEATURE [App::DocumentObjectGroupPython] Np_element001  label="Np_element : 1"  # scripted group (container) (typed FeaturePython)
  n = 1
  ref = Np_element
FEATURE [App::DocumentObjectGroupPython] G4_Np  # scripted group (container) (typed FeaturePython)
  Dunit = g/cm3
  Dvalue = 20.25
  Group = -> [Np_element001]
  conduct = 2
  density = 1
  expand = 3
  formula = Np
  name = G4_Np
  specific = 4
FEATURE [App::DocumentObjectGroupPython] Pu_element002  label="Pu_element : 002"  # scripted group (container) (typed FeaturePython)
  n = 1
  ref = Pu_element
FEATURE [App::DocumentObjectGroupPython] G4_Pu  # scripted group (container) (typed FeaturePython)
  Dunit = g/cm3
  Dvalue = 19.84
  Group = -> [Pu_element002]
  conduct = 2
  density = 1
  expand = 3
  formula = Pu
  name = G4_Pu
  specific = 4
FEATURE [App::DocumentObjectGroupPython] Am_element001  label="Am_element : 1"  # scripted group (container) (typed FeaturePython)
  n = 1
  ref = Am_element
FEATURE [App::DocumentObjectGroupPython] G4_Am  # scripted group (container) (typed FeaturePython)
  Dunit = g/cm3
  Dvalue = 13.67
  Group = -> [Am_element001]
  conduct = 2
  density = 1
  expand = 3
  formula = Am
  name = G4_Am
  specific = 4
FEATURE [App::DocumentObjectGroupPython] Cm_element001  label="Cm_element : 1"  # scripted group (container) (typed FeaturePython)
  n = 1
  ref = Cm_element
FEATURE [App::DocumentObjectGroupPython] G4_Cm  # scripted group (container) (typed FeaturePython)
  Dunit = g/cm3
  Dvalue = 13.51
  Group = -> [Cm_element001]
  conduct = 2
  density = 1
  expand = 3
  formula = Cm
  name = G4_Cm
  specific = 4
FEATURE [App::DocumentObjectGroupPython] Bk_element001  label="Bk_element : 1"  # scripted group (container) (typed FeaturePython)
  n = 1
  ref = Bk_element
FEATURE [App::DocumentObjectGroupPython] G4_Bk  # scripted group (container) (typed FeaturePython)
  Dunit = g/cm3
  Dvalue = 14
  Group = -> [Bk_element001]
  conduct = 2
  density = 1
  expand = 3
  formula = Bk
  name = G4_Bk
  specific = 4
FEATURE [App::DocumentObjectGroupPython] Cf_element001  label="Cf_element : 1"  # scripted group (container) (typed FeaturePython)
  n = 1
  ref = Cf_element
FEATURE [App::DocumentObjectGroupPython] G4_Cf  # scripted group (container) (typed FeaturePython)
  Dunit = g/cm3
  Dvalue = 10
  Group = -> [Cf_element001]
  conduct = 2
  density = 1
  expand = 3
  formula = Cf
  name = G4_Cf
  specific = 4
FEATURE [App::DocumentObjectGroupPython] Element  # scripted group (container) (typed FeaturePython)
  Group = -> [G4_H,G4_He,G4_Li,G4_Be,G4_B,G4_C,G4_N,G4_O,G4_F,G4_Ne,G4_Na,G4_Mg,G4_Al,G4_Si,G4_P,G4_S,G4_Cl,G4_Ar,G4_K,G4_Ca,G4_Sc,G4_Ti,G4_V,G4_Cr,G4_Mn,G4_Fe,G4_Co,G4_Ni,G4_Cu,G4_Zn,G4_Ga,G4_Ge,G4_As,G4_Se,G4_Br,G4_Kr,G4_Rb,G4_Sr,G4_Y,G4_Zr,G4_Nb,G4_Mo,G4_Tc,G4_Ru,G4_Rh,G4_Pd,G4_Ag,G4_Cd,G4_In,G4_Sn,G4_Sb,G4_Te,G4_I,G4_Xe,G4_Cs,G4_Ba,G4_La,G4_Ce,G4_Pr,G4_Nd,G4_Pm,G4_Sm,G4_Eu,G4_Gd,G4_Tb,G4_Dy,G4_Ho,G4_Er,+30 more]
FEATURE [App::DocumentObjectGroupPython] H_element114  label="H_element : 063"  # scripted group (container) (typed FeaturePython)
  n = 2
  ref = H_element
FEATURE [App::DocumentObjectGroupPython] G4_lH2  # scripted group (container) (typed FeaturePython)
  Dunit = g/cm3
  Dvalue = 0.0708
  Group = -> [H_element114]
  conduct = 2
  density = 1
  expand = 3
  formula = G4_lH2
  name = G4_lH2
  specific = 4
FEATURE [App::DocumentObjectGroupPython] N_element049  label="N_element : 022"  # scripted group (container) (typed FeaturePython)
  n = 2
  ref = N_element
FEATURE [App::DocumentObjectGroupPython] G4_lN2  # scripted group (container) (typed FeaturePython)
  Dunit = g/cm3
  Dvalue = 0.807
  Group = -> [N_element049]
  conduct = 2
  density = 1
  expand = 3
  formula = G4_lN2
  name = G4_lN2
  specific = 4
FEATURE [App::DocumentObjectGroupPython] O_element106  label="O_element : 060"  # scripted group (container) (typed FeaturePython)
  n = 2
  ref = O_element
FEATURE [App::DocumentObjectGroupPython] G4_lO2  # scripted group (container) (typed FeaturePython)
  Dunit = g/cm3
  Dvalue = 1.141
  Group = -> [O_element106]
  conduct = 2
  density = 1
  expand = 3
  formula = G4_lO2
  name = G4_lO2
  specific = 4
FEATURE [App::DocumentObjectGroupPython] Ar_element003  label="Ar_element : 002"  # scripted group (container) (typed FeaturePython)
  n = 1
  ref = Ar_element
FEATURE [App::DocumentObjectGroupPython] G4_lAr  # scripted group (container) (typed FeaturePython)
  Dunit = g/cm3
  Dvalue = 1.396
  Group = -> [Ar_element003]
  conduct = 2
  density = 1
  expand = 3
  formula = G4_lAr
  name = G4_lAr
  specific = 4
FEATURE [App::DocumentObjectGroupPython] Br_element008  label="Br_element : 005"  # scripted group (container) (typed FeaturePython)
  n = 1
  ref = Br_element
FEATURE [App::DocumentObjectGroupPython] G4_lBr  # scripted group (container) (typed FeaturePython)
  Dunit = g/cm3
  Dvalue = 3.1028
  Group = -> [Br_element008]
  conduct = 2
  density = 1
  expand = 3
  formula = G4_lBr
  name = G4_lBr
  specific = 4
FEATURE [App::DocumentObjectGroupPython] Kr_element002  label="Kr_element : 002"  # scripted group (container) (typed FeaturePython)
  n = 1
  ref = Kr_element
FEATURE [App::DocumentObjectGroupPython] G4_lKr  # scripted group (container) (typed FeaturePython)
  Dunit = g/cm3
  Dvalue = 2.418
  Group = -> [Kr_element002]
  conduct = 2
  density = 1
  expand = 3
  formula = G4_lKr
  name = G4_lKr
  specific = 4
FEATURE [App::DocumentObjectGroupPython] Xe_element002  label="Xe_element : 002"  # scripted group (container) (typed FeaturePython)
  n = 1
  ref = Xe_element
FEATURE [App::DocumentObjectGroupPython] G4_lXe  # scripted group (container) (typed FeaturePython)
  Dunit = g/cm3
  Dvalue = 2.953
  Group = -> [Xe_element002]
  conduct = 2
  density = 1
  expand = 3
  formula = G4_lXe
  name = G4_lXe
  specific = 4
FEATURE [App::DocumentObjectGroupPython] O_element107  label="O_element : 061"  # scripted group (container) (typed FeaturePython)
  n = 4
  ref = O_element
FEATURE [App::DocumentObjectGroupPython] Pb_element004  label="Pb_element : 002"  # scripted group (container) (typed FeaturePython)
  n = 1
  ref = Pb_element
FEATURE [App::DocumentObjectGroupPython] W_element005  label="W_element : 005"  # scripted group (container) (typed FeaturePython)
  n = 1
  ref = W_element
FEATURE [App::DocumentObjectGroupPython] G4_PbWO4  # scripted group (container) (typed FeaturePython)
  Dunit = g/cm3
  Dvalue = 8.28
  Group = -> [O_element107,Pb_element004,W_element005]
  conduct = 2
  density = 1
  expand = 3
  formula = G4_PbWO4
  name = G4_PbWO4
  specific = 4
FEATURE [App::DocumentObjectGroupPython] H_element115  label="H_element : 064"  # scripted group (container) (typed FeaturePython)
  n = 1
  ref = H_element
FEATURE [App::DocumentObjectGroupPython] G4_Galactic  # scripted group (container) (typed FeaturePython)
  Dunit = g/cm3
  Dvalue = 0
  Group = -> [H_element115]
  conduct = 2
  density = 1
  expand = 3
  formula = G4_Galactic
  name = G4_Galactic
  specific = 4
FEATURE [App::DocumentObjectGroupPython] C_element125  label="C_element : 071"  # scripted group (container) (typed FeaturePython)
  n = 1
  ref = C_element
FEATURE [App::DocumentObjectGroupPython] G4_GRAPHITE_POROUS  # scripted group (container) (typed FeaturePython)
  Dunit = g/cm3
  Dvalue = 1.7
  Group = -> [C_element125]
  conduct = 2
  density = 1
  expand = 3
  formula = G4_GRAPHITE_POROUS
  name = G4_GRAPHITE_POROUS
  specific = 4
FEATURE [App::DocumentObjectGroupPython] H_element116  label="H_element : 0.150"  # scripted group (container) (typed FeaturePython)
  n = 0.080538
FEATURE [App::DocumentObjectGroupPython] C_element126  label="C_element : 0.600"  # scripted group (container) (typed FeaturePython)
  n = 0.599848
FEATURE [App::DocumentObjectGroupPython] O_element108  label="O_element : 0.320"  # scripted group (container) (typed FeaturePython)
  n = 0.319614
FEATURE [App::DocumentObjectGroupPython] G4_LUCITE  # scripted group (container) (typed FeaturePython)
  Dunit = g/cm3
  Dvalue = 1.19
  Group = -> [H_element116,C_element126,O_element108]
  conduct = 2
  density = 1
  expand = 3
  formula = G4_LUCITE
  name = G4_LUCITE
  specific = 4
FEATURE [App::DocumentObjectGroupPython] Cu_element002  label="Cu_element : 62"  # scripted group (container) (typed FeaturePython)
  n = 62
  ref = Cu_element
FEATURE [App::DocumentObjectGroupPython] Zn_element002  label="Zn_element : 35"  # scripted group (container) (typed FeaturePython)
  n = 35
  ref = Zn_element
FEATURE [App::DocumentObjectGroupPython] Pb_element005  label="Pb_element : 3"  # scripted group (container) (typed FeaturePython)
  n = 3
  ref = Pb_element
FEATURE [App::DocumentObjectGroupPython] G4_BRASS  # scripted group (container) (typed FeaturePython)
  Dunit = g/cm3
  Dvalue = 8.52
  Group = -> [Cu_element002,Zn_element002,Pb_element005]
  conduct = 2
  density = 1
  expand = 3
  formula = G4_BRASS
  name = G4_BRASS
  specific = 4
FEATURE [App::DocumentObjectGroupPython] Cu_element003  label="Cu_element : 89"  # scripted group (container) (typed FeaturePython)
  n = 89
  ref = Cu_element
FEATURE [App::DocumentObjectGroupPython] Zn_element003  label="Zn_element : 9"  # scripted group (container) (typed FeaturePython)
  n = 9
  ref = Zn_element
FEATURE [App::DocumentObjectGroupPython] Pb_element006  label="Pb_element : 2"  # scripted group (container) (typed FeaturePython)
  n = 2
  ref = Pb_element
FEATURE [App::DocumentObjectGroupPython] G4_BRONZE  # scripted group (container) (typed FeaturePython)
  Dunit = g/cm3
  Dvalue = 8.82
  Group = -> [Cu_element003,Zn_element003,Pb_element006]
  conduct = 2
  density = 1
  expand = 3
  formula = G4_BRONZE
  name = G4_BRONZE
  specific = 4
FEATURE [App::DocumentObjectGroupPython] Fe_element008  label="Fe_element : 74"  # scripted group (container) (typed FeaturePython)
  n = 74
  ref = Fe_element
FEATURE [App::DocumentObjectGroupPython] Cr_element002  label="Cr_element : 18"  # scripted group (container) (typed FeaturePython)
  n = 18
  ref = Cr_element
FEATURE [App::DocumentObjectGroupPython] Ni_element002  label="Ni_element : 8"  # scripted group (container) (typed FeaturePython)
  n = 8
  ref = Ni_element
FEATURE [App::DocumentObjectGroupPython] G4_STAINLESS_STEEL  label="G4_STAINLESS-STEEL"  # scripted group (container) (typed FeaturePython)
  Dunit = g/cm3
  Dvalue = 8
  Group = -> [Fe_element008,Cr_element002,Ni_element002]
  conduct = 2
  density = 1
  expand = 3
  formula = G4_STAINLESS-STEEL
  name = G4_STAINLESS-STEEL
  specific = 4
FEATURE [App::DocumentObjectGroupPython] H_element117  label="H_element : 065"  # scripted group (container) (typed FeaturePython)
  n = 18
  ref = H_element
FEATURE [App::DocumentObjectGroupPython] C_element127  label="C_element : 072"  # scripted group (container) (typed FeaturePython)
  n = 12
  ref = C_element
FEATURE [App::DocumentObjectGroupPython] O_element109  label="O_element : 062"  # scripted group (container) (typed FeaturePython)
  n = 7
  ref = O_element
FEATURE [App::DocumentObjectGroupPython] G4_CR39  # scripted group (container) (typed FeaturePython)
  Dunit = g/cm3
  Dvalue = 1.32
  Group = -> [H_element117,C_element127,O_element109]
  conduct = 2
  density = 1
  expand = 3
  formula = G4_CR39
  name = G4_CR39
  specific = 4
FEATURE [App::DocumentObjectGroupPython] H_element118  label="H_element : 38"  # scripted group (container) (typed FeaturePython)
  n = 38
  ref = H_element
FEATURE [App::DocumentObjectGroupPython] C_element128  label="C_element : 073"  # scripted group (container) (typed FeaturePython)
  n = 18
  ref = C_element
FEATURE [App::DocumentObjectGroupPython] O_element110  label="O_element : 063"  # scripted group (container) (typed FeaturePython)
  n = 1
  ref = O_element
FEATURE [App::DocumentObjectGroupPython] G4_OCTADECANOL  # scripted group (container) (typed FeaturePython)
  Dunit = g/cm3
  Dvalue = 0.812
  Group = -> [H_element118,C_element128,O_element110]
  conduct = 2
  density = 1
  expand = 3
  formula = G4_OCTADECANOL
  name = G4_OCTADECANOL
  specific = 4
FEATURE [App::DocumentObjectGroupPython] HEP  # scripted group (container) (typed FeaturePython)
  Group = -> [G4_lH2,G4_lN2,G4_lO2,G4_lAr,G4_lBr,G4_lKr,G4_lXe,G4_PbWO4,G4_Galactic,G4_GRAPHITE_POROUS,G4_LUCITE,G4_BRASS,G4_BRONZE,G4_STAINLESS_STEEL,G4_CR39,G4_OCTADECANOL]
FEATURE [App::DocumentObjectGroupPython] C_element129  label="C_element : 074"  # scripted group (container) (typed FeaturePython)
  n = 14
  ref = C_element
FEATURE [App::DocumentObjectGroupPython] H_element119  label="H_element : 066"  # scripted group (container) (typed FeaturePython)
  n = 10
  ref = H_element
FEATURE [App::DocumentObjectGroupPython] O_element111  label="O_element : 064"  # scripted group (container) (typed FeaturePython)
  n = 2
  ref = O_element
FEATURE [App::DocumentObjectGroupPython] N_element050  label="N_element : 023"  # scripted group (container) (typed FeaturePython)
  n = 2
  ref = N_element
FEATURE [App::DocumentObjectGroupPython] G4_KEVLAR  # scripted group (container) (typed FeaturePython)
  Dunit = g/cm3
  Dvalue = 1.44
  Group = -> [C_element129,H_element119,O_element111,N_element050]
  conduct = 2
  density = 1
  expand = 3
  formula = G4_KEVLAR
  name = G4_KEVLAR
  specific = 4
FEATURE [App::DocumentObjectGroupPython] C_element130  label="C_element : 075"  # scripted group (container) (typed FeaturePython)
  n = 10
  ref = C_element
FEATURE [App::DocumentObjectGroupPython] H_element120  label="H_element : 067"  # scripted group (container) (typed FeaturePython)
  n = 8
  ref = H_element
FEATURE [App::DocumentObjectGroupPython] O_element112  label="O_element : 065"  # scripted group (container) (typed FeaturePython)
  n = 4
  ref = O_element
FEATURE [App::DocumentObjectGroupPython] G4_DACRON  # scripted group (container) (typed FeaturePython)
  Dunit = g/cm3
  Dvalue = 1.4
  Group = -> [C_element130,H_element120,O_element112]
  conduct = 2
  density = 1
  expand = 3
  formula = G4_DACRON
  name = G4_DACRON
  specific = 4
FEATURE [App::DocumentObjectGroupPython] C_element131  label="C_element : 076"  # scripted group (container) (typed FeaturePython)
  n = 4
  ref = C_element
FEATURE [App::DocumentObjectGroupPython] H_element121  label="H_element : 068"  # scripted group (container) (typed FeaturePython)
  n = 5
  ref = H_element
FEATURE [App::DocumentObjectGroupPython] Cl_element030  label="Cl_element : 016"  # scripted group (container) (typed FeaturePython)
  n = 1
  ref = Cl_element
FEATURE [App::DocumentObjectGroupPython] G4_NEOPRENE  # scripted group (container) (typed FeaturePython)
  Dunit = g/cm3
  Dvalue = 1.23
  Group = -> [C_element131,H_element121,Cl_element030]
  conduct = 2
  density = 1
  expand = 3
  formula = G4_NEOPRENE
  name = G4_NEOPRENE
  specific = 4
FEATURE [App::DocumentObjectGroupPython] Space  # scripted group (container) (typed FeaturePython)
  Group = -> [G4_KEVLAR,G4_DACRON,G4_NEOPRENE]
FEATURE [App::DocumentObjectGroupPython] H_element122  label="H_element : 069"  # scripted group (container) (typed FeaturePython)
  n = 5
  ref = H_element
FEATURE [App::DocumentObjectGroupPython] C_element132  label="C_element : 077"  # scripted group (container) (typed FeaturePython)
  n = 4
  ref = C_element
FEATURE [App::DocumentObjectGroupPython] N_element051  label="N_element : 3"  # scripted group (container) (typed FeaturePython)
  n = 3
  ref = N_element
FEATURE [App::DocumentObjectGroupPython] O_element113  label="O_element : 066"  # scripted group (container) (typed FeaturePython)
  n = 1
  ref = O_element
FEATURE [App::DocumentObjectGroupPython] G4_CYTOSINE  # scripted group (container) (typed FeaturePython)
  Dunit = g/cm3
  Dvalue = 1.55
  Group = -> [H_element122,C_element132,N_element051,O_element113]
  conduct = 2
  density = 1
  expand = 3
  formula = G4_CYTOSINE
  name = G4_CYTOSINE
  specific = 4
FEATURE [App::DocumentObjectGroupPython] H_element123  label="H_element : 070"  # scripted group (container) (typed FeaturePython)
  n = 6
  ref = H_element
FEATURE [App::DocumentObjectGroupPython] C_element133  label="C_element : 078"  # scripted group (container) (typed FeaturePython)
  n = 5
  ref = C_element
FEATURE [App::DocumentObjectGroupPython] N_element052  label="N_element : 024"  # scripted group (container) (typed FeaturePython)
  n = 2
  ref = N_element
FEATURE [App::DocumentObjectGroupPython] O_element114  label="O_element : 067"  # scripted group (container) (typed FeaturePython)
  n = 2
  ref = O_element
FEATURE [App::DocumentObjectGroupPython] G4_THYMINE  # scripted group (container) (typed FeaturePython)
  Dunit = g/cm3
  Dvalue = 1.23
  Group = -> [H_element123,C_element133,N_element052,O_element114]
  conduct = 2
  density = 1
  expand = 3
  formula = G4_THYMINE
  name = G4_THYMINE
  specific = 4
FEATURE [App::DocumentObjectGroupPython] H_element124  label="H_element : 071"  # scripted group (container) (typed FeaturePython)
  n = 4
  ref = H_element
FEATURE [App::DocumentObjectGroupPython] C_element134  label="C_element : 079"  # scripted group (container) (typed FeaturePython)
  n = 4
  ref = C_element
FEATURE [App::DocumentObjectGroupPython] N_element053  label="N_element : 025"  # scripted group (container) (typed FeaturePython)
  n = 2
  ref = N_element
FEATURE [App::DocumentObjectGroupPython] O_element115  label="O_element : 068"  # scripted group (container) (typed FeaturePython)
  n = 2
  ref = O_element
FEATURE [App::DocumentObjectGroupPython] G4_URACIL  # scripted group (container) (typed FeaturePython)
  Dunit = g/cm3
  Dvalue = 1.32
  Group = -> [H_element124,C_element134,N_element053,O_element115]
  conduct = 2
  density = 1
  expand = 3
  formula = G4_URACIL
  name = G4_URACIL
  specific = 4
FEATURE [App::DocumentObjectGroupPython] H_element125  label="H_element : 072"  # scripted group (container) (typed FeaturePython)
  n = 4
  ref = H_element
FEATURE [App::DocumentObjectGroupPython] C_element135  label="C_element : 080"  # scripted group (container) (typed FeaturePython)
  n = 5
  ref = C_element
FEATURE [App::DocumentObjectGroupPython] N_element054  label="N_element : 026"  # scripted group (container) (typed FeaturePython)
  n = 5
  ref = N_element
FEATURE [App::DocumentObjectGroupPython] G4_DNA_ADENINE  # scripted group (container) (typed FeaturePython)
  Dunit = g/cm3
  Dvalue = 1
  Group = -> [H_element125,C_element135,N_element054]
  conduct = 2
  density = 1
  expand = 3
  formula = G4_DNA_ADENINE
  name = G4_DNA_ADENINE
  specific = 4
FEATURE [App::DocumentObjectGroupPython] H_element126  label="H_element : 073"  # scripted group (container) (typed FeaturePython)
  n = 4
  ref = H_element
FEATURE [App::DocumentObjectGroupPython] C_element136  label="C_element : 081"  # scripted group (container) (typed FeaturePython)
  n = 5
  ref = C_element
FEATURE [App::DocumentObjectGroupPython] N_element055  label="N_element : 027"  # scripted group (container) (typed FeaturePython)
  n = 5
  ref = N_element
FEATURE [App::DocumentObjectGroupPython] O_element116  label="O_element : 069"  # scripted group (container) (typed FeaturePython)
  n = 1
  ref = O_element
FEATURE [App::DocumentObjectGroupPython] G4_DNA_GUANINE  # scripted group (container) (typed FeaturePython)
  Dunit = g/cm3
  Dvalue = 1
  Group = -> [H_element126,C_element136,N_element055,O_element116]
  conduct = 2
  density = 1
  expand = 3
  formula = G4_DNA_GUANINE
  name = G4_DNA_GUANINE
  specific = 4
FEATURE [App::DocumentObjectGroupPython] H_element127  label="H_element : 074"  # scripted group (container) (typed FeaturePython)
  n = 4
  ref = H_element
FEATURE [App::DocumentObjectGroupPython] C_element137  label="C_element : 082"  # scripted group (container) (typed FeaturePython)
  n = 4
  ref = C_element
FEATURE [App::DocumentObjectGroupPython] N_element056  label="N_element : 028"  # scripted group (container) (typed FeaturePython)
  n = 3
  ref = N_element
FEATURE [App::DocumentObjectGroupPython] O_element117  label="O_element : 070"  # scripted group (container) (typed FeaturePython)
  n = 1
  ref = O_element
FEATURE [App::DocumentObjectGroupPython] G4_DNA_CYTOSINE  # scripted group (container) (typed FeaturePython)
  Dunit = g/cm3
  Dvalue = 1
  Group = -> [H_element127,C_element137,N_element056,O_element117]
  conduct = 2
  density = 1
  expand = 3
  formula = G4_DNA_CYTOSINE
  name = G4_DNA_CYTOSINE
  specific = 4
FEATURE [App::DocumentObjectGroupPython] H_element128  label="H_element : 075"  # scripted group (container) (typed FeaturePython)
  n = 5
  ref = H_element
FEATURE [App::DocumentObjectGroupPython] C_element138  label="C_element : 083"  # scripted group (container) (typed FeaturePython)
  n = 5
  ref = C_element
FEATURE [App::DocumentObjectGroupPython] N_element057  label="N_element : 029"  # scripted group (container) (typed FeaturePython)
  n = 2
  ref = N_element
FEATURE [App::DocumentObjectGroupPython] O_element118  label="O_element : 071"  # scripted group (container) (typed FeaturePython)
  n = 2
  ref = O_element
FEATURE [App::DocumentObjectGroupPython] G4_DNA_THYMINE  # scripted group (container) (typed FeaturePython)
  Dunit = g/cm3
  Dvalue = 1
  Group = -> [H_element128,C_element138,N_element057,O_element118]
  conduct = 2
  density = 1
  expand = 3
  formula = G4_DNA_THYMINE
  name = G4_DNA_THYMINE
  specific = 4
FEATURE [App::DocumentObjectGroupPython] H_element129  label="H_element : 076"  # scripted group (container) (typed FeaturePython)
  n = 3
  ref = H_element
FEATURE [App::DocumentObjectGroupPython] C_element139  label="C_element : 084"  # scripted group (container) (typed FeaturePython)
  n = 4
  ref = C_element
FEATURE [App::DocumentObjectGroupPython] N_element058  label="N_element : 030"  # scripted group (container) (typed FeaturePython)
  n = 2
  ref = N_element
FEATURE [App::DocumentObjectGroupPython] O_element119  label="O_element : 072"  # scripted group (container) (typed FeaturePython)
  n = 2
  ref = O_element
FEATURE [App::DocumentObjectGroupPython] G4_DNA_URACIL  # scripted group (container) (typed FeaturePython)
  Dunit = g/cm3
  Dvalue = 1
  Group = -> [H_element129,C_element139,N_element058,O_element119]
  conduct = 2
  density = 1
  expand = 3
  formula = G4_DNA_URACIL
  name = G4_DNA_URACIL
  specific = 4
FEATURE [App::DocumentObjectGroupPython] H_element130  label="H_element : 077"  # scripted group (container) (typed FeaturePython)
  n = 10
  ref = H_element
FEATURE [App::DocumentObjectGroupPython] C_element140  label="C_element : 085"  # scripted group (container) (typed FeaturePython)
  n = 10
  ref = C_element
FEATURE [App::DocumentObjectGroupPython] N_element059  label="N_element : 031"  # scripted group (container) (typed FeaturePython)
  n = 5
  ref = N_element
FEATURE [App::DocumentObjectGroupPython] O_element120  label="O_element : 073"  # scripted group (container) (typed FeaturePython)
  n = 4
  ref = O_element
FEATURE [App::DocumentObjectGroupPython] G4_DNA_ADENOSINE  # scripted group (container) (typed FeaturePython)
  Dunit = g/cm3
  Dvalue = 1
  Group = -> [H_element130,C_element140,N_element059,O_element120]
  conduct = 2
  density = 1
  expand = 3
  formula = G4_DNA_ADENOSINE
  name = G4_DNA_ADENOSINE
  specific = 4
FEATURE [App::DocumentObjectGroupPython] H_element131  label="H_element : 078"  # scripted group (container) (typed FeaturePython)
  n = 10
  ref = H_element
FEATURE [App::DocumentObjectGroupPython] C_element141  label="C_element : 086"  # scripted group (container) (typed FeaturePython)
  n = 10
  ref = C_element
FEATURE [App::DocumentObjectGroupPython] N_element060  label="N_element : 032"  # scripted group (container) (typed FeaturePython)
  n = 5
  ref = N_element
FEATURE [App::DocumentObjectGroupPython] O_element121  label="O_element : 074"  # scripted group (container) (typed FeaturePython)
  n = 5
  ref = O_element
FEATURE [App::DocumentObjectGroupPython] G4_DNA_GUANOSINE  # scripted group (container) (typed FeaturePython)
  Dunit = g/cm3
  Dvalue = 1
  Group = -> [H_element131,C_element141,N_element060,O_element121]
  conduct = 2
  density = 1
  expand = 3
  formula = G4_DNA_GUANOSINE
  name = G4_DNA_GUANOSINE
  specific = 4
FEATURE [App::DocumentObjectGroupPython] H_element132  label="H_element : 079"  # scripted group (container) (typed FeaturePython)
  n = 10
  ref = H_element
FEATURE [App::DocumentObjectGroupPython] C_element142  label="C_element : 087"  # scripted group (container) (typed FeaturePython)
  n = 9
  ref = C_element
FEATURE [App::DocumentObjectGroupPython] N_element061  label="N_element : 033"  # scripted group (container) (typed FeaturePython)
  n = 3
  ref = N_element
FEATURE [App::DocumentObjectGroupPython] O_element122  label="O_element : 075"  # scripted group (container) (typed FeaturePython)
  n = 5
  ref = O_element
FEATURE [App::DocumentObjectGroupPython] G4_DNA_CYTIDINE  # scripted group (container) (typed FeaturePython)
  Dunit = g/cm3
  Dvalue = 1
  Group = -> [H_element132,C_element142,N_element061,O_element122]
  conduct = 2
  density = 1
  expand = 3
  formula = G4_DNA_CYTIDINE
  name = G4_DNA_CYTIDINE
  specific = 4
FEATURE [App::DocumentObjectGroupPython] H_element133  label="H_element : 080"  # scripted group (container) (typed FeaturePython)
  n = 9
  ref = H_element
FEATURE [App::DocumentObjectGroupPython] C_element143  label="C_element : 088"  # scripted group (container) (typed FeaturePython)
  n = 9
  ref = C_element
FEATURE [App::DocumentObjectGroupPython] N_element062  label="N_element : 034"  # scripted group (container) (typed FeaturePython)
  n = 2
  ref = N_element
FEATURE [App::DocumentObjectGroupPython] O_element123  label="O_element : 076"  # scripted group (container) (typed FeaturePython)
  n = 6
  ref = O_element
FEATURE [App::DocumentObjectGroupPython] G4_DNA_URIDINE  # scripted group (container) (typed FeaturePython)
  Dunit = g/cm3
  Dvalue = 1
  Group = -> [H_element133,C_element143,N_element062,O_element123]
  conduct = 2
  density = 1
  expand = 3
  formula = G4_DNA_URIDINE
  name = G4_DNA_URIDINE
  specific = 4
FEATURE [App::DocumentObjectGroupPython] H_element134  label="H_element : 081"  # scripted group (container) (typed FeaturePython)
  n = 11
  ref = H_element
FEATURE [App::DocumentObjectGroupPython] C_element144  label="C_element : 089"  # scripted group (container) (typed FeaturePython)
  n = 10
  ref = C_element
FEATURE [App::DocumentObjectGroupPython] N_element063  label="N_element : 035"  # scripted group (container) (typed FeaturePython)
  n = 2
  ref = N_element
FEATURE [App::DocumentObjectGroupPython] O_element124  label="O_element : 077"  # scripted group (container) (typed FeaturePython)
  n = 6
  ref = O_element
FEATURE [App::DocumentObjectGroupPython] G4_DNA_METHYLURIDINE  # scripted group (container) (typed FeaturePython)
  Dunit = g/cm3
  Dvalue = 1
  Group = -> [H_element134,C_element144,N_element063,O_element124]
  conduct = 2
  density = 1
  expand = 3
  formula = G4_DNA_METHYLURIDINE
  name = G4_DNA_METHYLURIDINE
  specific = 4
FEATURE [App::DocumentObjectGroupPython] P_element014  label="P_element : 003"  # scripted group (container) (typed FeaturePython)
  n = 1
  ref = P_element
FEATURE [App::DocumentObjectGroupPython] O_element125  label="O_element : 078"  # scripted group (container) (typed FeaturePython)
  n = 3
  ref = O_element
FEATURE [App::DocumentObjectGroupPython] G4_DNA_MONOPHOSPHATE  # scripted group (container) (typed FeaturePython)
  Dunit = g/cm3
  Dvalue = 1
  Group = -> [P_element014,O_element125]
  conduct = 2
  density = 1
  expand = 3
  formula = G4_DNA_MONOPHOSPHATE
  name = G4_DNA_MONOPHOSPHATE
  specific = 4
FEATURE [App::DocumentObjectGroupPython] H_element135  label="H_element : 082"  # scripted group (container) (typed FeaturePython)
  n = 10
  ref = H_element
FEATURE [App::DocumentObjectGroupPython] C_element145  label="C_element : 090"  # scripted group (container) (typed FeaturePython)
  n = 10
  ref = C_element
FEATURE [App::DocumentObjectGroupPython] N_element064  label="N_element : 036"  # scripted group (container) (typed FeaturePython)
  n = 5
  ref = N_element
FEATURE [App::DocumentObjectGroupPython] O_element126  label="O_element : 079"  # scripted group (container) (typed FeaturePython)
  n = 7
  ref = O_element
FEATURE [App::DocumentObjectGroupPython] P_element015  label="P_element : 004"  # scripted group (container) (typed FeaturePython)
  n = 1
  ref = P_element
FEATURE [App::DocumentObjectGroupPython] G4_DNA_A  # scripted group (container) (typed FeaturePython)
  Dunit = g/cm3
  Dvalue = 1
  Group = -> [H_element135,C_element145,N_element064,O_element126,P_element015]
  conduct = 2
  density = 1
  expand = 3
  formula = G4_DNA_A
  name = G4_DNA_A
  specific = 4
FEATURE [App::DocumentObjectGroupPython] H_element136  label="H_element : 083"  # scripted group (container) (typed FeaturePython)
  n = 10
  ref = H_element
FEATURE [App::DocumentObjectGroupPython] C_element146  label="C_element : 091"  # scripted group (container) (typed FeaturePython)
  n = 10
  ref = C_element
FEATURE [App::DocumentObjectGroupPython] N_element065  label="N_element : 037"  # scripted group (container) (typed FeaturePython)
  n = 5
  ref = N_element
FEATURE [App::DocumentObjectGroupPython] O_element127  label="O_element : 8"  # scripted group (container) (typed FeaturePython)
  n = 8
  ref = O_element
FEATURE [App::DocumentObjectGroupPython] P_element016  label="P_element : 005"  # scripted group (container) (typed FeaturePython)
  n = 1
  ref = P_element
FEATURE [App::DocumentObjectGroupPython] G4_DNA_G  # scripted group (container) (typed FeaturePython)
  Dunit = g/cm3
  Dvalue = 1
  Group = -> [H_element136,C_element146,N_element065,O_element127,P_element016]
  conduct = 2
  density = 1
  expand = 3
  formula = G4_DNA_G
  name = G4_DNA_G
  specific = 4
FEATURE [App::DocumentObjectGroupPython] H_element137  label="H_element : 084"  # scripted group (container) (typed FeaturePython)
  n = 10
  ref = H_element
FEATURE [App::DocumentObjectGroupPython] C_element147  label="C_element : 092"  # scripted group (container) (typed FeaturePython)
  n = 9
  ref = C_element
FEATURE [App::DocumentObjectGroupPython] N_element066  label="N_element : 038"  # scripted group (container) (typed FeaturePython)
  n = 3
  ref = N_element
FEATURE [App::DocumentObjectGroupPython] O_element128  label="O_element : 080"  # scripted group (container) (typed FeaturePython)
  n = 8
  ref = O_element
FEATURE [App::DocumentObjectGroupPython] P_element017  label="P_element : 006"  # scripted group (container) (typed FeaturePython)
  n = 1
  ref = P_element
FEATURE [App::DocumentObjectGroupPython] G4_DNA_C  # scripted group (container) (typed FeaturePython)
  Dunit = g/cm3
  Dvalue = 1
  Group = -> [H_element137,C_element147,N_element066,O_element128,P_element017]
  conduct = 2
  density = 1
  expand = 3
  formula = G4_DNA_C
  name = G4_DNA_C
  specific = 4
FEATURE [App::DocumentObjectGroupPython] H_element138  label="H_element : 085"  # scripted group (container) (typed FeaturePython)
  n = 9
  ref = H_element
FEATURE [App::DocumentObjectGroupPython] C_element148  label="C_element : 093"  # scripted group (container) (typed FeaturePython)
  n = 9
  ref = C_element
FEATURE [App::DocumentObjectGroupPython] N_element067  label="N_element : 039"  # scripted group (container) (typed FeaturePython)
  n = 2
  ref = N_element
FEATURE [App::DocumentObjectGroupPython] O_element129  label="O_element : 9"  # scripted group (container) (typed FeaturePython)
  n = 9
  ref = O_element
FEATURE [App::DocumentObjectGroupPython] P_element018  label="P_element : 007"  # scripted group (container) (typed FeaturePython)
  n = 1
  ref = P_element
FEATURE [App::DocumentObjectGroupPython] G4_DNA_U  # scripted group (container) (typed FeaturePython)
  Dunit = g/cm3
  Dvalue = 1
  Group = -> [H_element138,C_element148,N_element067,O_element129,P_element018]
  conduct = 2
  density = 1
  expand = 3
  formula = G4_DNA_U
  name = G4_DNA_U
  specific = 4
FEATURE [App::DocumentObjectGroupPython] H_element139  label="H_element : 086"  # scripted group (container) (typed FeaturePython)
  n = 11
  ref = H_element
FEATURE [App::DocumentObjectGroupPython] C_element149  label="C_element : 094"  # scripted group (container) (typed FeaturePython)
  n = 10
  ref = C_element
FEATURE [App::DocumentObjectGroupPython] N_element068  label="N_element : 040"  # scripted group (container) (typed FeaturePython)
  n = 2
  ref = N_element
FEATURE [App::DocumentObjectGroupPython] O_element130  label="O_element : 081"  # scripted group (container) (typed FeaturePython)
  n = 9
  ref = O_element
FEATURE [App::DocumentObjectGroupPython] P_element019  label="P_element : 008"  # scripted group (container) (typed FeaturePython)
  n = 1
  ref = P_element
FEATURE [App::DocumentObjectGroupPython] G4_DNA_MU  # scripted group (container) (typed FeaturePython)
  Dunit = g/cm3
  Dvalue = 1
  Group = -> [H_element139,C_element149,N_element068,O_element130,P_element019]
  conduct = 2
  density = 1
  expand = 3
  formula = G4_DNA_MU
  name = G4_DNA_MU
  specific = 4
FEATURE [App::DocumentObjectGroupPython] BioChemical  # scripted group (container) (typed FeaturePython)
  Group = -> [G4_CYTOSINE,G4_THYMINE,G4_URACIL,G4_DNA_ADENINE,G4_DNA_GUANINE,G4_DNA_CYTOSINE,G4_DNA_THYMINE,G4_DNA_URACIL,G4_DNA_ADENOSINE,G4_DNA_GUANOSINE,G4_DNA_CYTIDINE,G4_DNA_URIDINE,G4_DNA_METHYLURIDINE,G4_DNA_MONOPHOSPHATE,G4_DNA_A,G4_DNA_G,G4_DNA_C,G4_DNA_U,G4_DNA_MU]
FEATURE [App::DocumentObjectGroupPython] G4Materials  # scripted group (container) (typed FeaturePython)
  Group = -> [NIST,Element,HEP,Space,BioChemical]
  version = 1
FEATURE [App::DocumentObjectGroupPython] Geant4  # scripted group (container) (typed FeaturePython)
  Group = -> [G4Isotopes,G4Elements,G4Materials]
FEATURE [App::DocumentObjectGroupPython] Materials  # scripted group (container) (typed FeaturePython)
  Group = -> [Geant4]
FEATURE [Part::FeaturePython] GDMLBox_WorldBox  # WARN: FeaturePython — macro-defined, semantics opaque (R4)
  lunit = 2
  material = 5
  x = 100
  y = 100
  z = 100
FEATURE [Part::Box] Box001  label="Cube001"
  AttacherType = Attacher::AttachEngine3D
  Height = 10
  Length = 10
  Width = 10
FEATURE [Part::Fillet] Fillet
  Base = -> Box001
  EdgeLinks = -> Box001 [Edge1,Edge2,Edge3,Edge4,Edge5,Edge6,Edge7,Edge8,Edge9,Edge10,Edge11,Edge12]
  Edges = 12 edges r=1: [Edge1,Edge2,Edge3,Edge4,Edge5,Edge6,Edge7,Edge8,Edge9,Edge10,Edge11,Edge12]
  Placement = pos=(0,0,-7) rot=(0,0,1;0rad)
FEATURE [App::Part] Part  label="Part_fillet"
  Group = -> [Box001,Fillet]
  Origin = -> Origin001
  Placement = pos=(-14,0,15) rot=(0,0,1;0rad)
FEATURE [App::Part] worldVOL
  Group = -> [GDMLBox_WorldBox,Part]
  Origin = -> Origin
